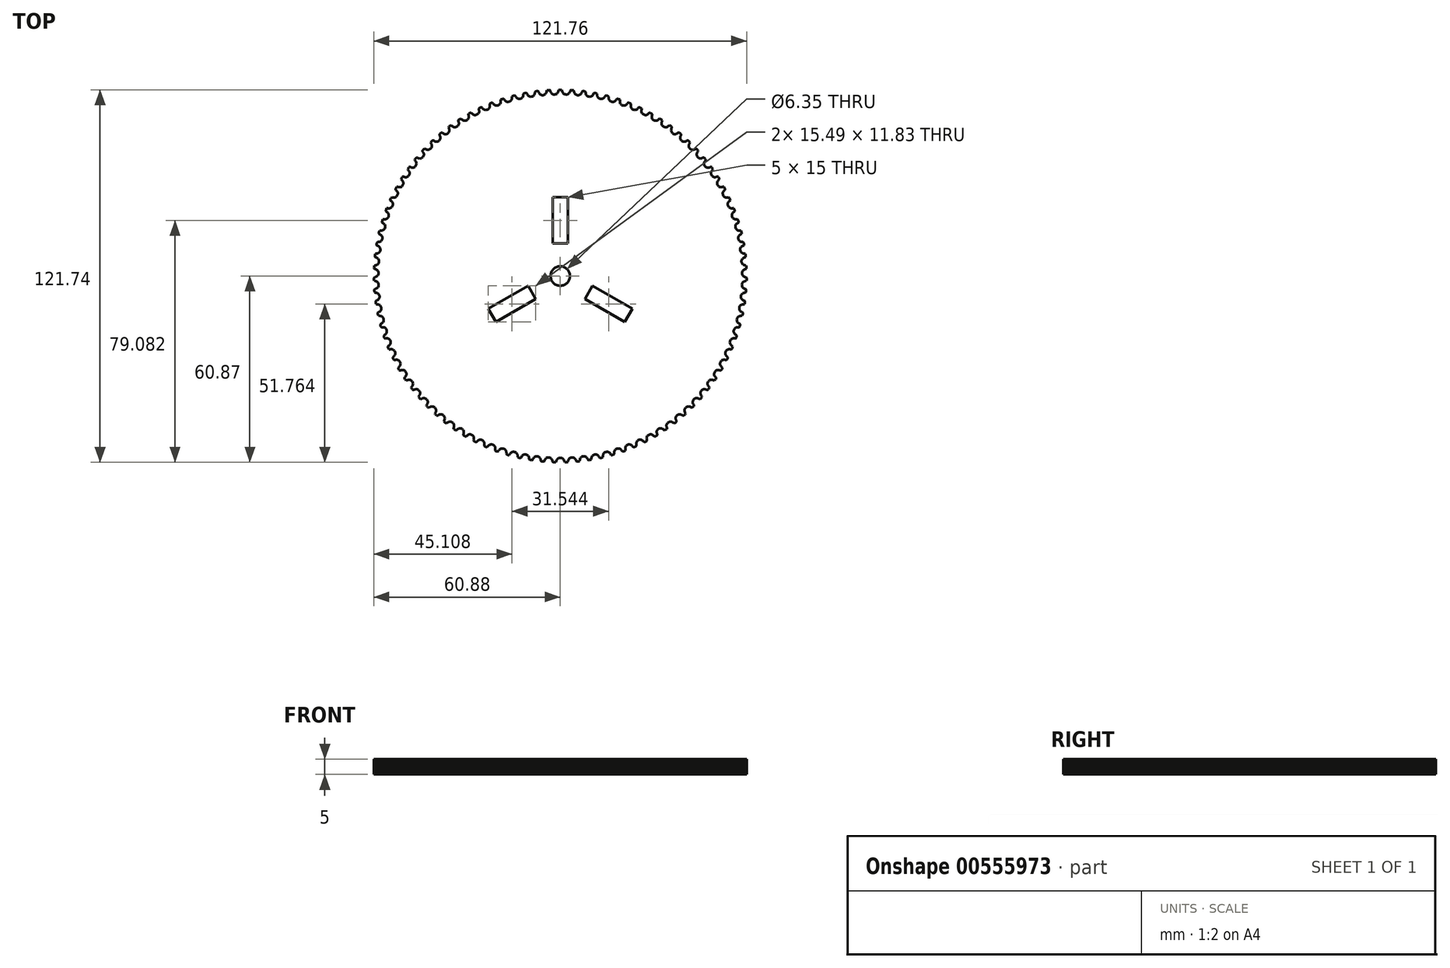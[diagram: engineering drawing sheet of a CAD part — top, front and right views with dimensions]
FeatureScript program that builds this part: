
annotation { "Feature Type Name" : "Feature", "Feature Type Description" : "" }
export const myFeature = defineFeature(function(context is Context, id is Id, definition is map)
    precondition{}
    {
        {
            var Q0;
            Q0=qCreatedBy(makeId("Top.planeOp"),FACE);
            var sketch = newSketch(context, id + "F0", { "sketchPlane" : qUnion([Q0])});
            skLineSegment(sketch, "E0", {"start": v(1.93, -60.87) * mm, "end": v(2.22, -60.86) * mm});
            skLineSegment(sketch, "E1", {"start": v(2.22, -60.86) * mm, "end": v(2.43, -60.77) * mm});
            skLineSegment(sketch, "E2", {"start": v(2.43, -60.77) * mm, "end": v(2.53, -60.58) * mm});
            skLineSegment(sketch, "E3", {"start": v(2.53, -60.58) * mm, "end": v(2.56, -60.37) * mm});
            skLineSegment(sketch, "E4", {"start": v(2.56, -60.37) * mm, "end": v(2.61, -60.16) * mm});
            skLineSegment(sketch, "E5", {"start": v(2.61, -60.16) * mm, "end": v(2.7, -59.96) * mm});
            skLineSegment(sketch, "E6", {"start": v(2.7, -59.96) * mm, "end": v(2.8, -59.77) * mm});
            skLineSegment(sketch, "E7", {"start": v(2.8, -59.77) * mm, "end": v(3, -59.57) * mm});
            skLineSegment(sketch, "E8", {"start": v(3, -59.57) * mm, "end": v(3.23, -59.41) * mm});
            skLineSegment(sketch, "E9", {"start": v(3.23, -59.41) * mm, "end": v(3.49, -59.31) * mm});
            skLineSegment(sketch, "E10", {"start": v(3.49, -59.31) * mm, "end": v(3.77, -59.27) * mm});
            skLineSegment(sketch, "E11", {"start": v(3.77, -59.27) * mm, "end": v(4.05, -59.28) * mm});
            skLineSegment(sketch, "E12", {"start": v(4.05, -59.28) * mm, "end": v(4.32, -59.34) * mm});
            skLineSegment(sketch, "E13", {"start": v(4.32, -59.34) * mm, "end": v(4.57, -59.47) * mm});
            skLineSegment(sketch, "E14", {"start": v(4.57, -59.47) * mm, "end": v(4.79, -59.64) * mm});
            skLineSegment(sketch, "E15", {"start": v(4.79, -59.64) * mm, "end": v(4.92, -59.82) * mm});
            skLineSegment(sketch, "E16", {"start": v(4.92, -59.82) * mm, "end": v(5.02, -60.01) * mm});
            skLineSegment(sketch, "E17", {"start": v(5.02, -60.01) * mm, "end": v(5.1, -60.2) * mm});
            skLineSegment(sketch, "E18", {"start": v(5.1, -60.2) * mm, "end": v(5.16, -60.42) * mm});
            skLineSegment(sketch, "E19", {"start": v(5.16, -60.42) * mm, "end": v(5.28, -60.6) * mm});
            skLineSegment(sketch, "E20", {"start": v(5.28, -60.6) * mm, "end": v(5.5, -60.65) * mm});
            skLineSegment(sketch, "E21", {"start": v(5.5, -60.65) * mm, "end": v(5.79, -60.62) * mm});
            skLineSegment(sketch, "E22", {"start": v(5.79, -60.62) * mm, "end": v(6.07, -60.6) * mm});
            skLineSegment(sketch, "E23", {"start": v(6.07, -60.6) * mm, "end": v(6.28, -60.5) * mm});
            skLineSegment(sketch, "E24", {"start": v(6.28, -60.5) * mm, "end": v(6.36, -60.3) * mm});
            skLineSegment(sketch, "E25", {"start": v(6.36, -60.3) * mm, "end": v(6.38, -60.09) * mm});
            skLineSegment(sketch, "E26", {"start": v(6.38, -60.09) * mm, "end": v(6.42, -59.88) * mm});
            skLineSegment(sketch, "E27", {"start": v(6.42, -59.88) * mm, "end": v(6.49, -59.67) * mm});
            skLineSegment(sketch, "E28", {"start": v(6.49, -59.67) * mm, "end": v(6.58, -59.47) * mm});
            skLineSegment(sketch, "E29", {"start": v(6.58, -59.47) * mm, "end": v(6.76, -59.26) * mm});
            skLineSegment(sketch, "E30", {"start": v(6.76, -59.26) * mm, "end": v(6.99, -59.09) * mm});
            skLineSegment(sketch, "E31", {"start": v(6.99, -59.09) * mm, "end": v(7.24, -58.97) * mm});
            skLineSegment(sketch, "E32", {"start": v(7.24, -58.97) * mm, "end": v(7.52, -58.9) * mm});
            skLineSegment(sketch, "E33", {"start": v(7.52, -58.9) * mm, "end": v(7.8, -58.9) * mm});
            skLineSegment(sketch, "E34", {"start": v(7.8, -58.9) * mm, "end": v(8.07, -58.95) * mm});
            skLineSegment(sketch, "E35", {"start": v(8.07, -58.95) * mm, "end": v(8.33, -59.06) * mm});
            skLineSegment(sketch, "E36", {"start": v(8.33, -59.06) * mm, "end": v(8.56, -59.22) * mm});
            skLineSegment(sketch, "E37", {"start": v(8.56, -59.22) * mm, "end": v(8.7, -59.39) * mm});
            skLineSegment(sketch, "E38", {"start": v(8.7, -59.39) * mm, "end": v(8.82, -59.57) * mm});
            skLineSegment(sketch, "E39", {"start": v(8.82, -59.57) * mm, "end": v(8.91, -59.76) * mm});
            skLineSegment(sketch, "E40", {"start": v(8.91, -59.76) * mm, "end": v(8.98, -59.97) * mm});
            skLineSegment(sketch, "E41", {"start": v(8.98, -59.97) * mm, "end": v(9.12, -60.13) * mm});
            skLineSegment(sketch, "E42", {"start": v(9.12, -60.13) * mm, "end": v(9.34, -60.18) * mm});
            skLineSegment(sketch, "E43", {"start": v(9.34, -60.18) * mm, "end": v(9.62, -60.13) * mm});
            skLineSegment(sketch, "E44", {"start": v(9.62, -60.13) * mm, "end": v(9.9, -60.09) * mm});
            skLineSegment(sketch, "E45", {"start": v(9.9, -60.09) * mm, "end": v(10.1, -59.98) * mm});
            skLineSegment(sketch, "E46", {"start": v(10.1, -59.98) * mm, "end": v(10.17, -59.78) * mm});
            skLineSegment(sketch, "E47", {"start": v(10.17, -59.78) * mm, "end": v(10.18, -59.56) * mm});
            skLineSegment(sketch, "E48", {"start": v(10.18, -59.56) * mm, "end": v(10.2, -59.35) * mm});
            skLineSegment(sketch, "E49", {"start": v(10.2, -59.35) * mm, "end": v(10.26, -59.14) * mm});
            skLineSegment(sketch, "E50", {"start": v(10.26, -59.14) * mm, "end": v(10.34, -58.93) * mm});
            skLineSegment(sketch, "E51", {"start": v(10.34, -58.93) * mm, "end": v(10.5, -58.7) * mm});
            skLineSegment(sketch, "E52", {"start": v(10.5, -58.7) * mm, "end": v(10.72, -58.53) * mm});
            skLineSegment(sketch, "E53", {"start": v(10.72, -58.53) * mm, "end": v(10.97, -58.4) * mm});
            skLineSegment(sketch, "E54", {"start": v(10.97, -58.4) * mm, "end": v(11.24, -58.31) * mm});
            skLineSegment(sketch, "E55", {"start": v(11.24, -58.31) * mm, "end": v(11.52, -58.29) * mm});
            skLineSegment(sketch, "E56", {"start": v(11.52, -58.29) * mm, "end": v(11.8, -58.32) * mm});
            skLineSegment(sketch, "E57", {"start": v(11.8, -58.32) * mm, "end": v(12.06, -58.4) * mm});
            skLineSegment(sketch, "E58", {"start": v(12.06, -58.4) * mm, "end": v(12.3, -58.56) * mm});
            skLineSegment(sketch, "E59", {"start": v(12.3, -58.56) * mm, "end": v(12.45, -58.72) * mm});
            skLineSegment(sketch, "E60", {"start": v(12.45, -58.72) * mm, "end": v(12.58, -58.9) * mm});
            skLineSegment(sketch, "E61", {"start": v(12.58, -58.9) * mm, "end": v(12.69, -59.08) * mm});
            skLineSegment(sketch, "E62", {"start": v(12.69, -59.08) * mm, "end": v(12.77, -59.28) * mm});
            skLineSegment(sketch, "E63", {"start": v(12.77, -59.28) * mm, "end": v(12.9, -59.43) * mm});
            skLineSegment(sketch, "E64", {"start": v(12.9, -59.43) * mm, "end": v(13.13, -59.46) * mm});
            skLineSegment(sketch, "E65", {"start": v(13.13, -59.46) * mm, "end": v(13.41, -59.4) * mm});
            skLineSegment(sketch, "E66", {"start": v(13.41, -59.4) * mm, "end": v(13.7, -59.34) * mm});
            skLineSegment(sketch, "E67", {"start": v(13.7, -59.34) * mm, "end": v(13.88, -59.21) * mm});
            skLineSegment(sketch, "E68", {"start": v(13.88, -59.21) * mm, "end": v(13.94, -59.01) * mm});
            skLineSegment(sketch, "E69", {"start": v(13.94, -59.01) * mm, "end": v(13.93, -58.8) * mm});
            skLineSegment(sketch, "E70", {"start": v(13.93, -58.8) * mm, "end": v(13.95, -58.58) * mm});
            skLineSegment(sketch, "E71", {"start": v(13.95, -58.58) * mm, "end": v(13.99, -58.37) * mm});
            skLineSegment(sketch, "E72", {"start": v(13.99, -58.37) * mm, "end": v(14.06, -58.16) * mm});
            skLineSegment(sketch, "E73", {"start": v(14.06, -58.16) * mm, "end": v(14.2, -57.92) * mm});
            skLineSegment(sketch, "E74", {"start": v(14.2, -57.92) * mm, "end": v(14.4, -57.73) * mm});
            skLineSegment(sketch, "E75", {"start": v(14.4, -57.73) * mm, "end": v(14.65, -57.58) * mm});
            skLineSegment(sketch, "E76", {"start": v(14.65, -57.58) * mm, "end": v(14.91, -57.48) * mm});
            skLineSegment(sketch, "E77", {"start": v(14.91, -57.48) * mm, "end": v(15.2, -57.44) * mm});
            skLineSegment(sketch, "E78", {"start": v(15.2, -57.44) * mm, "end": v(15.47, -57.45) * mm});
            skLineSegment(sketch, "E79", {"start": v(15.47, -57.45) * mm, "end": v(15.74, -57.53) * mm});
            skLineSegment(sketch, "E80", {"start": v(15.74, -57.53) * mm, "end": v(15.99, -57.66) * mm});
            skLineSegment(sketch, "E81", {"start": v(15.99, -57.66) * mm, "end": v(16.15, -57.8) * mm});
            skLineSegment(sketch, "E82", {"start": v(16.15, -57.8) * mm, "end": v(16.29, -57.98) * mm});
            skLineSegment(sketch, "E83", {"start": v(16.29, -57.98) * mm, "end": v(16.4, -58.16) * mm});
            skLineSegment(sketch, "E84", {"start": v(16.4, -58.16) * mm, "end": v(16.5, -58.35) * mm});
            skLineSegment(sketch, "E85", {"start": v(16.5, -58.35) * mm, "end": v(16.65, -58.5) * mm});
            skLineSegment(sketch, "E86", {"start": v(16.65, -58.5) * mm, "end": v(16.88, -58.51) * mm});
            skLineSegment(sketch, "E87", {"start": v(16.88, -58.51) * mm, "end": v(17.15, -58.43) * mm});
            skLineSegment(sketch, "E88", {"start": v(17.15, -58.43) * mm, "end": v(17.43, -58.35) * mm});
            skLineSegment(sketch, "E89", {"start": v(17.43, -58.35) * mm, "end": v(17.6, -58.21) * mm});
            skLineSegment(sketch, "E90", {"start": v(17.6, -58.21) * mm, "end": v(17.66, -58) * mm});
            skLineSegment(sketch, "E91", {"start": v(17.66, -58) * mm, "end": v(17.63, -57.8) * mm});
            skLineSegment(sketch, "E92", {"start": v(17.63, -57.8) * mm, "end": v(17.63, -57.58) * mm});
            skLineSegment(sketch, "E93", {"start": v(17.63, -57.58) * mm, "end": v(17.66, -57.36) * mm});
            skLineSegment(sketch, "E94", {"start": v(17.66, -57.36) * mm, "end": v(17.72, -57.15) * mm});
            skLineSegment(sketch, "E95", {"start": v(17.72, -57.15) * mm, "end": v(17.85, -56.9) * mm});
            skLineSegment(sketch, "E96", {"start": v(17.85, -56.9) * mm, "end": v(18.04, -56.7) * mm});
            skLineSegment(sketch, "E97", {"start": v(18.04, -56.7) * mm, "end": v(18.27, -56.54) * mm});
            skLineSegment(sketch, "E98", {"start": v(18.27, -56.54) * mm, "end": v(18.53, -56.42) * mm});
            skLineSegment(sketch, "E99", {"start": v(18.53, -56.42) * mm, "end": v(18.8, -56.36) * mm});
            skLineSegment(sketch, "E100", {"start": v(18.8, -56.36) * mm, "end": v(19.08, -56.36) * mm});
            skLineSegment(sketch, "E101", {"start": v(19.08, -56.36) * mm, "end": v(19.36, -56.41) * mm});
            skLineSegment(sketch, "E102", {"start": v(19.36, -56.41) * mm, "end": v(19.61, -56.53) * mm});
            skLineSegment(sketch, "E103", {"start": v(19.61, -56.53) * mm, "end": v(19.78, -56.67) * mm});
            skLineSegment(sketch, "E104", {"start": v(19.78, -56.67) * mm, "end": v(19.93, -56.83) * mm});
            skLineSegment(sketch, "E105", {"start": v(19.93, -56.83) * mm, "end": v(20.06, -57) * mm});
            skLineSegment(sketch, "E106", {"start": v(20.06, -57) * mm, "end": v(20.17, -57.18) * mm});
            skLineSegment(sketch, "E107", {"start": v(20.17, -57.18) * mm, "end": v(20.33, -57.32) * mm});
            skLineSegment(sketch, "E108", {"start": v(20.33, -57.32) * mm, "end": v(20.55, -57.32) * mm});
            skLineSegment(sketch, "E109", {"start": v(20.55, -57.32) * mm, "end": v(20.82, -57.23) * mm});
            skLineSegment(sketch, "E110", {"start": v(20.82, -57.23) * mm, "end": v(21.1, -57.13) * mm});
            skLineSegment(sketch, "E111", {"start": v(21.1, -57.13) * mm, "end": v(21.27, -56.98) * mm});
            skLineSegment(sketch, "E112", {"start": v(21.27, -56.98) * mm, "end": v(21.3, -56.77) * mm});
            skLineSegment(sketch, "E113", {"start": v(21.3, -56.77) * mm, "end": v(21.26, -56.56) * mm});
            skLineSegment(sketch, "E114", {"start": v(21.26, -56.56) * mm, "end": v(21.25, -56.35) * mm});
            skLineSegment(sketch, "E115", {"start": v(21.25, -56.35) * mm, "end": v(21.26, -56.13) * mm});
            skLineSegment(sketch, "E116", {"start": v(21.26, -56.13) * mm, "end": v(21.3, -55.91) * mm});
            skLineSegment(sketch, "E117", {"start": v(21.3, -55.91) * mm, "end": v(21.43, -55.66) * mm});
            skLineSegment(sketch, "E118", {"start": v(21.43, -55.66) * mm, "end": v(21.6, -55.44) * mm});
            skLineSegment(sketch, "E119", {"start": v(21.6, -55.44) * mm, "end": v(21.82, -55.26) * mm});
            skLineSegment(sketch, "E120", {"start": v(21.82, -55.26) * mm, "end": v(22.07, -55.13) * mm});
            skLineSegment(sketch, "E121", {"start": v(22.07, -55.13) * mm, "end": v(22.34, -55.06) * mm});
            skLineSegment(sketch, "E122", {"start": v(22.34, -55.06) * mm, "end": v(22.62, -55.03) * mm});
            skLineSegment(sketch, "E123", {"start": v(22.62, -55.03) * mm, "end": v(22.9, -55.07) * mm});
            skLineSegment(sketch, "E124", {"start": v(22.9, -55.07) * mm, "end": v(23.16, -55.17) * mm});
            skLineSegment(sketch, "E125", {"start": v(23.16, -55.17) * mm, "end": v(23.33, -55.3) * mm});
            skLineSegment(sketch, "E126", {"start": v(23.33, -55.3) * mm, "end": v(23.5, -55.45) * mm});
            skLineSegment(sketch, "E127", {"start": v(23.5, -55.45) * mm, "end": v(23.63, -55.61) * mm});
            skLineSegment(sketch, "E128", {"start": v(23.63, -55.61) * mm, "end": v(23.75, -55.79) * mm});
            skLineSegment(sketch, "E129", {"start": v(23.75, -55.79) * mm, "end": v(23.92, -55.92) * mm});
            skLineSegment(sketch, "E130", {"start": v(23.92, -55.92) * mm, "end": v(24.15, -55.9) * mm});
            skLineSegment(sketch, "E131", {"start": v(24.15, -55.9) * mm, "end": v(24.41, -55.8) * mm});
            skLineSegment(sketch, "E132", {"start": v(24.41, -55.8) * mm, "end": v(24.67, -55.67) * mm});
            skLineSegment(sketch, "E133", {"start": v(24.67, -55.67) * mm, "end": v(24.84, -55.52) * mm});
            skLineSegment(sketch, "E134", {"start": v(24.84, -55.52) * mm, "end": v(24.86, -55.3) * mm});
            skLineSegment(sketch, "E135", {"start": v(24.86, -55.3) * mm, "end": v(24.8, -55.1) * mm});
            skLineSegment(sketch, "E136", {"start": v(24.8, -55.1) * mm, "end": v(24.78, -54.88) * mm});
            skLineSegment(sketch, "E137", {"start": v(24.78, -54.88) * mm, "end": v(24.78, -54.67) * mm});
            skLineSegment(sketch, "E138", {"start": v(24.78, -54.67) * mm, "end": v(24.8, -54.45) * mm});
            skLineSegment(sketch, "E139", {"start": v(24.8, -54.45) * mm, "end": v(24.91, -54.19) * mm});
            skLineSegment(sketch, "E140", {"start": v(24.91, -54.19) * mm, "end": v(25.07, -53.96) * mm});
            skLineSegment(sketch, "E141", {"start": v(25.07, -53.96) * mm, "end": v(25.28, -53.77) * mm});
            skLineSegment(sketch, "E142", {"start": v(25.28, -53.77) * mm, "end": v(25.52, -53.62) * mm});
            skLineSegment(sketch, "E143", {"start": v(25.52, -53.62) * mm, "end": v(25.78, -53.53) * mm});
            skLineSegment(sketch, "E144", {"start": v(25.78, -53.53) * mm, "end": v(26.06, -53.49) * mm});
            skLineSegment(sketch, "E145", {"start": v(26.06, -53.49) * mm, "end": v(26.34, -53.5) * mm});
            skLineSegment(sketch, "E146", {"start": v(26.34, -53.5) * mm, "end": v(26.6, -53.59) * mm});
            skLineSegment(sketch, "E147", {"start": v(26.6, -53.59) * mm, "end": v(26.8, -53.7) * mm});
            skLineSegment(sketch, "E148", {"start": v(26.8, -53.7) * mm, "end": v(26.96, -53.85) * mm});
            skLineSegment(sketch, "E149", {"start": v(26.96, -53.85) * mm, "end": v(27.11, -54) * mm});
            skLineSegment(sketch, "E150", {"start": v(27.11, -54) * mm, "end": v(27.24, -54.17) * mm});
            skLineSegment(sketch, "E151", {"start": v(27.24, -54.17) * mm, "end": v(27.42, -54.29) * mm});
            skLineSegment(sketch, "E152", {"start": v(27.42, -54.29) * mm, "end": v(27.64, -54.26) * mm});
            skLineSegment(sketch, "E153", {"start": v(27.64, -54.26) * mm, "end": v(27.9, -54.13) * mm});
            skLineSegment(sketch, "E154", {"start": v(27.9, -54.13) * mm, "end": v(28.15, -54) * mm});
            skLineSegment(sketch, "E155", {"start": v(28.15, -54) * mm, "end": v(28.3, -53.83) * mm});
            skLineSegment(sketch, "E156", {"start": v(28.3, -53.83) * mm, "end": v(28.31, -53.62) * mm});
            skLineSegment(sketch, "E157", {"start": v(28.31, -53.62) * mm, "end": v(28.25, -53.41) * mm});
            skLineSegment(sketch, "E158", {"start": v(28.25, -53.41) * mm, "end": v(28.21, -53.2) * mm});
            skLineSegment(sketch, "E159", {"start": v(28.21, -53.2) * mm, "end": v(28.2, -52.98) * mm});
            skLineSegment(sketch, "E160", {"start": v(28.2, -52.98) * mm, "end": v(28.2, -52.76) * mm});
            skLineSegment(sketch, "E161", {"start": v(28.2, -52.76) * mm, "end": v(28.3, -52.5) * mm});
            skLineSegment(sketch, "E162", {"start": v(28.3, -52.5) * mm, "end": v(28.44, -52.26) * mm});
            skLineSegment(sketch, "E163", {"start": v(28.44, -52.26) * mm, "end": v(28.64, -52.06) * mm});
            skLineSegment(sketch, "E164", {"start": v(28.64, -52.06) * mm, "end": v(28.87, -51.9) * mm});
            skLineSegment(sketch, "E165", {"start": v(28.87, -51.9) * mm, "end": v(29.13, -51.78) * mm});
            skLineSegment(sketch, "E166", {"start": v(29.13, -51.78) * mm, "end": v(29.4, -51.73) * mm});
            skLineSegment(sketch, "E167", {"start": v(29.4, -51.73) * mm, "end": v(29.68, -51.73) * mm});
            skLineSegment(sketch, "E168", {"start": v(29.68, -51.73) * mm, "end": v(29.95, -51.8) * mm});
            skLineSegment(sketch, "E169", {"start": v(29.95, -51.8) * mm, "end": v(30.15, -51.9) * mm});
            skLineSegment(sketch, "E170", {"start": v(30.15, -51.9) * mm, "end": v(30.32, -52.03) * mm});
            skLineSegment(sketch, "E171", {"start": v(30.32, -52.03) * mm, "end": v(30.48, -52.17) * mm});
            skLineSegment(sketch, "E172", {"start": v(30.48, -52.17) * mm, "end": v(30.62, -52.33) * mm});
            skLineSegment(sketch, "E173", {"start": v(30.62, -52.33) * mm, "end": v(30.8, -52.44) * mm});
            skLineSegment(sketch, "E174", {"start": v(30.8, -52.44) * mm, "end": v(31.03, -52.4) * mm});
            skLineSegment(sketch, "E175", {"start": v(31.03, -52.4) * mm, "end": v(31.28, -52.25) * mm});
            skLineSegment(sketch, "E176", {"start": v(31.28, -52.25) * mm, "end": v(31.52, -52.1) * mm});
            skLineSegment(sketch, "E177", {"start": v(31.52, -52.1) * mm, "end": v(31.66, -51.93) * mm});
            skLineSegment(sketch, "E178", {"start": v(31.66, -51.93) * mm, "end": v(31.66, -51.71) * mm});
            skLineSegment(sketch, "E179", {"start": v(31.66, -51.71) * mm, "end": v(31.58, -51.51) * mm});
            skLineSegment(sketch, "E180", {"start": v(31.58, -51.51) * mm, "end": v(31.53, -51.3) * mm});
            skLineSegment(sketch, "E181", {"start": v(31.53, -51.3) * mm, "end": v(31.5, -51.09) * mm});
            skLineSegment(sketch, "E182", {"start": v(31.5, -51.09) * mm, "end": v(31.5, -50.87) * mm});
            skLineSegment(sketch, "E183", {"start": v(31.5, -50.87) * mm, "end": v(31.57, -50.6) * mm});
            skLineSegment(sketch, "E184", {"start": v(31.57, -50.6) * mm, "end": v(31.7, -50.35) * mm});
            skLineSegment(sketch, "E185", {"start": v(31.7, -50.35) * mm, "end": v(31.88, -50.14) * mm});
            skLineSegment(sketch, "E186", {"start": v(31.88, -50.14) * mm, "end": v(32.1, -49.96) * mm});
            skLineSegment(sketch, "E187", {"start": v(32.1, -49.96) * mm, "end": v(32.35, -49.83) * mm});
            skLineSegment(sketch, "E188", {"start": v(32.35, -49.83) * mm, "end": v(32.62, -49.76) * mm});
            skLineSegment(sketch, "E189", {"start": v(32.62, -49.76) * mm, "end": v(32.9, -49.74) * mm});
            skLineSegment(sketch, "E190", {"start": v(32.9, -49.74) * mm, "end": v(33.18, -49.8) * mm});
            skLineSegment(sketch, "E191", {"start": v(33.18, -49.8) * mm, "end": v(33.38, -49.88) * mm});
            skLineSegment(sketch, "E192", {"start": v(33.38, -49.88) * mm, "end": v(33.56, -50) * mm});
            skLineSegment(sketch, "E193", {"start": v(33.56, -50) * mm, "end": v(33.73, -50.13) * mm});
            skLineSegment(sketch, "E194", {"start": v(33.73, -50.13) * mm, "end": v(33.88, -50.29) * mm});
            skLineSegment(sketch, "E195", {"start": v(33.88, -50.29) * mm, "end": v(34.07, -50.38) * mm});
            skLineSegment(sketch, "E196", {"start": v(34.07, -50.38) * mm, "end": v(34.29, -50.32) * mm});
            skLineSegment(sketch, "E197", {"start": v(34.29, -50.32) * mm, "end": v(34.53, -50.16) * mm});
            skLineSegment(sketch, "E198", {"start": v(34.53, -50.16) * mm, "end": v(34.76, -50) * mm});
            skLineSegment(sketch, "E199", {"start": v(34.76, -50) * mm, "end": v(34.9, -49.81) * mm});
            skLineSegment(sketch, "E200", {"start": v(34.9, -49.81) * mm, "end": v(34.87, -49.6) * mm});
            skLineSegment(sketch, "E201", {"start": v(34.87, -49.6) * mm, "end": v(34.78, -49.4) * mm});
            skLineSegment(sketch, "E202", {"start": v(34.78, -49.4) * mm, "end": v(34.72, -49.2) * mm});
            skLineSegment(sketch, "E203", {"start": v(34.72, -49.2) * mm, "end": v(34.68, -48.99) * mm});
            skLineSegment(sketch, "E204", {"start": v(34.68, -48.99) * mm, "end": v(34.66, -48.77) * mm});
            skLineSegment(sketch, "E205", {"start": v(34.66, -48.77) * mm, "end": v(34.71, -48.5) * mm});
            skLineSegment(sketch, "E206", {"start": v(34.71, -48.5) * mm, "end": v(34.83, -48.24) * mm});
            skLineSegment(sketch, "E207", {"start": v(34.83, -48.24) * mm, "end": v(35, -48.01) * mm});
            skLineSegment(sketch, "E208", {"start": v(35, -48.01) * mm, "end": v(35.2, -47.82) * mm});
            skLineSegment(sketch, "E209", {"start": v(35.2, -47.82) * mm, "end": v(35.45, -47.68) * mm});
            skLineSegment(sketch, "E210", {"start": v(35.45, -47.68) * mm, "end": v(35.71, -47.59) * mm});
            skLineSegment(sketch, "E211", {"start": v(35.71, -47.59) * mm, "end": v(35.99, -47.56) * mm});
            skLineSegment(sketch, "E212", {"start": v(35.99, -47.56) * mm, "end": v(36.27, -47.59) * mm});
            skLineSegment(sketch, "E213", {"start": v(36.27, -47.59) * mm, "end": v(36.47, -47.67) * mm});
            skLineSegment(sketch, "E214", {"start": v(36.47, -47.67) * mm, "end": v(36.66, -47.77) * mm});
            skLineSegment(sketch, "E215", {"start": v(36.66, -47.77) * mm, "end": v(36.84, -47.9) * mm});
            skLineSegment(sketch, "E216", {"start": v(36.84, -47.9) * mm, "end": v(37, -48.04) * mm});
            skLineSegment(sketch, "E217", {"start": v(37, -48.04) * mm, "end": v(37.2, -48.12) * mm});
            skLineSegment(sketch, "E218", {"start": v(37.2, -48.12) * mm, "end": v(37.41, -48.05) * mm});
            skLineSegment(sketch, "E219", {"start": v(37.41, -48.05) * mm, "end": v(37.64, -47.87) * mm});
            skLineSegment(sketch, "E220", {"start": v(37.64, -47.87) * mm, "end": v(37.86, -47.7) * mm});
            skLineSegment(sketch, "E221", {"start": v(37.86, -47.7) * mm, "end": v(37.98, -47.5) * mm});
            skLineSegment(sketch, "E222", {"start": v(37.98, -47.5) * mm, "end": v(37.95, -47.3) * mm});
            skLineSegment(sketch, "E223", {"start": v(37.95, -47.3) * mm, "end": v(37.85, -47.1) * mm});
            skLineSegment(sketch, "E224", {"start": v(37.85, -47.1) * mm, "end": v(37.77, -46.9) * mm});
            skLineSegment(sketch, "E225", {"start": v(37.77, -46.9) * mm, "end": v(37.71, -46.7) * mm});
            skLineSegment(sketch, "E226", {"start": v(37.71, -46.7) * mm, "end": v(37.68, -46.47) * mm});
            skLineSegment(sketch, "E227", {"start": v(37.68, -46.47) * mm, "end": v(37.72, -46.2) * mm});
            skLineSegment(sketch, "E228", {"start": v(37.72, -46.2) * mm, "end": v(37.82, -45.93) * mm});
            skLineSegment(sketch, "E229", {"start": v(37.82, -45.93) * mm, "end": v(37.97, -45.7) * mm});
            skLineSegment(sketch, "E230", {"start": v(37.97, -45.7) * mm, "end": v(38.17, -45.5) * mm});
            skLineSegment(sketch, "E231", {"start": v(38.17, -45.5) * mm, "end": v(38.4, -45.34) * mm});
            skLineSegment(sketch, "E232", {"start": v(38.4, -45.34) * mm, "end": v(38.66, -45.23) * mm});
            skLineSegment(sketch, "E233", {"start": v(38.66, -45.23) * mm, "end": v(38.93, -45.18) * mm});
            skLineSegment(sketch, "E234", {"start": v(38.93, -45.18) * mm, "end": v(39.21, -45.2) * mm});
            skLineSegment(sketch, "E235", {"start": v(39.21, -45.2) * mm, "end": v(39.42, -45.26) * mm});
            skLineSegment(sketch, "E236", {"start": v(39.42, -45.26) * mm, "end": v(39.62, -45.35) * mm});
            skLineSegment(sketch, "E237", {"start": v(39.62, -45.35) * mm, "end": v(39.8, -45.46) * mm});
            skLineSegment(sketch, "E238", {"start": v(39.8, -45.46) * mm, "end": v(39.97, -45.6) * mm});
            skLineSegment(sketch, "E239", {"start": v(39.97, -45.6) * mm, "end": v(40.17, -45.66) * mm});
            skLineSegment(sketch, "E240", {"start": v(40.17, -45.66) * mm, "end": v(40.38, -45.58) * mm});
            skLineSegment(sketch, "E241", {"start": v(40.38, -45.58) * mm, "end": v(40.6, -45.39) * mm});
            skLineSegment(sketch, "E242", {"start": v(40.6, -45.39) * mm, "end": v(40.8, -45.2) * mm});
            skLineSegment(sketch, "E243", {"start": v(40.8, -45.2) * mm, "end": v(40.92, -45) * mm});
            skLineSegment(sketch, "E244", {"start": v(40.92, -45) * mm, "end": v(40.87, -44.79) * mm});
            skLineSegment(sketch, "E245", {"start": v(40.87, -44.79) * mm, "end": v(40.76, -44.6) * mm});
            skLineSegment(sketch, "E246", {"start": v(40.76, -44.6) * mm, "end": v(40.67, -44.41) * mm});
            skLineSegment(sketch, "E247", {"start": v(40.67, -44.41) * mm, "end": v(40.6, -44.2) * mm});
            skLineSegment(sketch, "E248", {"start": v(40.6, -44.2) * mm, "end": v(40.55, -43.99) * mm});
            skLineSegment(sketch, "E249", {"start": v(40.55, -43.99) * mm, "end": v(40.57, -43.7) * mm});
            skLineSegment(sketch, "E250", {"start": v(40.57, -43.7) * mm, "end": v(40.65, -43.44) * mm});
            skLineSegment(sketch, "E251", {"start": v(40.65, -43.44) * mm, "end": v(40.79, -43.2) * mm});
            skLineSegment(sketch, "E252", {"start": v(40.79, -43.2) * mm, "end": v(40.97, -42.98) * mm});
            skLineSegment(sketch, "E253", {"start": v(40.97, -42.98) * mm, "end": v(41.2, -42.81) * mm});
            skLineSegment(sketch, "E254", {"start": v(41.2, -42.81) * mm, "end": v(41.45, -42.69) * mm});
            skLineSegment(sketch, "E255", {"start": v(41.45, -42.69) * mm, "end": v(41.72, -42.62) * mm});
            skLineSegment(sketch, "E256", {"start": v(41.72, -42.62) * mm, "end": v(42, -42.61) * mm});
            skLineSegment(sketch, "E257", {"start": v(42, -42.61) * mm, "end": v(42.21, -42.67) * mm});
            skLineSegment(sketch, "E258", {"start": v(42.21, -42.67) * mm, "end": v(42.41, -42.74) * mm});
            skLineSegment(sketch, "E259", {"start": v(42.41, -42.74) * mm, "end": v(42.6, -42.84) * mm});
            skLineSegment(sketch, "E260", {"start": v(42.6, -42.84) * mm, "end": v(42.78, -42.97) * mm});
            skLineSegment(sketch, "E261", {"start": v(42.78, -42.97) * mm, "end": v(42.99, -43.02) * mm});
            skLineSegment(sketch, "E262", {"start": v(42.99, -43.02) * mm, "end": v(43.2, -42.92) * mm});
            skLineSegment(sketch, "E263", {"start": v(43.2, -42.92) * mm, "end": v(43.4, -42.72) * mm});
            skLineSegment(sketch, "E264", {"start": v(43.4, -42.72) * mm, "end": v(43.6, -42.52) * mm});
            skLineSegment(sketch, "E265", {"start": v(43.6, -42.52) * mm, "end": v(43.69, -42.31) * mm});
            skLineSegment(sketch, "E266", {"start": v(43.69, -42.31) * mm, "end": v(43.63, -42.1) * mm});
            skLineSegment(sketch, "E267", {"start": v(43.63, -42.1) * mm, "end": v(43.5, -41.93) * mm});
            skLineSegment(sketch, "E268", {"start": v(43.5, -41.93) * mm, "end": v(43.4, -41.74) * mm});
            skLineSegment(sketch, "E269", {"start": v(43.4, -41.74) * mm, "end": v(43.32, -41.54) * mm});
            skLineSegment(sketch, "E270", {"start": v(43.32, -41.54) * mm, "end": v(43.26, -41.33) * mm});
            skLineSegment(sketch, "E271", {"start": v(43.26, -41.33) * mm, "end": v(43.26, -41.05) * mm});
            skLineSegment(sketch, "E272", {"start": v(43.26, -41.05) * mm, "end": v(43.33, -40.78) * mm});
            skLineSegment(sketch, "E273", {"start": v(43.33, -40.78) * mm, "end": v(43.45, -40.52) * mm});
            skLineSegment(sketch, "E274", {"start": v(43.45, -40.52) * mm, "end": v(43.62, -40.3) * mm});
            skLineSegment(sketch, "E275", {"start": v(43.62, -40.3) * mm, "end": v(43.83, -40.11) * mm});
            skLineSegment(sketch, "E276", {"start": v(43.83, -40.11) * mm, "end": v(44.07, -39.97) * mm});
            skLineSegment(sketch, "E277", {"start": v(44.07, -39.97) * mm, "end": v(44.34, -39.89) * mm});
            skLineSegment(sketch, "E278", {"start": v(44.34, -39.89) * mm, "end": v(44.61, -39.86) * mm});
            skLineSegment(sketch, "E279", {"start": v(44.61, -39.86) * mm, "end": v(44.83, -39.9) * mm});
            skLineSegment(sketch, "E280", {"start": v(44.83, -39.9) * mm, "end": v(45.04, -39.97) * mm});
            skLineSegment(sketch, "E281", {"start": v(45.04, -39.97) * mm, "end": v(45.24, -40.06) * mm});
            skLineSegment(sketch, "E282", {"start": v(45.24, -40.06) * mm, "end": v(45.42, -40.17) * mm});
            skLineSegment(sketch, "E283", {"start": v(45.42, -40.17) * mm, "end": v(45.63, -40.2) * mm});
            skLineSegment(sketch, "E284", {"start": v(45.63, -40.2) * mm, "end": v(45.83, -40.1) * mm});
            skLineSegment(sketch, "E285", {"start": v(45.83, -40.1) * mm, "end": v(46.01, -39.88) * mm});
            skLineSegment(sketch, "E286", {"start": v(46.01, -39.88) * mm, "end": v(46.2, -39.67) * mm});
            skLineSegment(sketch, "E287", {"start": v(46.2, -39.67) * mm, "end": v(46.28, -39.46) * mm});
            skLineSegment(sketch, "E288", {"start": v(46.28, -39.46) * mm, "end": v(46.2, -39.26) * mm});
            skLineSegment(sketch, "E289", {"start": v(46.2, -39.26) * mm, "end": v(46.07, -39.09) * mm});
            skLineSegment(sketch, "E290", {"start": v(46.07, -39.09) * mm, "end": v(45.96, -38.9) * mm});
            skLineSegment(sketch, "E291", {"start": v(45.96, -38.9) * mm, "end": v(45.87, -38.71) * mm});
            skLineSegment(sketch, "E292", {"start": v(45.87, -38.71) * mm, "end": v(45.8, -38.5) * mm});
            skLineSegment(sketch, "E293", {"start": v(45.8, -38.5) * mm, "end": v(45.78, -38.22) * mm});
            skLineSegment(sketch, "E294", {"start": v(45.78, -38.22) * mm, "end": v(45.82, -37.95) * mm});
            skLineSegment(sketch, "E295", {"start": v(45.82, -37.95) * mm, "end": v(45.93, -37.69) * mm});
            skLineSegment(sketch, "E296", {"start": v(45.93, -37.69) * mm, "end": v(46.08, -37.45) * mm});
            skLineSegment(sketch, "E297", {"start": v(46.08, -37.45) * mm, "end": v(46.28, -37.25) * mm});
            skLineSegment(sketch, "E298", {"start": v(46.28, -37.25) * mm, "end": v(46.52, -37.1) * mm});
            skLineSegment(sketch, "E299", {"start": v(46.52, -37.1) * mm, "end": v(46.78, -37) * mm});
            skLineSegment(sketch, "E300", {"start": v(46.78, -37) * mm, "end": v(47.05, -36.95) * mm});
            skLineSegment(sketch, "E301", {"start": v(47.05, -36.95) * mm, "end": v(47.27, -36.98) * mm});
            skLineSegment(sketch, "E302", {"start": v(47.27, -36.98) * mm, "end": v(47.48, -37.03) * mm});
            skLineSegment(sketch, "E303", {"start": v(47.48, -37.03) * mm, "end": v(47.68, -37.1) * mm});
            skLineSegment(sketch, "E304", {"start": v(47.68, -37.1) * mm, "end": v(47.88, -37.2) * mm});
            skLineSegment(sketch, "E305", {"start": v(47.88, -37.2) * mm, "end": v(48.09, -37.23) * mm});
            skLineSegment(sketch, "E306", {"start": v(48.09, -37.23) * mm, "end": v(48.28, -37.11) * mm});
            skLineSegment(sketch, "E307", {"start": v(48.28, -37.11) * mm, "end": v(48.45, -36.89) * mm});
            skLineSegment(sketch, "E308", {"start": v(48.45, -36.89) * mm, "end": v(48.62, -36.66) * mm});
            skLineSegment(sketch, "E309", {"start": v(48.62, -36.66) * mm, "end": v(48.69, -36.44) * mm});
            skLineSegment(sketch, "E310", {"start": v(48.69, -36.44) * mm, "end": v(48.6, -36.25) * mm});
            skLineSegment(sketch, "E311", {"start": v(48.6, -36.25) * mm, "end": v(48.46, -36.09) * mm});
            skLineSegment(sketch, "E312", {"start": v(48.46, -36.09) * mm, "end": v(48.33, -35.91) * mm});
            skLineSegment(sketch, "E313", {"start": v(48.33, -35.91) * mm, "end": v(48.23, -35.72) * mm});
            skLineSegment(sketch, "E314", {"start": v(48.23, -35.72) * mm, "end": v(48.14, -35.52) * mm});
            skLineSegment(sketch, "E315", {"start": v(48.14, -35.52) * mm, "end": v(48.1, -35.24) * mm});
            skLineSegment(sketch, "E316", {"start": v(48.1, -35.24) * mm, "end": v(48.14, -34.96) * mm});
            skLineSegment(sketch, "E317", {"start": v(48.14, -34.96) * mm, "end": v(48.23, -34.7) * mm});
            skLineSegment(sketch, "E318", {"start": v(48.23, -34.7) * mm, "end": v(48.37, -34.45) * mm});
            skLineSegment(sketch, "E319", {"start": v(48.37, -34.45) * mm, "end": v(48.55, -34.24) * mm});
            skLineSegment(sketch, "E320", {"start": v(48.55, -34.24) * mm, "end": v(48.77, -34.07) * mm});
            skLineSegment(sketch, "E321", {"start": v(48.77, -34.07) * mm, "end": v(49.03, -33.95) * mm});
            skLineSegment(sketch, "E322", {"start": v(49.03, -33.95) * mm, "end": v(49.3, -33.9) * mm});
            skLineSegment(sketch, "E323", {"start": v(49.3, -33.9) * mm, "end": v(49.52, -33.9) * mm});
            skLineSegment(sketch, "E324", {"start": v(49.52, -33.9) * mm, "end": v(49.74, -33.94) * mm});
            skLineSegment(sketch, "E325", {"start": v(49.74, -33.94) * mm, "end": v(49.94, -34) * mm});
            skLineSegment(sketch, "E326", {"start": v(49.94, -34) * mm, "end": v(50.14, -34.1) * mm});
            skLineSegment(sketch, "E327", {"start": v(50.14, -34.1) * mm, "end": v(50.35, -34.1) * mm});
            skLineSegment(sketch, "E328", {"start": v(50.35, -34.1) * mm, "end": v(50.53, -33.98) * mm});
            skLineSegment(sketch, "E329", {"start": v(50.53, -33.98) * mm, "end": v(50.7, -33.74) * mm});
            skLineSegment(sketch, "E330", {"start": v(50.7, -33.74) * mm, "end": v(50.85, -33.5) * mm});
            skLineSegment(sketch, "E331", {"start": v(50.85, -33.5) * mm, "end": v(50.9, -33.28) * mm});
            skLineSegment(sketch, "E332", {"start": v(50.9, -33.28) * mm, "end": v(50.8, -33.09) * mm});
            skLineSegment(sketch, "E333", {"start": v(50.8, -33.09) * mm, "end": v(50.65, -32.94) * mm});
            skLineSegment(sketch, "E334", {"start": v(50.65, -32.94) * mm, "end": v(50.51, -32.78) * mm});
            skLineSegment(sketch, "E335", {"start": v(50.51, -32.78) * mm, "end": v(50.4, -32.6) * mm});
            skLineSegment(sketch, "E336", {"start": v(50.4, -32.6) * mm, "end": v(50.3, -32.4) * mm});
            skLineSegment(sketch, "E337", {"start": v(50.3, -32.4) * mm, "end": v(50.25, -32.12) * mm});
            skLineSegment(sketch, "E338", {"start": v(50.25, -32.12) * mm, "end": v(50.26, -31.84) * mm});
            skLineSegment(sketch, "E339", {"start": v(50.26, -31.84) * mm, "end": v(50.33, -31.57) * mm});
            skLineSegment(sketch, "E340", {"start": v(50.33, -31.57) * mm, "end": v(50.45, -31.32) * mm});
            skLineSegment(sketch, "E341", {"start": v(50.45, -31.32) * mm, "end": v(50.62, -31.1) * mm});
            skLineSegment(sketch, "E342", {"start": v(50.62, -31.1) * mm, "end": v(50.84, -30.9) * mm});
            skLineSegment(sketch, "E343", {"start": v(50.84, -30.9) * mm, "end": v(51.08, -30.77) * mm});
            skLineSegment(sketch, "E344", {"start": v(51.08, -30.77) * mm, "end": v(51.35, -30.7) * mm});
            skLineSegment(sketch, "E345", {"start": v(51.35, -30.7) * mm, "end": v(51.57, -30.7) * mm});
            skLineSegment(sketch, "E346", {"start": v(51.57, -30.7) * mm, "end": v(51.79, -30.72) * mm});
            skLineSegment(sketch, "E347", {"start": v(51.79, -30.72) * mm, "end": v(52, -30.77) * mm});
            skLineSegment(sketch, "E348", {"start": v(52, -30.77) * mm, "end": v(52.2, -30.84) * mm});
            skLineSegment(sketch, "E349", {"start": v(52.2, -30.84) * mm, "end": v(52.41, -30.85) * mm});
            skLineSegment(sketch, "E350", {"start": v(52.41, -30.85) * mm, "end": v(52.58, -30.7) * mm});
            skLineSegment(sketch, "E351", {"start": v(52.58, -30.7) * mm, "end": v(52.73, -30.46) * mm});
            skLineSegment(sketch, "E352", {"start": v(52.73, -30.46) * mm, "end": v(52.87, -30.2) * mm});
            skLineSegment(sketch, "E353", {"start": v(52.87, -30.2) * mm, "end": v(52.9, -29.98) * mm});
            skLineSegment(sketch, "E354", {"start": v(52.9, -29.98) * mm, "end": v(52.8, -29.8) * mm});
            skLineSegment(sketch, "E355", {"start": v(52.8, -29.8) * mm, "end": v(52.64, -29.66) * mm});
            skLineSegment(sketch, "E356", {"start": v(52.64, -29.66) * mm, "end": v(52.49, -29.5) * mm});
            skLineSegment(sketch, "E357", {"start": v(52.49, -29.5) * mm, "end": v(52.36, -29.33) * mm});
            skLineSegment(sketch, "E358", {"start": v(52.36, -29.33) * mm, "end": v(52.25, -29.14) * mm});
            skLineSegment(sketch, "E359", {"start": v(52.25, -29.14) * mm, "end": v(52.18, -28.87) * mm});
            skLineSegment(sketch, "E360", {"start": v(52.18, -28.87) * mm, "end": v(52.18, -28.59) * mm});
            skLineSegment(sketch, "E361", {"start": v(52.18, -28.59) * mm, "end": v(52.23, -28.31) * mm});
            skLineSegment(sketch, "E362", {"start": v(52.23, -28.31) * mm, "end": v(52.34, -28.05) * mm});
            skLineSegment(sketch, "E363", {"start": v(52.34, -28.05) * mm, "end": v(52.5, -27.82) * mm});
            skLineSegment(sketch, "E364", {"start": v(52.5, -27.82) * mm, "end": v(52.7, -27.62) * mm});
            skLineSegment(sketch, "E365", {"start": v(52.7, -27.62) * mm, "end": v(52.93, -27.47) * mm});
            skLineSegment(sketch, "E366", {"start": v(52.93, -27.47) * mm, "end": v(53.2, -27.38) * mm});
            skLineSegment(sketch, "E367", {"start": v(53.2, -27.38) * mm, "end": v(53.41, -27.37) * mm});
            skLineSegment(sketch, "E368", {"start": v(53.41, -27.37) * mm, "end": v(53.63, -27.38) * mm});
            skLineSegment(sketch, "E369", {"start": v(53.63, -27.38) * mm, "end": v(53.84, -27.41) * mm});
            skLineSegment(sketch, "E370", {"start": v(53.84, -27.41) * mm, "end": v(54.05, -27.47) * mm});
            skLineSegment(sketch, "E371", {"start": v(54.05, -27.47) * mm, "end": v(54.26, -27.46) * mm});
            skLineSegment(sketch, "E372", {"start": v(54.26, -27.46) * mm, "end": v(54.42, -27.3) * mm});
            skLineSegment(sketch, "E373", {"start": v(54.42, -27.3) * mm, "end": v(54.55, -27.05) * mm});
            skLineSegment(sketch, "E374", {"start": v(54.55, -27.05) * mm, "end": v(54.68, -26.8) * mm});
            skLineSegment(sketch, "E375", {"start": v(54.68, -26.8) * mm, "end": v(54.7, -26.57) * mm});
            skLineSegment(sketch, "E376", {"start": v(54.7, -26.57) * mm, "end": v(54.58, -26.4) * mm});
            skLineSegment(sketch, "E377", {"start": v(54.58, -26.4) * mm, "end": v(54.41, -26.27) * mm});
            skLineSegment(sketch, "E378", {"start": v(54.41, -26.27) * mm, "end": v(54.25, -26.12) * mm});
            skLineSegment(sketch, "E379", {"start": v(54.25, -26.12) * mm, "end": v(54.11, -25.95) * mm});
            skLineSegment(sketch, "E380", {"start": v(54.11, -25.95) * mm, "end": v(54, -25.77) * mm});
            skLineSegment(sketch, "E381", {"start": v(54, -25.77) * mm, "end": v(53.9, -25.5) * mm});
            skLineSegment(sketch, "E382", {"start": v(53.9, -25.5) * mm, "end": v(53.88, -25.22) * mm});
            skLineSegment(sketch, "E383", {"start": v(53.88, -25.22) * mm, "end": v(53.92, -24.94) * mm});
            skLineSegment(sketch, "E384", {"start": v(53.92, -24.94) * mm, "end": v(54, -24.68) * mm});
            skLineSegment(sketch, "E385", {"start": v(54, -24.68) * mm, "end": v(54.15, -24.43) * mm});
            skLineSegment(sketch, "E386", {"start": v(54.15, -24.43) * mm, "end": v(54.34, -24.22) * mm});
            skLineSegment(sketch, "E387", {"start": v(54.34, -24.22) * mm, "end": v(54.56, -24.06) * mm});
            skLineSegment(sketch, "E388", {"start": v(54.56, -24.06) * mm, "end": v(54.82, -23.95) * mm});
            skLineSegment(sketch, "E389", {"start": v(54.82, -23.95) * mm, "end": v(55.04, -23.92) * mm});
            skLineSegment(sketch, "E390", {"start": v(55.04, -23.92) * mm, "end": v(55.26, -23.92) * mm});
            skLineSegment(sketch, "E391", {"start": v(55.26, -23.92) * mm, "end": v(55.47, -23.94) * mm});
            skLineSegment(sketch, "E392", {"start": v(55.47, -23.94) * mm, "end": v(55.68, -23.99) * mm});
            skLineSegment(sketch, "E393", {"start": v(55.68, -23.99) * mm, "end": v(55.9, -23.96) * mm});
            skLineSegment(sketch, "E394", {"start": v(55.9, -23.96) * mm, "end": v(56.05, -23.8) * mm});
            skLineSegment(sketch, "E395", {"start": v(56.05, -23.8) * mm, "end": v(56.16, -23.54) * mm});
            skLineSegment(sketch, "E396", {"start": v(56.16, -23.54) * mm, "end": v(56.27, -23.27) * mm});
            skLineSegment(sketch, "E397", {"start": v(56.27, -23.27) * mm, "end": v(56.28, -23.04) * mm});
            skLineSegment(sketch, "E398", {"start": v(56.28, -23.04) * mm, "end": v(56.15, -22.88) * mm});
            skLineSegment(sketch, "E399", {"start": v(56.15, -22.88) * mm, "end": v(55.97, -22.76) * mm});
            skLineSegment(sketch, "E400", {"start": v(55.97, -22.76) * mm, "end": v(55.8, -22.62) * mm});
            skLineSegment(sketch, "E401", {"start": v(55.8, -22.62) * mm, "end": v(55.65, -22.47) * mm});
            skLineSegment(sketch, "E402", {"start": v(55.65, -22.47) * mm, "end": v(55.52, -22.3) * mm});
            skLineSegment(sketch, "E403", {"start": v(55.52, -22.3) * mm, "end": v(55.41, -22.03) * mm});
            skLineSegment(sketch, "E404", {"start": v(55.41, -22.03) * mm, "end": v(55.37, -21.75) * mm});
            skLineSegment(sketch, "E405", {"start": v(55.37, -21.75) * mm, "end": v(55.4, -21.47) * mm});
            skLineSegment(sketch, "E406", {"start": v(55.4, -21.47) * mm, "end": v(55.47, -21.2) * mm});
            skLineSegment(sketch, "E407", {"start": v(55.47, -21.2) * mm, "end": v(55.6, -20.95) * mm});
            skLineSegment(sketch, "E408", {"start": v(55.6, -20.95) * mm, "end": v(55.76, -20.73) * mm});
            skLineSegment(sketch, "E409", {"start": v(55.76, -20.73) * mm, "end": v(55.98, -20.55) * mm});
            skLineSegment(sketch, "E410", {"start": v(55.98, -20.55) * mm, "end": v(56.23, -20.43) * mm});
            skLineSegment(sketch, "E411", {"start": v(56.23, -20.43) * mm, "end": v(56.45, -20.38) * mm});
            skLineSegment(sketch, "E412", {"start": v(56.45, -20.38) * mm, "end": v(56.66, -20.37) * mm});
            skLineSegment(sketch, "E413", {"start": v(56.66, -20.37) * mm, "end": v(56.88, -20.37) * mm});
            skLineSegment(sketch, "E414", {"start": v(56.88, -20.37) * mm, "end": v(57.1, -20.4) * mm});
            skLineSegment(sketch, "E415", {"start": v(57.1, -20.4) * mm, "end": v(57.3, -20.37) * mm});
            skLineSegment(sketch, "E416", {"start": v(57.3, -20.37) * mm, "end": v(57.44, -20.2) * mm});
            skLineSegment(sketch, "E417", {"start": v(57.44, -20.2) * mm, "end": v(57.54, -19.93) * mm});
            skLineSegment(sketch, "E418", {"start": v(57.54, -19.93) * mm, "end": v(57.63, -19.65) * mm});
            skLineSegment(sketch, "E419", {"start": v(57.63, -19.65) * mm, "end": v(57.63, -19.43) * mm});
            skLineSegment(sketch, "E420", {"start": v(57.63, -19.43) * mm, "end": v(57.48, -19.27) * mm});
            skLineSegment(sketch, "E421", {"start": v(57.48, -19.27) * mm, "end": v(57.3, -19.17) * mm});
            skLineSegment(sketch, "E422", {"start": v(57.3, -19.17) * mm, "end": v(57.12, -19.04) * mm});
            skLineSegment(sketch, "E423", {"start": v(57.12, -19.04) * mm, "end": v(56.96, -18.9) * mm});
            skLineSegment(sketch, "E424", {"start": v(56.96, -18.9) * mm, "end": v(56.82, -18.72) * mm});
            skLineSegment(sketch, "E425", {"start": v(56.82, -18.72) * mm, "end": v(56.7, -18.47) * mm});
            skLineSegment(sketch, "E426", {"start": v(56.7, -18.47) * mm, "end": v(56.64, -18.2) * mm});
            skLineSegment(sketch, "E427", {"start": v(56.64, -18.2) * mm, "end": v(56.64, -17.92) * mm});
            skLineSegment(sketch, "E428", {"start": v(56.64, -17.92) * mm, "end": v(56.7, -17.64) * mm});
            skLineSegment(sketch, "E429", {"start": v(56.7, -17.64) * mm, "end": v(56.8, -17.38) * mm});
            skLineSegment(sketch, "E430", {"start": v(56.8, -17.38) * mm, "end": v(56.97, -17.15) * mm});
            skLineSegment(sketch, "E431", {"start": v(56.97, -17.15) * mm, "end": v(57.17, -16.96) * mm});
            skLineSegment(sketch, "E432", {"start": v(57.17, -16.96) * mm, "end": v(57.41, -16.82) * mm});
            skLineSegment(sketch, "E433", {"start": v(57.41, -16.82) * mm, "end": v(57.62, -16.76) * mm});
            skLineSegment(sketch, "E434", {"start": v(57.62, -16.76) * mm, "end": v(57.84, -16.73) * mm});
            skLineSegment(sketch, "E435", {"start": v(57.84, -16.73) * mm, "end": v(58.06, -16.73) * mm});
            skLineSegment(sketch, "E436", {"start": v(58.06, -16.73) * mm, "end": v(58.27, -16.75) * mm});
            skLineSegment(sketch, "E437", {"start": v(58.27, -16.75) * mm, "end": v(58.47, -16.7) * mm});
            skLineSegment(sketch, "E438", {"start": v(58.47, -16.7) * mm, "end": v(58.6, -16.51) * mm});
            skLineSegment(sketch, "E439", {"start": v(58.6, -16.51) * mm, "end": v(58.68, -16.24) * mm});
            skLineSegment(sketch, "E440", {"start": v(58.68, -16.24) * mm, "end": v(58.76, -15.96) * mm});
            skLineSegment(sketch, "E441", {"start": v(58.76, -15.96) * mm, "end": v(58.74, -15.73) * mm});
            skLineSegment(sketch, "E442", {"start": v(58.74, -15.73) * mm, "end": v(58.59, -15.59) * mm});
            skLineSegment(sketch, "E443", {"start": v(58.59, -15.59) * mm, "end": v(58.4, -15.5) * mm});
            skLineSegment(sketch, "E444", {"start": v(58.4, -15.5) * mm, "end": v(58.21, -15.38) * mm});
            skLineSegment(sketch, "E445", {"start": v(58.21, -15.38) * mm, "end": v(58.05, -15.24) * mm});
            skLineSegment(sketch, "E446", {"start": v(58.05, -15.24) * mm, "end": v(57.9, -15.08) * mm});
            skLineSegment(sketch, "E447", {"start": v(57.9, -15.08) * mm, "end": v(57.76, -14.84) * mm});
            skLineSegment(sketch, "E448", {"start": v(57.76, -14.84) * mm, "end": v(57.68, -14.57) * mm});
            skLineSegment(sketch, "E449", {"start": v(57.68, -14.57) * mm, "end": v(57.66, -14.29) * mm});
            skLineSegment(sketch, "E450", {"start": v(57.66, -14.29) * mm, "end": v(57.7, -14.01) * mm});
            skLineSegment(sketch, "E451", {"start": v(57.7, -14.01) * mm, "end": v(57.8, -13.74) * mm});
            skLineSegment(sketch, "E452", {"start": v(57.8, -13.74) * mm, "end": v(57.94, -13.5) * mm});
            skLineSegment(sketch, "E453", {"start": v(57.94, -13.5) * mm, "end": v(58.13, -13.3) * mm});
            skLineSegment(sketch, "E454", {"start": v(58.13, -13.3) * mm, "end": v(58.36, -13.14) * mm});
            skLineSegment(sketch, "E455", {"start": v(58.36, -13.14) * mm, "end": v(58.57, -13.07) * mm});
            skLineSegment(sketch, "E456", {"start": v(58.57, -13.07) * mm, "end": v(58.78, -13.03) * mm});
            skLineSegment(sketch, "E457", {"start": v(58.78, -13.03) * mm, "end": v(59, -13) * mm});
            skLineSegment(sketch, "E458", {"start": v(59, -13) * mm, "end": v(59.21, -13.02) * mm});
            skLineSegment(sketch, "E459", {"start": v(59.21, -13.02) * mm, "end": v(59.42, -12.95) * mm});
            skLineSegment(sketch, "E460", {"start": v(59.42, -12.95) * mm, "end": v(59.53, -12.76) * mm});
            skLineSegment(sketch, "E461", {"start": v(59.53, -12.76) * mm, "end": v(59.6, -12.48) * mm});
            skLineSegment(sketch, "E462", {"start": v(59.6, -12.48) * mm, "end": v(59.65, -12.2) * mm});
            skLineSegment(sketch, "E463", {"start": v(59.65, -12.2) * mm, "end": v(59.62, -11.98) * mm});
            skLineSegment(sketch, "E464", {"start": v(59.62, -11.98) * mm, "end": v(59.46, -11.84) * mm});
            skLineSegment(sketch, "E465", {"start": v(59.46, -11.84) * mm, "end": v(59.26, -11.76) * mm});
            skLineSegment(sketch, "E466", {"start": v(59.26, -11.76) * mm, "end": v(59.07, -11.66) * mm});
            skLineSegment(sketch, "E467", {"start": v(59.07, -11.66) * mm, "end": v(58.9, -11.53) * mm});
            skLineSegment(sketch, "E468", {"start": v(58.9, -11.53) * mm, "end": v(58.73, -11.38) * mm});
            skLineSegment(sketch, "E469", {"start": v(58.73, -11.38) * mm, "end": v(58.58, -11.14) * mm});
            skLineSegment(sketch, "E470", {"start": v(58.58, -11.14) * mm, "end": v(58.49, -10.88) * mm});
            skLineSegment(sketch, "E471", {"start": v(58.49, -10.88) * mm, "end": v(58.45, -10.6) * mm});
            skLineSegment(sketch, "E472", {"start": v(58.45, -10.6) * mm, "end": v(58.47, -10.32) * mm});
            skLineSegment(sketch, "E473", {"start": v(58.47, -10.32) * mm, "end": v(58.55, -10.05) * mm});
            skLineSegment(sketch, "E474", {"start": v(58.55, -10.05) * mm, "end": v(58.68, -9.8) * mm});
            skLineSegment(sketch, "E475", {"start": v(58.68, -9.8) * mm, "end": v(58.86, -9.59) * mm});
            skLineSegment(sketch, "E476", {"start": v(58.86, -9.59) * mm, "end": v(59.08, -9.42) * mm});
            skLineSegment(sketch, "E477", {"start": v(59.08, -9.42) * mm, "end": v(59.28, -9.33) * mm});
            skLineSegment(sketch, "E478", {"start": v(59.28, -9.33) * mm, "end": v(59.5, -9.27) * mm});
            skLineSegment(sketch, "E479", {"start": v(59.5, -9.27) * mm, "end": v(59.7, -9.24) * mm});
            skLineSegment(sketch, "E480", {"start": v(59.7, -9.24) * mm, "end": v(59.92, -9.24) * mm});
            skLineSegment(sketch, "E481", {"start": v(59.92, -9.24) * mm, "end": v(60.12, -9.16) * mm});
            skLineSegment(sketch, "E482", {"start": v(60.12, -9.16) * mm, "end": v(60.22, -8.96) * mm});
            skLineSegment(sketch, "E483", {"start": v(60.22, -8.96) * mm, "end": v(60.27, -8.68) * mm});
            skLineSegment(sketch, "E484", {"start": v(60.27, -8.68) * mm, "end": v(60.3, -8.4) * mm});
            skLineSegment(sketch, "E485", {"start": v(60.3, -8.4) * mm, "end": v(60.26, -8.17) * mm});
            skLineSegment(sketch, "E486", {"start": v(60.26, -8.17) * mm, "end": v(60.1, -8.04) * mm});
            skLineSegment(sketch, "E487", {"start": v(60.1, -8.04) * mm, "end": v(59.89, -7.98) * mm});
            skLineSegment(sketch, "E488", {"start": v(59.89, -7.98) * mm, "end": v(59.7, -7.89) * mm});
            skLineSegment(sketch, "E489", {"start": v(59.7, -7.89) * mm, "end": v(59.5, -7.77) * mm});
            skLineSegment(sketch, "E490", {"start": v(59.5, -7.77) * mm, "end": v(59.33, -7.63) * mm});
            skLineSegment(sketch, "E491", {"start": v(59.33, -7.63) * mm, "end": v(59.17, -7.4) * mm});
            skLineSegment(sketch, "E492", {"start": v(59.17, -7.4) * mm, "end": v(59.06, -7.15) * mm});
            skLineSegment(sketch, "E493", {"start": v(59.06, -7.15) * mm, "end": v(59, -6.88) * mm});
            skLineSegment(sketch, "E494", {"start": v(59, -6.88) * mm, "end": v(59, -6.6) * mm});
            skLineSegment(sketch, "E495", {"start": v(59, -6.6) * mm, "end": v(59.07, -6.32) * mm});
            skLineSegment(sketch, "E496", {"start": v(59.07, -6.32) * mm, "end": v(59.18, -6.06) * mm});
            skLineSegment(sketch, "E497", {"start": v(59.18, -6.06) * mm, "end": v(59.34, -5.83) * mm});
            skLineSegment(sketch, "E498", {"start": v(59.34, -5.83) * mm, "end": v(59.55, -5.65) * mm});
            skLineSegment(sketch, "E499", {"start": v(59.55, -5.65) * mm, "end": v(59.75, -5.55) * mm});
            skLineSegment(sketch, "E500", {"start": v(59.75, -5.55) * mm, "end": v(59.96, -5.48) * mm});
            skLineSegment(sketch, "E501", {"start": v(59.96, -5.48) * mm, "end": v(60.17, -5.44) * mm});
            skLineSegment(sketch, "E502", {"start": v(60.17, -5.44) * mm, "end": v(60.38, -5.42) * mm});
            skLineSegment(sketch, "E503", {"start": v(60.38, -5.42) * mm, "end": v(60.58, -5.33) * mm});
            skLineSegment(sketch, "E504", {"start": v(60.58, -5.33) * mm, "end": v(60.67, -5.12) * mm});
            skLineSegment(sketch, "E505", {"start": v(60.67, -5.12) * mm, "end": v(60.7, -4.84) * mm});
            skLineSegment(sketch, "E506", {"start": v(60.7, -4.84) * mm, "end": v(60.72, -4.55) * mm});
            skLineSegment(sketch, "E507", {"start": v(60.72, -4.55) * mm, "end": v(60.65, -4.33) * mm});
            skLineSegment(sketch, "E508", {"start": v(60.65, -4.33) * mm, "end": v(60.48, -4.22) * mm});
            skLineSegment(sketch, "E509", {"start": v(60.48, -4.22) * mm, "end": v(60.27, -4.16) * mm});
            skLineSegment(sketch, "E510", {"start": v(60.27, -4.16) * mm, "end": v(60.07, -4.08) * mm});
            skLineSegment(sketch, "E511", {"start": v(60.07, -4.08) * mm, "end": v(59.88, -3.98) * mm});
            skLineSegment(sketch, "E512", {"start": v(59.88, -3.98) * mm, "end": v(59.7, -3.85) * mm});
            skLineSegment(sketch, "E513", {"start": v(59.7, -3.85) * mm, "end": v(59.52, -3.64) * mm});
            skLineSegment(sketch, "E514", {"start": v(59.52, -3.64) * mm, "end": v(59.4, -3.4) * mm});
            skLineSegment(sketch, "E515", {"start": v(59.4, -3.4) * mm, "end": v(59.32, -3.12) * mm});
            skLineSegment(sketch, "E516", {"start": v(59.32, -3.12) * mm, "end": v(59.3, -2.84) * mm});
            skLineSegment(sketch, "E517", {"start": v(59.3, -2.84) * mm, "end": v(59.35, -2.56) * mm});
            skLineSegment(sketch, "E518", {"start": v(59.35, -2.56) * mm, "end": v(59.45, -2.3) * mm});
            skLineSegment(sketch, "E519", {"start": v(59.45, -2.3) * mm, "end": v(59.6, -2.06) * mm});
            skLineSegment(sketch, "E520", {"start": v(59.6, -2.06) * mm, "end": v(59.8, -1.86) * mm});
            skLineSegment(sketch, "E521", {"start": v(59.8, -1.86) * mm, "end": v(59.98, -1.75) * mm});
            skLineSegment(sketch, "E522", {"start": v(59.98, -1.75) * mm, "end": v(60.19, -1.67) * mm});
            skLineSegment(sketch, "E523", {"start": v(60.19, -1.67) * mm, "end": v(60.4, -1.6) * mm});
            skLineSegment(sketch, "E524", {"start": v(60.4, -1.6) * mm, "end": v(60.6, -1.58) * mm});
            skLineSegment(sketch, "E525", {"start": v(60.6, -1.58) * mm, "end": v(60.8, -1.48) * mm});
            skLineSegment(sketch, "E526", {"start": v(60.8, -1.48) * mm, "end": v(60.87, -1.26) * mm});
            skLineSegment(sketch, "E527", {"start": v(60.87, -1.26) * mm, "end": v(60.88, -0.98) * mm});
            skLineSegment(sketch, "E528", {"start": v(60.88, -0.98) * mm, "end": v(60.88, -0.7) * mm});
            skLineSegment(sketch, "E529", {"start": v(60.88, -0.7) * mm, "end": v(60.8, -0.48) * mm});
            skLineSegment(sketch, "E530", {"start": v(60.8, -0.48) * mm, "end": v(60.62, -0.37) * mm});
            skLineSegment(sketch, "E531", {"start": v(60.62, -0.37) * mm, "end": v(60.41, -0.33) * mm});
            skLineSegment(sketch, "E532", {"start": v(60.41, -0.33) * mm, "end": v(60.2, -0.27) * mm});
            skLineSegment(sketch, "E533", {"start": v(60.2, -0.27) * mm, "end": v(60, -0.17) * mm});
            skLineSegment(sketch, "E534", {"start": v(60, -0.17) * mm, "end": v(59.82, -0.06) * mm});
            skLineSegment(sketch, "E535", {"start": v(59.82, -0.06) * mm, "end": v(59.63, 0.14) * mm});
            skLineSegment(sketch, "E536", {"start": v(59.63, 0.14) * mm, "end": v(59.49, 0.38) * mm});
            skLineSegment(sketch, "E537", {"start": v(59.49, 0.38) * mm, "end": v(59.4, 0.65) * mm});
            skLineSegment(sketch, "E538", {"start": v(59.4, 0.65) * mm, "end": v(59.37, 0.93) * mm});
            skLineSegment(sketch, "E539", {"start": v(59.37, 0.93) * mm, "end": v(59.4, 1.21) * mm});
            skLineSegment(sketch, "E540", {"start": v(59.4, 1.21) * mm, "end": v(59.47, 1.48) * mm});
            skLineSegment(sketch, "E541", {"start": v(59.47, 1.48) * mm, "end": v(59.6, 1.73) * mm});
            skLineSegment(sketch, "E542", {"start": v(59.6, 1.73) * mm, "end": v(59.79, 1.93) * mm});
            skLineSegment(sketch, "E543", {"start": v(59.79, 1.93) * mm, "end": v(59.97, 2.05) * mm});
            skLineSegment(sketch, "E544", {"start": v(59.97, 2.05) * mm, "end": v(60.17, 2.15) * mm});
            skLineSegment(sketch, "E545", {"start": v(60.17, 2.15) * mm, "end": v(60.37, 2.22) * mm});
            skLineSegment(sketch, "E546", {"start": v(60.37, 2.22) * mm, "end": v(60.58, 2.27) * mm});
            skLineSegment(sketch, "E547", {"start": v(60.58, 2.27) * mm, "end": v(60.76, 2.38) * mm});
            skLineSegment(sketch, "E548", {"start": v(60.76, 2.38) * mm, "end": v(60.83, 2.6) * mm});
            skLineSegment(sketch, "E549", {"start": v(60.83, 2.6) * mm, "end": v(60.82, 2.89) * mm});
            skLineSegment(sketch, "E550", {"start": v(60.82, 2.89) * mm, "end": v(60.8, 3.17) * mm});
            skLineSegment(sketch, "E551", {"start": v(60.8, 3.17) * mm, "end": v(60.71, 3.38) * mm});
            skLineSegment(sketch, "E552", {"start": v(60.71, 3.38) * mm, "end": v(60.52, 3.47) * mm});
            skLineSegment(sketch, "E553", {"start": v(60.52, 3.47) * mm, "end": v(60.31, 3.5) * mm});
            skLineSegment(sketch, "E554", {"start": v(60.31, 3.5) * mm, "end": v(60.1, 3.55) * mm});
            skLineSegment(sketch, "E555", {"start": v(60.1, 3.55) * mm, "end": v(59.9, 3.63) * mm});
            skLineSegment(sketch, "E556", {"start": v(59.9, 3.63) * mm, "end": v(59.7, 3.73) * mm});
            skLineSegment(sketch, "E557", {"start": v(59.7, 3.73) * mm, "end": v(59.5, 3.92) * mm});
            skLineSegment(sketch, "E558", {"start": v(59.5, 3.92) * mm, "end": v(59.34, 4.16) * mm});
            skLineSegment(sketch, "E559", {"start": v(59.34, 4.16) * mm, "end": v(59.24, 4.42) * mm});
            skLineSegment(sketch, "E560", {"start": v(59.24, 4.42) * mm, "end": v(59.19, 4.7) * mm});
            skLineSegment(sketch, "E561", {"start": v(59.19, 4.7) * mm, "end": v(59.2, 4.98) * mm});
            skLineSegment(sketch, "E562", {"start": v(59.2, 4.98) * mm, "end": v(59.26, 5.25) * mm});
            skLineSegment(sketch, "E563", {"start": v(59.26, 5.25) * mm, "end": v(59.37, 5.5) * mm});
            skLineSegment(sketch, "E564", {"start": v(59.37, 5.5) * mm, "end": v(59.55, 5.72) * mm});
            skLineSegment(sketch, "E565", {"start": v(59.55, 5.72) * mm, "end": v(59.72, 5.85) * mm});
            skLineSegment(sketch, "E566", {"start": v(59.72, 5.85) * mm, "end": v(59.91, 5.96) * mm});
            skLineSegment(sketch, "E567", {"start": v(59.91, 5.96) * mm, "end": v(60.1, 6.05) * mm});
            skLineSegment(sketch, "E568", {"start": v(60.1, 6.05) * mm, "end": v(60.31, 6.1) * mm});
            skLineSegment(sketch, "E569", {"start": v(60.31, 6.1) * mm, "end": v(60.49, 6.23) * mm});
            skLineSegment(sketch, "E570", {"start": v(60.49, 6.23) * mm, "end": v(60.54, 6.45) * mm});
            skLineSegment(sketch, "E571", {"start": v(60.54, 6.45) * mm, "end": v(60.51, 6.74) * mm});
            skLineSegment(sketch, "E572", {"start": v(60.51, 6.74) * mm, "end": v(60.48, 7.02) * mm});
            skLineSegment(sketch, "E573", {"start": v(60.48, 7.02) * mm, "end": v(60.38, 7.22) * mm});
            skLineSegment(sketch, "E574", {"start": v(60.38, 7.22) * mm, "end": v(60.18, 7.3) * mm});
            skLineSegment(sketch, "E575", {"start": v(60.18, 7.3) * mm, "end": v(59.97, 7.32) * mm});
            skLineSegment(sketch, "E576", {"start": v(59.97, 7.32) * mm, "end": v(59.76, 7.36) * mm});
            skLineSegment(sketch, "E577", {"start": v(59.76, 7.36) * mm, "end": v(59.55, 7.42) * mm});
            skLineSegment(sketch, "E578", {"start": v(59.55, 7.42) * mm, "end": v(59.35, 7.51) * mm});
            skLineSegment(sketch, "E579", {"start": v(59.35, 7.51) * mm, "end": v(59.13, 7.7) * mm});
            skLineSegment(sketch, "E580", {"start": v(59.13, 7.7) * mm, "end": v(58.96, 7.91) * mm});
            skLineSegment(sketch, "E581", {"start": v(58.96, 7.91) * mm, "end": v(58.84, 8.16) * mm});
            skLineSegment(sketch, "E582", {"start": v(58.84, 8.16) * mm, "end": v(58.77, 8.44) * mm});
            skLineSegment(sketch, "E583", {"start": v(58.77, 8.44) * mm, "end": v(58.76, 8.72) * mm});
            skLineSegment(sketch, "E584", {"start": v(58.76, 8.72) * mm, "end": v(58.8, 9) * mm});
            skLineSegment(sketch, "E585", {"start": v(58.8, 9) * mm, "end": v(58.9, 9.26) * mm});
            skLineSegment(sketch, "E586", {"start": v(58.9, 9.26) * mm, "end": v(59.06, 9.49) * mm});
            skLineSegment(sketch, "E587", {"start": v(59.06, 9.49) * mm, "end": v(59.23, 9.63) * mm});
            skLineSegment(sketch, "E588", {"start": v(59.23, 9.63) * mm, "end": v(59.41, 9.75) * mm});
            skLineSegment(sketch, "E589", {"start": v(59.41, 9.75) * mm, "end": v(59.6, 9.85) * mm});
            skLineSegment(sketch, "E590", {"start": v(59.6, 9.85) * mm, "end": v(59.8, 9.92) * mm});
            skLineSegment(sketch, "E591", {"start": v(59.8, 9.92) * mm, "end": v(59.97, 10.06) * mm});
            skLineSegment(sketch, "E592", {"start": v(59.97, 10.06) * mm, "end": v(60, 10.28) * mm});
            skLineSegment(sketch, "E593", {"start": v(60, 10.28) * mm, "end": v(59.96, 10.56) * mm});
            skLineSegment(sketch, "E594", {"start": v(59.96, 10.56) * mm, "end": v(59.9, 10.84) * mm});
            skLineSegment(sketch, "E595", {"start": v(59.9, 10.84) * mm, "end": v(59.8, 11.04) * mm});
            skLineSegment(sketch, "E596", {"start": v(59.8, 11.04) * mm, "end": v(59.6, 11.1) * mm});
            skLineSegment(sketch, "E597", {"start": v(59.6, 11.1) * mm, "end": v(59.38, 11.1) * mm});
            skLineSegment(sketch, "E598", {"start": v(59.38, 11.1) * mm, "end": v(59.17, 11.13) * mm});
            skLineSegment(sketch, "E599", {"start": v(59.17, 11.13) * mm, "end": v(58.96, 11.19) * mm});
            skLineSegment(sketch, "E600", {"start": v(58.96, 11.19) * mm, "end": v(58.75, 11.26) * mm});
            skLineSegment(sketch, "E601", {"start": v(58.75, 11.26) * mm, "end": v(58.52, 11.42) * mm});
            skLineSegment(sketch, "E602", {"start": v(58.52, 11.42) * mm, "end": v(58.34, 11.63) * mm});
            skLineSegment(sketch, "E603", {"start": v(58.34, 11.63) * mm, "end": v(58.2, 11.88) * mm});
            skLineSegment(sketch, "E604", {"start": v(58.2, 11.88) * mm, "end": v(58.12, 12.15) * mm});
            skLineSegment(sketch, "E605", {"start": v(58.12, 12.15) * mm, "end": v(58.09, 12.43) * mm});
            skLineSegment(sketch, "E606", {"start": v(58.09, 12.43) * mm, "end": v(58.11, 12.7) * mm});
            skLineSegment(sketch, "E607", {"start": v(58.11, 12.7) * mm, "end": v(58.2, 12.97) * mm});
            skLineSegment(sketch, "E608", {"start": v(58.2, 12.97) * mm, "end": v(58.34, 13.21) * mm});
            skLineSegment(sketch, "E609", {"start": v(58.34, 13.21) * mm, "end": v(58.5, 13.37) * mm});
            skLineSegment(sketch, "E610", {"start": v(58.5, 13.37) * mm, "end": v(58.67, 13.5) * mm});
            skLineSegment(sketch, "E611", {"start": v(58.67, 13.5) * mm, "end": v(58.86, 13.6) * mm});
            skLineSegment(sketch, "E612", {"start": v(58.86, 13.6) * mm, "end": v(59.05, 13.7) * mm});
            skLineSegment(sketch, "E613", {"start": v(59.05, 13.7) * mm, "end": v(59.21, 13.84) * mm});
            skLineSegment(sketch, "E614", {"start": v(59.21, 13.84) * mm, "end": v(59.24, 14.06) * mm});
            skLineSegment(sketch, "E615", {"start": v(59.24, 14.06) * mm, "end": v(59.17, 14.34) * mm});
            skLineSegment(sketch, "E616", {"start": v(59.17, 14.34) * mm, "end": v(59.1, 14.62) * mm});
            skLineSegment(sketch, "E617", {"start": v(59.1, 14.62) * mm, "end": v(58.97, 14.8) * mm});
            skLineSegment(sketch, "E618", {"start": v(58.97, 14.8) * mm, "end": v(58.77, 14.87) * mm});
            skLineSegment(sketch, "E619", {"start": v(58.77, 14.87) * mm, "end": v(58.56, 14.85) * mm});
            skLineSegment(sketch, "E620", {"start": v(58.56, 14.85) * mm, "end": v(58.34, 14.86) * mm});
            skLineSegment(sketch, "E621", {"start": v(58.34, 14.86) * mm, "end": v(58.13, 14.9) * mm});
            skLineSegment(sketch, "E622", {"start": v(58.13, 14.9) * mm, "end": v(57.92, 14.97) * mm});
            skLineSegment(sketch, "E623", {"start": v(57.92, 14.97) * mm, "end": v(57.68, 15.11) * mm});
            skLineSegment(sketch, "E624", {"start": v(57.68, 15.11) * mm, "end": v(57.48, 15.31) * mm});
            skLineSegment(sketch, "E625", {"start": v(57.48, 15.31) * mm, "end": v(57.33, 15.55) * mm});
            skLineSegment(sketch, "E626", {"start": v(57.33, 15.55) * mm, "end": v(57.23, 15.8) * mm});
            skLineSegment(sketch, "E627", {"start": v(57.23, 15.8) * mm, "end": v(57.18, 16.09) * mm});
            skLineSegment(sketch, "E628", {"start": v(57.18, 16.09) * mm, "end": v(57.19, 16.37) * mm});
            skLineSegment(sketch, "E629", {"start": v(57.19, 16.37) * mm, "end": v(57.26, 16.64) * mm});
            skLineSegment(sketch, "E630", {"start": v(57.26, 16.64) * mm, "end": v(57.38, 16.89) * mm});
            skLineSegment(sketch, "E631", {"start": v(57.38, 16.89) * mm, "end": v(57.53, 17.05) * mm});
            skLineSegment(sketch, "E632", {"start": v(57.53, 17.05) * mm, "end": v(57.7, 17.2) * mm});
            skLineSegment(sketch, "E633", {"start": v(57.7, 17.2) * mm, "end": v(57.88, 17.31) * mm});
            skLineSegment(sketch, "E634", {"start": v(57.88, 17.31) * mm, "end": v(58.07, 17.41) * mm});
            skLineSegment(sketch, "E635", {"start": v(58.07, 17.41) * mm, "end": v(58.21, 17.57) * mm});
            skLineSegment(sketch, "E636", {"start": v(58.21, 17.57) * mm, "end": v(58.22, 17.8) * mm});
            skLineSegment(sketch, "E637", {"start": v(58.22, 17.8) * mm, "end": v(58.14, 18.07) * mm});
            skLineSegment(sketch, "E638", {"start": v(58.14, 18.07) * mm, "end": v(58.05, 18.34) * mm});
            skLineSegment(sketch, "E639", {"start": v(58.05, 18.34) * mm, "end": v(57.92, 18.52) * mm});
            skLineSegment(sketch, "E640", {"start": v(57.92, 18.52) * mm, "end": v(57.7, 18.56) * mm});
            skLineSegment(sketch, "E641", {"start": v(57.7, 18.56) * mm, "end": v(57.5, 18.54) * mm});
            skLineSegment(sketch, "E642", {"start": v(57.5, 18.54) * mm, "end": v(57.28, 18.53) * mm});
            skLineSegment(sketch, "E643", {"start": v(57.28, 18.53) * mm, "end": v(57.06, 18.56) * mm});
            skLineSegment(sketch, "E644", {"start": v(57.06, 18.56) * mm, "end": v(56.85, 18.6) * mm});
            skLineSegment(sketch, "E645", {"start": v(56.85, 18.6) * mm, "end": v(56.6, 18.74) * mm});
            skLineSegment(sketch, "E646", {"start": v(56.6, 18.74) * mm, "end": v(56.4, 18.93) * mm});
            skLineSegment(sketch, "E647", {"start": v(56.4, 18.93) * mm, "end": v(56.23, 19.15) * mm});
            skLineSegment(sketch, "E648", {"start": v(56.23, 19.15) * mm, "end": v(56.1, 19.4) * mm});
            skLineSegment(sketch, "E649", {"start": v(56.1, 19.4) * mm, "end": v(56.04, 19.68) * mm});
            skLineSegment(sketch, "E650", {"start": v(56.04, 19.68) * mm, "end": v(56.04, 19.96) * mm});
            skLineSegment(sketch, "E651", {"start": v(56.04, 19.96) * mm, "end": v(56.09, 20.24) * mm});
            skLineSegment(sketch, "E652", {"start": v(56.09, 20.24) * mm, "end": v(56.2, 20.5) * mm});
            skLineSegment(sketch, "E653", {"start": v(56.2, 20.5) * mm, "end": v(56.34, 20.67) * mm});
            skLineSegment(sketch, "E654", {"start": v(56.34, 20.67) * mm, "end": v(56.49, 20.82) * mm});
            skLineSegment(sketch, "E655", {"start": v(56.49, 20.82) * mm, "end": v(56.66, 20.95) * mm});
            skLineSegment(sketch, "E656", {"start": v(56.66, 20.95) * mm, "end": v(56.84, 21.06) * mm});
            skLineSegment(sketch, "E657", {"start": v(56.84, 21.06) * mm, "end": v(56.98, 21.22) * mm});
            skLineSegment(sketch, "E658", {"start": v(56.98, 21.22) * mm, "end": v(56.98, 21.45) * mm});
            skLineSegment(sketch, "E659", {"start": v(56.98, 21.45) * mm, "end": v(56.88, 21.72) * mm});
            skLineSegment(sketch, "E660", {"start": v(56.88, 21.72) * mm, "end": v(56.77, 21.98) * mm});
            skLineSegment(sketch, "E661", {"start": v(56.77, 21.98) * mm, "end": v(56.62, 22.15) * mm});
            skLineSegment(sketch, "E662", {"start": v(56.62, 22.15) * mm, "end": v(56.41, 22.19) * mm});
            skLineSegment(sketch, "E663", {"start": v(56.41, 22.19) * mm, "end": v(56.2, 22.14) * mm});
            skLineSegment(sketch, "E664", {"start": v(56.2, 22.14) * mm, "end": v(55.99, 22.13) * mm});
            skLineSegment(sketch, "E665", {"start": v(55.99, 22.13) * mm, "end": v(55.77, 22.14) * mm});
            skLineSegment(sketch, "E666", {"start": v(55.77, 22.14) * mm, "end": v(55.55, 22.18) * mm});
            skLineSegment(sketch, "E667", {"start": v(55.55, 22.18) * mm, "end": v(55.3, 22.3) * mm});
            skLineSegment(sketch, "E668", {"start": v(55.3, 22.3) * mm, "end": v(55.08, 22.46) * mm});
            skLineSegment(sketch, "E669", {"start": v(55.08, 22.46) * mm, "end": v(54.9, 22.68) * mm});
            skLineSegment(sketch, "E670", {"start": v(54.9, 22.68) * mm, "end": v(54.76, 22.93) * mm});
            skLineSegment(sketch, "E671", {"start": v(54.76, 22.93) * mm, "end": v(54.68, 23.2) * mm});
            skLineSegment(sketch, "E672", {"start": v(54.68, 23.2) * mm, "end": v(54.66, 23.48) * mm});
            skLineSegment(sketch, "E673", {"start": v(54.66, 23.48) * mm, "end": v(54.69, 23.75) * mm});
            skLineSegment(sketch, "E674", {"start": v(54.69, 23.75) * mm, "end": v(54.78, 24.02) * mm});
            skLineSegment(sketch, "E675", {"start": v(54.78, 24.02) * mm, "end": v(54.91, 24.2) * mm});
            skLineSegment(sketch, "E676", {"start": v(54.91, 24.2) * mm, "end": v(55.06, 24.36) * mm});
            skLineSegment(sketch, "E677", {"start": v(55.06, 24.36) * mm, "end": v(55.22, 24.5) * mm});
            skLineSegment(sketch, "E678", {"start": v(55.22, 24.5) * mm, "end": v(55.4, 24.62) * mm});
            skLineSegment(sketch, "E679", {"start": v(55.4, 24.62) * mm, "end": v(55.52, 24.8) * mm});
            skLineSegment(sketch, "E680", {"start": v(55.52, 24.8) * mm, "end": v(55.5, 25.02) * mm});
            skLineSegment(sketch, "E681", {"start": v(55.5, 25.02) * mm, "end": v(55.38, 25.28) * mm});
            skLineSegment(sketch, "E682", {"start": v(55.38, 25.28) * mm, "end": v(55.26, 25.54) * mm});
            skLineSegment(sketch, "E683", {"start": v(55.26, 25.54) * mm, "end": v(55.1, 25.7) * mm});
            skLineSegment(sketch, "E684", {"start": v(55.1, 25.7) * mm, "end": v(54.9, 25.72) * mm});
            skLineSegment(sketch, "E685", {"start": v(54.9, 25.72) * mm, "end": v(54.69, 25.66) * mm});
            skLineSegment(sketch, "E686", {"start": v(54.69, 25.66) * mm, "end": v(54.47, 25.64) * mm});
            skLineSegment(sketch, "E687", {"start": v(54.47, 25.64) * mm, "end": v(54.25, 25.63) * mm});
            skLineSegment(sketch, "E688", {"start": v(54.25, 25.63) * mm, "end": v(54.03, 25.66) * mm});
            skLineSegment(sketch, "E689", {"start": v(54.03, 25.66) * mm, "end": v(53.77, 25.76) * mm});
            skLineSegment(sketch, "E690", {"start": v(53.77, 25.76) * mm, "end": v(53.54, 25.91) * mm});
            skLineSegment(sketch, "E691", {"start": v(53.54, 25.91) * mm, "end": v(53.35, 26.12) * mm});
            skLineSegment(sketch, "E692", {"start": v(53.35, 26.12) * mm, "end": v(53.2, 26.35) * mm});
            skLineSegment(sketch, "E693", {"start": v(53.2, 26.35) * mm, "end": v(53.1, 26.62) * mm});
            skLineSegment(sketch, "E694", {"start": v(53.1, 26.62) * mm, "end": v(53.06, 26.9) * mm});
            skLineSegment(sketch, "E695", {"start": v(53.06, 26.9) * mm, "end": v(53.07, 27.17) * mm});
            skLineSegment(sketch, "E696", {"start": v(53.07, 27.17) * mm, "end": v(53.15, 27.44) * mm});
            skLineSegment(sketch, "E697", {"start": v(53.15, 27.44) * mm, "end": v(53.26, 27.63) * mm});
            skLineSegment(sketch, "E698", {"start": v(53.26, 27.63) * mm, "end": v(53.4, 27.8) * mm});
            skLineSegment(sketch, "E699", {"start": v(53.4, 27.8) * mm, "end": v(53.55, 27.95) * mm});
            skLineSegment(sketch, "E700", {"start": v(53.55, 27.95) * mm, "end": v(53.72, 28.09) * mm});
            skLineSegment(sketch, "E701", {"start": v(53.72, 28.09) * mm, "end": v(53.83, 28.27) * mm});
            skLineSegment(sketch, "E702", {"start": v(53.83, 28.27) * mm, "end": v(53.8, 28.49) * mm});
            skLineSegment(sketch, "E703", {"start": v(53.8, 28.49) * mm, "end": v(53.67, 28.74) * mm});
            skLineSegment(sketch, "E704", {"start": v(53.67, 28.74) * mm, "end": v(53.53, 29) * mm});
            skLineSegment(sketch, "E705", {"start": v(53.53, 29) * mm, "end": v(53.36, 29.14) * mm});
            skLineSegment(sketch, "E706", {"start": v(53.36, 29.14) * mm, "end": v(53.15, 29.15) * mm});
            skLineSegment(sketch, "E707", {"start": v(53.15, 29.15) * mm, "end": v(52.95, 29.08) * mm});
            skLineSegment(sketch, "E708", {"start": v(52.95, 29.08) * mm, "end": v(52.74, 29.04) * mm});
            skLineSegment(sketch, "E709", {"start": v(52.74, 29.04) * mm, "end": v(52.52, 29.02) * mm});
            skLineSegment(sketch, "E710", {"start": v(52.52, 29.02) * mm, "end": v(52.3, 29.03) * mm});
            skLineSegment(sketch, "E711", {"start": v(52.3, 29.03) * mm, "end": v(52.03, 29.11) * mm});
            skLineSegment(sketch, "E712", {"start": v(52.03, 29.11) * mm, "end": v(51.8, 29.26) * mm});
            skLineSegment(sketch, "E713", {"start": v(51.8, 29.26) * mm, "end": v(51.59, 29.45) * mm});
            skLineSegment(sketch, "E714", {"start": v(51.59, 29.45) * mm, "end": v(51.42, 29.68) * mm});
            skLineSegment(sketch, "E715", {"start": v(51.42, 29.68) * mm, "end": v(51.3, 29.93) * mm});
            skLineSegment(sketch, "E716", {"start": v(51.3, 29.93) * mm, "end": v(51.24, 30.2) * mm});
            skLineSegment(sketch, "E717", {"start": v(51.24, 30.2) * mm, "end": v(51.24, 30.48) * mm});
            skLineSegment(sketch, "E718", {"start": v(51.24, 30.48) * mm, "end": v(51.3, 30.76) * mm});
            skLineSegment(sketch, "E719", {"start": v(51.3, 30.76) * mm, "end": v(51.4, 30.95) * mm});
            skLineSegment(sketch, "E720", {"start": v(51.4, 30.95) * mm, "end": v(51.53, 31.13) * mm});
            skLineSegment(sketch, "E721", {"start": v(51.53, 31.13) * mm, "end": v(51.67, 31.3) * mm});
            skLineSegment(sketch, "E722", {"start": v(51.67, 31.3) * mm, "end": v(51.83, 31.44) * mm});
            skLineSegment(sketch, "E723", {"start": v(51.83, 31.44) * mm, "end": v(51.93, 31.62) * mm});
            skLineSegment(sketch, "E724", {"start": v(51.93, 31.62) * mm, "end": v(51.89, 31.84) * mm});
            skLineSegment(sketch, "E725", {"start": v(51.89, 31.84) * mm, "end": v(51.74, 32.09) * mm});
            skLineSegment(sketch, "E726", {"start": v(51.74, 32.09) * mm, "end": v(51.58, 32.33) * mm});
            skLineSegment(sketch, "E727", {"start": v(51.58, 32.33) * mm, "end": v(51.4, 32.47) * mm});
            skLineSegment(sketch, "E728", {"start": v(51.4, 32.47) * mm, "end": v(51.2, 32.46) * mm});
            skLineSegment(sketch, "E729", {"start": v(51.2, 32.46) * mm, "end": v(51, 32.38) * mm});
            skLineSegment(sketch, "E730", {"start": v(51, 32.38) * mm, "end": v(50.79, 32.33) * mm});
            skLineSegment(sketch, "E731", {"start": v(50.79, 32.33) * mm, "end": v(50.57, 32.3) * mm});
            skLineSegment(sketch, "E732", {"start": v(50.57, 32.3) * mm, "end": v(50.35, 32.29) * mm});
            skLineSegment(sketch, "E733", {"start": v(50.35, 32.29) * mm, "end": v(50.08, 32.36) * mm});
            skLineSegment(sketch, "E734", {"start": v(50.08, 32.36) * mm, "end": v(49.83, 32.48) * mm});
            skLineSegment(sketch, "E735", {"start": v(49.83, 32.48) * mm, "end": v(49.61, 32.66) * mm});
            skLineSegment(sketch, "E736", {"start": v(49.61, 32.66) * mm, "end": v(49.43, 32.88) * mm});
            skLineSegment(sketch, "E737", {"start": v(49.43, 32.88) * mm, "end": v(49.3, 33.13) * mm});
            skLineSegment(sketch, "E738", {"start": v(49.3, 33.13) * mm, "end": v(49.22, 33.4) * mm});
            skLineSegment(sketch, "E739", {"start": v(49.22, 33.4) * mm, "end": v(49.2, 33.67) * mm});
            skLineSegment(sketch, "E740", {"start": v(49.2, 33.67) * mm, "end": v(49.25, 33.95) * mm});
            skLineSegment(sketch, "E741", {"start": v(49.25, 33.95) * mm, "end": v(49.34, 34.15) * mm});
            skLineSegment(sketch, "E742", {"start": v(49.34, 34.15) * mm, "end": v(49.45, 34.34) * mm});
            skLineSegment(sketch, "E743", {"start": v(49.45, 34.34) * mm, "end": v(49.58, 34.5) * mm});
            skLineSegment(sketch, "E744", {"start": v(49.58, 34.5) * mm, "end": v(49.73, 34.66) * mm});
            skLineSegment(sketch, "E745", {"start": v(49.73, 34.66) * mm, "end": v(49.82, 34.85) * mm});
            skLineSegment(sketch, "E746", {"start": v(49.82, 34.85) * mm, "end": v(49.76, 35.07) * mm});
            skLineSegment(sketch, "E747", {"start": v(49.76, 35.07) * mm, "end": v(49.6, 35.3) * mm});
            skLineSegment(sketch, "E748", {"start": v(49.6, 35.3) * mm, "end": v(49.43, 35.54) * mm});
            skLineSegment(sketch, "E749", {"start": v(49.43, 35.54) * mm, "end": v(49.24, 35.67) * mm});
            skLineSegment(sketch, "E750", {"start": v(49.24, 35.67) * mm, "end": v(49.03, 35.64) * mm});
            skLineSegment(sketch, "E751", {"start": v(49.03, 35.64) * mm, "end": v(48.84, 35.55) * mm});
            skLineSegment(sketch, "E752", {"start": v(48.84, 35.55) * mm, "end": v(48.63, 35.48) * mm});
            skLineSegment(sketch, "E753", {"start": v(48.63, 35.48) * mm, "end": v(48.42, 35.44) * mm});
            skLineSegment(sketch, "E754", {"start": v(48.42, 35.44) * mm, "end": v(48.2, 35.42) * mm});
            skLineSegment(sketch, "E755", {"start": v(48.2, 35.42) * mm, "end": v(47.93, 35.47) * mm});
            skLineSegment(sketch, "E756", {"start": v(47.93, 35.47) * mm, "end": v(47.67, 35.58) * mm});
            skLineSegment(sketch, "E757", {"start": v(47.67, 35.58) * mm, "end": v(47.44, 35.74) * mm});
            skLineSegment(sketch, "E758", {"start": v(47.44, 35.74) * mm, "end": v(47.25, 35.95) * mm});
            skLineSegment(sketch, "E759", {"start": v(47.25, 35.95) * mm, "end": v(47.1, 36.19) * mm});
            skLineSegment(sketch, "E760", {"start": v(47.1, 36.19) * mm, "end": v(47, 36.45) * mm});
            skLineSegment(sketch, "E761", {"start": v(47, 36.45) * mm, "end": v(46.97, 36.73) * mm});
            skLineSegment(sketch, "E762", {"start": v(46.97, 36.73) * mm, "end": v(47, 37) * mm});
            skLineSegment(sketch, "E763", {"start": v(47, 37) * mm, "end": v(47.07, 37.21) * mm});
            skLineSegment(sketch, "E764", {"start": v(47.07, 37.21) * mm, "end": v(47.17, 37.4) * mm});
            skLineSegment(sketch, "E765", {"start": v(47.17, 37.4) * mm, "end": v(47.29, 37.58) * mm});
            skLineSegment(sketch, "E766", {"start": v(47.29, 37.58) * mm, "end": v(47.43, 37.75) * mm});
            skLineSegment(sketch, "E767", {"start": v(47.43, 37.75) * mm, "end": v(47.5, 37.94) * mm});
            skLineSegment(sketch, "E768", {"start": v(47.5, 37.94) * mm, "end": v(47.44, 38.16) * mm});
            skLineSegment(sketch, "E769", {"start": v(47.44, 38.16) * mm, "end": v(47.26, 38.38) * mm});
            skLineSegment(sketch, "E770", {"start": v(47.26, 38.38) * mm, "end": v(47.07, 38.6) * mm});
            skLineSegment(sketch, "E771", {"start": v(47.07, 38.6) * mm, "end": v(46.88, 38.72) * mm});
            skLineSegment(sketch, "E772", {"start": v(46.88, 38.72) * mm, "end": v(46.67, 38.68) * mm});
            skLineSegment(sketch, "E773", {"start": v(46.67, 38.68) * mm, "end": v(46.48, 38.58) * mm});
            skLineSegment(sketch, "E774", {"start": v(46.48, 38.58) * mm, "end": v(46.28, 38.5) * mm});
            skLineSegment(sketch, "E775", {"start": v(46.28, 38.5) * mm, "end": v(46.07, 38.44) * mm});
            skLineSegment(sketch, "E776", {"start": v(46.07, 38.44) * mm, "end": v(45.86, 38.4) * mm});
            skLineSegment(sketch, "E777", {"start": v(45.86, 38.4) * mm, "end": v(45.58, 38.44) * mm});
            skLineSegment(sketch, "E778", {"start": v(45.58, 38.44) * mm, "end": v(45.32, 38.53) * mm});
            skLineSegment(sketch, "E779", {"start": v(45.32, 38.53) * mm, "end": v(45.08, 38.68) * mm});
            skLineSegment(sketch, "E780", {"start": v(45.08, 38.68) * mm, "end": v(44.87, 38.87) * mm});
            skLineSegment(sketch, "E781", {"start": v(44.87, 38.87) * mm, "end": v(44.7, 39.1) * mm});
            skLineSegment(sketch, "E782", {"start": v(44.7, 39.1) * mm, "end": v(44.6, 39.36) * mm});
            skLineSegment(sketch, "E783", {"start": v(44.6, 39.36) * mm, "end": v(44.54, 39.63) * mm});
            skLineSegment(sketch, "E784", {"start": v(44.54, 39.63) * mm, "end": v(44.55, 39.91) * mm});
            skLineSegment(sketch, "E785", {"start": v(44.55, 39.91) * mm, "end": v(44.61, 40.12) * mm});
            skLineSegment(sketch, "E786", {"start": v(44.61, 40.12) * mm, "end": v(44.7, 40.32) * mm});
            skLineSegment(sketch, "E787", {"start": v(44.7, 40.32) * mm, "end": v(44.81, 40.5) * mm});
            skLineSegment(sketch, "E788", {"start": v(44.81, 40.5) * mm, "end": v(44.94, 40.68) * mm});
            skLineSegment(sketch, "E789", {"start": v(44.94, 40.68) * mm, "end": v(45, 40.88) * mm});
            skLineSegment(sketch, "E790", {"start": v(45, 40.88) * mm, "end": v(44.92, 41.09) * mm});
            skLineSegment(sketch, "E791", {"start": v(44.92, 41.09) * mm, "end": v(44.73, 41.3) * mm});
            skLineSegment(sketch, "E792", {"start": v(44.73, 41.3) * mm, "end": v(44.53, 41.5) * mm});
            skLineSegment(sketch, "E793", {"start": v(44.53, 41.5) * mm, "end": v(44.33, 41.61) * mm});
            skLineSegment(sketch, "E794", {"start": v(44.33, 41.61) * mm, "end": v(44.12, 41.56) * mm});
            skLineSegment(sketch, "E795", {"start": v(44.12, 41.56) * mm, "end": v(43.94, 41.45) * mm});
            skLineSegment(sketch, "E796", {"start": v(43.94, 41.45) * mm, "end": v(43.75, 41.35) * mm});
            skLineSegment(sketch, "E797", {"start": v(43.75, 41.35) * mm, "end": v(43.54, 41.28) * mm});
            skLineSegment(sketch, "E798", {"start": v(43.54, 41.28) * mm, "end": v(43.33, 41.23) * mm});
            skLineSegment(sketch, "E799", {"start": v(43.33, 41.23) * mm, "end": v(43.05, 41.25) * mm});
            skLineSegment(sketch, "E800", {"start": v(43.05, 41.25) * mm, "end": v(42.78, 41.33) * mm});
            skLineSegment(sketch, "E801", {"start": v(42.78, 41.33) * mm, "end": v(42.53, 41.46) * mm});
            skLineSegment(sketch, "E802", {"start": v(42.53, 41.46) * mm, "end": v(42.32, 41.64) * mm});
            skLineSegment(sketch, "E803", {"start": v(42.32, 41.64) * mm, "end": v(42.14, 41.86) * mm});
            skLineSegment(sketch, "E804", {"start": v(42.14, 41.86) * mm, "end": v(42.01, 42.1) * mm});
            skLineSegment(sketch, "E805", {"start": v(42.01, 42.1) * mm, "end": v(41.94, 42.38) * mm});
            skLineSegment(sketch, "E806", {"start": v(41.94, 42.38) * mm, "end": v(41.93, 42.66) * mm});
            skLineSegment(sketch, "E807", {"start": v(41.93, 42.66) * mm, "end": v(41.98, 42.87) * mm});
            skLineSegment(sketch, "E808", {"start": v(41.98, 42.87) * mm, "end": v(42.05, 43.08) * mm});
            skLineSegment(sketch, "E809", {"start": v(42.05, 43.08) * mm, "end": v(42.15, 43.27) * mm});
            skLineSegment(sketch, "E810", {"start": v(42.15, 43.27) * mm, "end": v(42.27, 43.45) * mm});
            skLineSegment(sketch, "E811", {"start": v(42.27, 43.45) * mm, "end": v(42.32, 43.65) * mm});
            skLineSegment(sketch, "E812", {"start": v(42.32, 43.65) * mm, "end": v(42.22, 43.85) * mm});
            skLineSegment(sketch, "E813", {"start": v(42.22, 43.85) * mm, "end": v(42.02, 44.05) * mm});
            skLineSegment(sketch, "E814", {"start": v(42.02, 44.05) * mm, "end": v(41.8, 44.25) * mm});
            skLineSegment(sketch, "E815", {"start": v(41.8, 44.25) * mm, "end": v(41.6, 44.34) * mm});
            skLineSegment(sketch, "E816", {"start": v(41.6, 44.34) * mm, "end": v(41.4, 44.28) * mm});
            skLineSegment(sketch, "E817", {"start": v(41.4, 44.28) * mm, "end": v(41.22, 44.15) * mm});
            skLineSegment(sketch, "E818", {"start": v(41.22, 44.15) * mm, "end": v(41.04, 44.04) * mm});
            skLineSegment(sketch, "E819", {"start": v(41.04, 44.04) * mm, "end": v(40.84, 43.96) * mm});
            skLineSegment(sketch, "E820", {"start": v(40.84, 43.96) * mm, "end": v(40.62, 43.9) * mm});
            skLineSegment(sketch, "E821", {"start": v(40.62, 43.9) * mm, "end": v(40.34, 43.9) * mm});
            skLineSegment(sketch, "E822", {"start": v(40.34, 43.9) * mm, "end": v(40.07, 43.96) * mm});
            skLineSegment(sketch, "E823", {"start": v(40.07, 43.96) * mm, "end": v(39.82, 44.07) * mm});
            skLineSegment(sketch, "E824", {"start": v(39.82, 44.07) * mm, "end": v(39.59, 44.24) * mm});
            skLineSegment(sketch, "E825", {"start": v(39.59, 44.24) * mm, "end": v(39.4, 44.45) * mm});
            skLineSegment(sketch, "E826", {"start": v(39.4, 44.45) * mm, "end": v(39.25, 44.69) * mm});
            skLineSegment(sketch, "E827", {"start": v(39.25, 44.69) * mm, "end": v(39.17, 44.95) * mm});
            skLineSegment(sketch, "E828", {"start": v(39.17, 44.95) * mm, "end": v(39.14, 45.23) * mm});
            skLineSegment(sketch, "E829", {"start": v(39.14, 45.23) * mm, "end": v(39.18, 45.45) * mm});
            skLineSegment(sketch, "E830", {"start": v(39.18, 45.45) * mm, "end": v(39.24, 45.66) * mm});
            skLineSegment(sketch, "E831", {"start": v(39.24, 45.66) * mm, "end": v(39.32, 45.85) * mm});
            skLineSegment(sketch, "E832", {"start": v(39.32, 45.85) * mm, "end": v(39.43, 46.04) * mm});
            skLineSegment(sketch, "E833", {"start": v(39.43, 46.04) * mm, "end": v(39.47, 46.25) * mm});
            skLineSegment(sketch, "E834", {"start": v(39.47, 46.25) * mm, "end": v(39.35, 46.44) * mm});
            skLineSegment(sketch, "E835", {"start": v(39.35, 46.44) * mm, "end": v(39.14, 46.63) * mm});
            skLineSegment(sketch, "E836", {"start": v(39.14, 46.63) * mm, "end": v(38.92, 46.81) * mm});
            skLineSegment(sketch, "E837", {"start": v(38.92, 46.81) * mm, "end": v(38.7, 46.89) * mm});
            skLineSegment(sketch, "E838", {"start": v(38.7, 46.89) * mm, "end": v(38.5, 46.81) * mm});
            skLineSegment(sketch, "E839", {"start": v(38.5, 46.81) * mm, "end": v(38.34, 46.68) * mm});
            skLineSegment(sketch, "E840", {"start": v(38.34, 46.68) * mm, "end": v(38.16, 46.56) * mm});
            skLineSegment(sketch, "E841", {"start": v(38.16, 46.56) * mm, "end": v(37.97, 46.46) * mm});
            skLineSegment(sketch, "E842", {"start": v(37.97, 46.46) * mm, "end": v(37.76, 46.39) * mm});
            skLineSegment(sketch, "E843", {"start": v(37.76, 46.39) * mm, "end": v(37.48, 46.37) * mm});
            skLineSegment(sketch, "E844", {"start": v(37.48, 46.37) * mm, "end": v(37.2, 46.4) * mm});
            skLineSegment(sketch, "E845", {"start": v(37.2, 46.4) * mm, "end": v(36.94, 46.5) * mm});
            skLineSegment(sketch, "E846", {"start": v(36.94, 46.5) * mm, "end": v(36.7, 46.66) * mm});
            skLineSegment(sketch, "E847", {"start": v(36.7, 46.66) * mm, "end": v(36.5, 46.86) * mm});
            skLineSegment(sketch, "E848", {"start": v(36.5, 46.86) * mm, "end": v(36.34, 47.09) * mm});
            skLineSegment(sketch, "E849", {"start": v(36.34, 47.09) * mm, "end": v(36.24, 47.34) * mm});
            skLineSegment(sketch, "E850", {"start": v(36.24, 47.34) * mm, "end": v(36.19, 47.62) * mm});
            skLineSegment(sketch, "E851", {"start": v(36.19, 47.62) * mm, "end": v(36.21, 47.84) * mm});
            skLineSegment(sketch, "E852", {"start": v(36.21, 47.84) * mm, "end": v(36.26, 48.05) * mm});
            skLineSegment(sketch, "E853", {"start": v(36.26, 48.05) * mm, "end": v(36.33, 48.26) * mm});
            skLineSegment(sketch, "E854", {"start": v(36.33, 48.26) * mm, "end": v(36.43, 48.45) * mm});
            skLineSegment(sketch, "E855", {"start": v(36.43, 48.45) * mm, "end": v(36.45, 48.66) * mm});
            skLineSegment(sketch, "E856", {"start": v(36.45, 48.66) * mm, "end": v(36.33, 48.85) * mm});
            skLineSegment(sketch, "E857", {"start": v(36.33, 48.85) * mm, "end": v(36.1, 49.02) * mm});
            skLineSegment(sketch, "E858", {"start": v(36.1, 49.02) * mm, "end": v(35.87, 49.19) * mm});
            skLineSegment(sketch, "E859", {"start": v(35.87, 49.19) * mm, "end": v(35.65, 49.25) * mm});
            skLineSegment(sketch, "E860", {"start": v(35.65, 49.25) * mm, "end": v(35.46, 49.16) * mm});
            skLineSegment(sketch, "E861", {"start": v(35.46, 49.16) * mm, "end": v(35.3, 49.01) * mm});
            skLineSegment(sketch, "E862", {"start": v(35.3, 49.01) * mm, "end": v(35.13, 48.88) * mm});
            skLineSegment(sketch, "E863", {"start": v(35.13, 48.88) * mm, "end": v(34.94, 48.78) * mm});
            skLineSegment(sketch, "E864", {"start": v(34.94, 48.78) * mm, "end": v(34.74, 48.69) * mm});
            skLineSegment(sketch, "E865", {"start": v(34.74, 48.69) * mm, "end": v(34.46, 48.65) * mm});
            skLineSegment(sketch, "E866", {"start": v(34.46, 48.65) * mm, "end": v(34.18, 48.67) * mm});
            skLineSegment(sketch, "E867", {"start": v(34.18, 48.67) * mm, "end": v(33.92, 48.76) * mm});
            skLineSegment(sketch, "E868", {"start": v(33.92, 48.76) * mm, "end": v(33.67, 48.9) * mm});
            skLineSegment(sketch, "E869", {"start": v(33.67, 48.9) * mm, "end": v(33.45, 49.08) * mm});
            skLineSegment(sketch, "E870", {"start": v(33.45, 49.08) * mm, "end": v(33.28, 49.3) * mm});
            skLineSegment(sketch, "E871", {"start": v(33.28, 49.3) * mm, "end": v(33.16, 49.55) * mm});
            skLineSegment(sketch, "E872", {"start": v(33.16, 49.55) * mm, "end": v(33.1, 49.82) * mm});
            skLineSegment(sketch, "E873", {"start": v(33.1, 49.82) * mm, "end": v(33.1, 50.04) * mm});
            skLineSegment(sketch, "E874", {"start": v(33.1, 50.04) * mm, "end": v(33.14, 50.26) * mm});
            skLineSegment(sketch, "E875", {"start": v(33.14, 50.26) * mm, "end": v(33.2, 50.46) * mm});
            skLineSegment(sketch, "E876", {"start": v(33.2, 50.46) * mm, "end": v(33.28, 50.66) * mm});
            skLineSegment(sketch, "E877", {"start": v(33.28, 50.66) * mm, "end": v(33.3, 50.87) * mm});
            skLineSegment(sketch, "E878", {"start": v(33.3, 50.87) * mm, "end": v(33.16, 51.05) * mm});
            skLineSegment(sketch, "E879", {"start": v(33.16, 51.05) * mm, "end": v(32.92, 51.2) * mm});
            skLineSegment(sketch, "E880", {"start": v(32.92, 51.2) * mm, "end": v(32.68, 51.36) * mm});
            skLineSegment(sketch, "E881", {"start": v(32.68, 51.36) * mm, "end": v(32.46, 51.41) * mm});
            skLineSegment(sketch, "E882", {"start": v(32.46, 51.41) * mm, "end": v(32.27, 51.31) * mm});
            skLineSegment(sketch, "E883", {"start": v(32.27, 51.31) * mm, "end": v(32.12, 51.15) * mm});
            skLineSegment(sketch, "E884", {"start": v(32.12, 51.15) * mm, "end": v(31.96, 51.01) * mm});
            skLineSegment(sketch, "E885", {"start": v(31.96, 51.01) * mm, "end": v(31.78, 50.9) * mm});
            skLineSegment(sketch, "E886", {"start": v(31.78, 50.9) * mm, "end": v(31.58, 50.8) * mm});
            skLineSegment(sketch, "E887", {"start": v(31.58, 50.8) * mm, "end": v(31.3, 50.74) * mm});
            skLineSegment(sketch, "E888", {"start": v(31.3, 50.74) * mm, "end": v(31.03, 50.74) * mm});
            skLineSegment(sketch, "E889", {"start": v(31.03, 50.74) * mm, "end": v(30.76, 50.81) * mm});
            skLineSegment(sketch, "E890", {"start": v(30.76, 50.81) * mm, "end": v(30.5, 50.93) * mm});
            skLineSegment(sketch, "E891", {"start": v(30.5, 50.93) * mm, "end": v(30.27, 51.1) * mm});
            skLineSegment(sketch, "E892", {"start": v(30.27, 51.1) * mm, "end": v(30.09, 51.3) * mm});
            skLineSegment(sketch, "E893", {"start": v(30.09, 51.3) * mm, "end": v(29.95, 51.55) * mm});
            skLineSegment(sketch, "E894", {"start": v(29.95, 51.55) * mm, "end": v(29.87, 51.82) * mm});
            skLineSegment(sketch, "E895", {"start": v(29.87, 51.82) * mm, "end": v(29.86, 52.04) * mm});
            skLineSegment(sketch, "E896", {"start": v(29.86, 52.04) * mm, "end": v(29.88, 52.26) * mm});
            skLineSegment(sketch, "E897", {"start": v(29.88, 52.26) * mm, "end": v(29.93, 52.47) * mm});
            skLineSegment(sketch, "E898", {"start": v(29.93, 52.47) * mm, "end": v(30, 52.67) * mm});
            skLineSegment(sketch, "E899", {"start": v(30, 52.67) * mm, "end": v(30, 52.88) * mm});
            skLineSegment(sketch, "E900", {"start": v(30, 52.88) * mm, "end": v(29.85, 53.05) * mm});
            skLineSegment(sketch, "E901", {"start": v(29.85, 53.05) * mm, "end": v(29.6, 53.2) * mm});
            skLineSegment(sketch, "E902", {"start": v(29.6, 53.2) * mm, "end": v(29.35, 53.33) * mm});
            skLineSegment(sketch, "E903", {"start": v(29.35, 53.33) * mm, "end": v(29.13, 53.37) * mm});
            skLineSegment(sketch, "E904", {"start": v(29.13, 53.37) * mm, "end": v(28.95, 53.25) * mm});
            skLineSegment(sketch, "E905", {"start": v(28.95, 53.25) * mm, "end": v(28.81, 53.09) * mm});
            skLineSegment(sketch, "E906", {"start": v(28.81, 53.09) * mm, "end": v(28.66, 52.94) * mm});
            skLineSegment(sketch, "E907", {"start": v(28.66, 52.94) * mm, "end": v(28.48, 52.8) * mm});
            skLineSegment(sketch, "E908", {"start": v(28.48, 52.8) * mm, "end": v(28.3, 52.7) * mm});
            skLineSegment(sketch, "E909", {"start": v(28.3, 52.7) * mm, "end": v(28.02, 52.62) * mm});
            skLineSegment(sketch, "E910", {"start": v(28.02, 52.62) * mm, "end": v(27.75, 52.61) * mm});
            skLineSegment(sketch, "E911", {"start": v(27.75, 52.61) * mm, "end": v(27.47, 52.66) * mm});
            skLineSegment(sketch, "E912", {"start": v(27.47, 52.66) * mm, "end": v(27.2, 52.76) * mm});
            skLineSegment(sketch, "E913", {"start": v(27.2, 52.76) * mm, "end": v(26.97, 52.92) * mm});
            skLineSegment(sketch, "E914", {"start": v(26.97, 52.92) * mm, "end": v(26.77, 53.11) * mm});
            skLineSegment(sketch, "E915", {"start": v(26.77, 53.11) * mm, "end": v(26.62, 53.35) * mm});
            skLineSegment(sketch, "E916", {"start": v(26.62, 53.35) * mm, "end": v(26.52, 53.6) * mm});
            skLineSegment(sketch, "E917", {"start": v(26.52, 53.6) * mm, "end": v(26.5, 53.83) * mm});
            skLineSegment(sketch, "E918", {"start": v(26.5, 53.83) * mm, "end": v(26.5, 54.05) * mm});
            skLineSegment(sketch, "E919", {"start": v(26.5, 54.05) * mm, "end": v(26.54, 54.26) * mm});
            skLineSegment(sketch, "E920", {"start": v(26.54, 54.26) * mm, "end": v(26.6, 54.47) * mm});
            skLineSegment(sketch, "E921", {"start": v(26.6, 54.47) * mm, "end": v(26.58, 54.68) * mm});
            skLineSegment(sketch, "E922", {"start": v(26.58, 54.68) * mm, "end": v(26.43, 54.84) * mm});
            skLineSegment(sketch, "E923", {"start": v(26.43, 54.84) * mm, "end": v(26.17, 54.96) * mm});
            skLineSegment(sketch, "E924", {"start": v(26.17, 54.96) * mm, "end": v(25.9, 55.09) * mm});
            skLineSegment(sketch, "E925", {"start": v(25.9, 55.09) * mm, "end": v(25.68, 55.1) * mm});
            skLineSegment(sketch, "E926", {"start": v(25.68, 55.1) * mm, "end": v(25.51, 54.98) * mm});
            skLineSegment(sketch, "E927", {"start": v(25.51, 54.98) * mm, "end": v(25.39, 54.8) * mm});
            skLineSegment(sketch, "E928", {"start": v(25.39, 54.8) * mm, "end": v(25.24, 54.65) * mm});
            skLineSegment(sketch, "E929", {"start": v(25.24, 54.65) * mm, "end": v(25.08, 54.5) * mm});
            skLineSegment(sketch, "E930", {"start": v(25.08, 54.5) * mm, "end": v(24.9, 54.38) * mm});
            skLineSegment(sketch, "E931", {"start": v(24.9, 54.38) * mm, "end": v(24.63, 54.3) * mm});
            skLineSegment(sketch, "E932", {"start": v(24.63, 54.3) * mm, "end": v(24.35, 54.26) * mm});
            skLineSegment(sketch, "E933", {"start": v(24.35, 54.26) * mm, "end": v(24.07, 54.3) * mm});
            skLineSegment(sketch, "E934", {"start": v(24.07, 54.3) * mm, "end": v(23.8, 54.38) * mm});
            skLineSegment(sketch, "E935", {"start": v(23.8, 54.38) * mm, "end": v(23.56, 54.52) * mm});
            skLineSegment(sketch, "E936", {"start": v(23.56, 54.52) * mm, "end": v(23.35, 54.7) * mm});
            skLineSegment(sketch, "E937", {"start": v(23.35, 54.7) * mm, "end": v(23.18, 54.93) * mm});
            skLineSegment(sketch, "E938", {"start": v(23.18, 54.93) * mm, "end": v(23.07, 55.18) * mm});
            skLineSegment(sketch, "E939", {"start": v(23.07, 55.18) * mm, "end": v(23.03, 55.4) * mm});
            skLineSegment(sketch, "E940", {"start": v(23.03, 55.4) * mm, "end": v(23.03, 55.62) * mm});
            skLineSegment(sketch, "E941", {"start": v(23.03, 55.62) * mm, "end": v(23.05, 55.83) * mm});
            skLineSegment(sketch, "E942", {"start": v(23.05, 55.83) * mm, "end": v(23.09, 56.04) * mm});
            skLineSegment(sketch, "E943", {"start": v(23.09, 56.04) * mm, "end": v(23.06, 56.25) * mm});
            skLineSegment(sketch, "E944", {"start": v(23.06, 56.25) * mm, "end": v(22.9, 56.4) * mm});
            skLineSegment(sketch, "E945", {"start": v(22.9, 56.4) * mm, "end": v(22.63, 56.51) * mm});
            skLineSegment(sketch, "E946", {"start": v(22.63, 56.51) * mm, "end": v(22.36, 56.62) * mm});
            skLineSegment(sketch, "E947", {"start": v(22.36, 56.62) * mm, "end": v(22.14, 56.62) * mm});
            skLineSegment(sketch, "E948", {"start": v(22.14, 56.62) * mm, "end": v(21.97, 56.5) * mm});
            skLineSegment(sketch, "E949", {"start": v(21.97, 56.5) * mm, "end": v(21.86, 56.3) * mm});
            skLineSegment(sketch, "E950", {"start": v(21.86, 56.3) * mm, "end": v(21.72, 56.14) * mm});
            skLineSegment(sketch, "E951", {"start": v(21.72, 56.14) * mm, "end": v(21.57, 55.99) * mm});
            skLineSegment(sketch, "E952", {"start": v(21.57, 55.99) * mm, "end": v(21.4, 55.85) * mm});
            skLineSegment(sketch, "E953", {"start": v(21.4, 55.85) * mm, "end": v(21.14, 55.75) * mm});
            skLineSegment(sketch, "E954", {"start": v(21.14, 55.75) * mm, "end": v(20.86, 55.7) * mm});
            skLineSegment(sketch, "E955", {"start": v(20.86, 55.7) * mm, "end": v(20.58, 55.71) * mm});
            skLineSegment(sketch, "E956", {"start": v(20.58, 55.71) * mm, "end": v(20.3, 55.78) * mm});
            skLineSegment(sketch, "E957", {"start": v(20.3, 55.78) * mm, "end": v(20.05, 55.9) * mm});
            skLineSegment(sketch, "E958", {"start": v(20.05, 55.9) * mm, "end": v(19.83, 56.07) * mm});
            skLineSegment(sketch, "E959", {"start": v(19.83, 56.07) * mm, "end": v(19.65, 56.29) * mm});
            skLineSegment(sketch, "E960", {"start": v(19.65, 56.29) * mm, "end": v(19.52, 56.53) * mm});
            skLineSegment(sketch, "E961", {"start": v(19.52, 56.53) * mm, "end": v(19.47, 56.75) * mm});
            skLineSegment(sketch, "E962", {"start": v(19.47, 56.75) * mm, "end": v(19.45, 56.97) * mm});
            skLineSegment(sketch, "E963", {"start": v(19.45, 56.97) * mm, "end": v(19.46, 57.18) * mm});
            skLineSegment(sketch, "E964", {"start": v(19.46, 57.18) * mm, "end": v(19.49, 57.4) * mm});
            skLineSegment(sketch, "E965", {"start": v(19.49, 57.4) * mm, "end": v(19.45, 57.6) * mm});
            skLineSegment(sketch, "E966", {"start": v(19.45, 57.6) * mm, "end": v(19.27, 57.74) * mm});
            skLineSegment(sketch, "E967", {"start": v(19.27, 57.74) * mm, "end": v(19, 57.83) * mm});
            skLineSegment(sketch, "E968", {"start": v(19, 57.83) * mm, "end": v(18.73, 57.92) * mm});
            skLineSegment(sketch, "E969", {"start": v(18.73, 57.92) * mm, "end": v(18.5, 57.91) * mm});
            skLineSegment(sketch, "E970", {"start": v(18.5, 57.91) * mm, "end": v(18.34, 57.77) * mm});
            skLineSegment(sketch, "E971", {"start": v(18.34, 57.77) * mm, "end": v(18.24, 57.58) * mm});
            skLineSegment(sketch, "E972", {"start": v(18.24, 57.58) * mm, "end": v(18.12, 57.4) * mm});
            skLineSegment(sketch, "E973", {"start": v(18.12, 57.4) * mm, "end": v(17.97, 57.24) * mm});
            skLineSegment(sketch, "E974", {"start": v(17.97, 57.24) * mm, "end": v(17.8, 57.1) * mm});
            skLineSegment(sketch, "E975", {"start": v(17.8, 57.1) * mm, "end": v(17.56, 56.97) * mm});
            skLineSegment(sketch, "E976", {"start": v(17.56, 56.97) * mm, "end": v(17.29, 56.91) * mm});
            skLineSegment(sketch, "E977", {"start": v(17.29, 56.91) * mm, "end": v(17, 56.9) * mm});
            skLineSegment(sketch, "E978", {"start": v(17, 56.9) * mm, "end": v(16.73, 56.96) * mm});
            skLineSegment(sketch, "E979", {"start": v(16.73, 56.96) * mm, "end": v(16.47, 57.06) * mm});
            skLineSegment(sketch, "E980", {"start": v(16.47, 57.06) * mm, "end": v(16.23, 57.22) * mm});
            skLineSegment(sketch, "E981", {"start": v(16.23, 57.22) * mm, "end": v(16.04, 57.42) * mm});
            skLineSegment(sketch, "E982", {"start": v(16.04, 57.42) * mm, "end": v(15.9, 57.66) * mm});
            skLineSegment(sketch, "E983", {"start": v(15.9, 57.66) * mm, "end": v(15.83, 57.87) * mm});
            skLineSegment(sketch, "E984", {"start": v(15.83, 57.87) * mm, "end": v(15.8, 58.09) * mm});
            skLineSegment(sketch, "E985", {"start": v(15.8, 58.09) * mm, "end": v(15.8, 58.3) * mm});
            skLineSegment(sketch, "E986", {"start": v(15.8, 58.3) * mm, "end": v(15.8, 58.52) * mm});
            skLineSegment(sketch, "E987", {"start": v(15.8, 58.52) * mm, "end": v(15.75, 58.72) * mm});
            skLineSegment(sketch, "E988", {"start": v(15.75, 58.72) * mm, "end": v(15.57, 58.85) * mm});
            skLineSegment(sketch, "E989", {"start": v(15.57, 58.85) * mm, "end": v(15.3, 58.92) * mm});
            skLineSegment(sketch, "E990", {"start": v(15.3, 58.92) * mm, "end": v(15.01, 59) * mm});
            skLineSegment(sketch, "E991", {"start": v(15.01, 59) * mm, "end": v(14.79, 58.97) * mm});
            skLineSegment(sketch, "E992", {"start": v(14.79, 58.97) * mm, "end": v(14.64, 58.82) * mm});
            skLineSegment(sketch, "E993", {"start": v(14.64, 58.82) * mm, "end": v(14.55, 58.62) * mm});
            skLineSegment(sketch, "E994", {"start": v(14.55, 58.62) * mm, "end": v(14.44, 58.44) * mm});
            skLineSegment(sketch, "E995", {"start": v(14.44, 58.44) * mm, "end": v(14.3, 58.27) * mm});
            skLineSegment(sketch, "E996", {"start": v(14.3, 58.27) * mm, "end": v(14.15, 58.11) * mm});
            skLineSegment(sketch, "E997", {"start": v(14.15, 58.11) * mm, "end": v(13.9, 57.97) * mm});
            skLineSegment(sketch, "E998", {"start": v(13.9, 57.97) * mm, "end": v(13.64, 57.9) * mm});
            skLineSegment(sketch, "E999", {"start": v(13.64, 57.9) * mm, "end": v(13.36, 57.87) * mm});
            skLineSegment(sketch, "E1000", {"start": v(13.36, 57.87) * mm, "end": v(13.08, 57.9) * mm});
            skLineSegment(sketch, "E1001", {"start": v(13.08, 57.9) * mm, "end": v(12.81, 58) * mm});
            skLineSegment(sketch, "E1002", {"start": v(12.81, 58) * mm, "end": v(12.57, 58.13) * mm});
            skLineSegment(sketch, "E1003", {"start": v(12.57, 58.13) * mm, "end": v(12.36, 58.32) * mm});
            skLineSegment(sketch, "E1004", {"start": v(12.36, 58.32) * mm, "end": v(12.2, 58.55) * mm});
            skLineSegment(sketch, "E1005", {"start": v(12.2, 58.55) * mm, "end": v(12.13, 58.76) * mm});
            skLineSegment(sketch, "E1006", {"start": v(12.13, 58.76) * mm, "end": v(12.08, 58.97) * mm});
            skLineSegment(sketch, "E1007", {"start": v(12.08, 58.97) * mm, "end": v(12.06, 59.19) * mm});
            skLineSegment(sketch, "E1008", {"start": v(12.06, 59.19) * mm, "end": v(12.06, 59.4) * mm});
            skLineSegment(sketch, "E1009", {"start": v(12.06, 59.4) * mm, "end": v(12, 59.6) * mm});
            skLineSegment(sketch, "E1010", {"start": v(12, 59.6) * mm, "end": v(11.8, 59.72) * mm});
            skLineSegment(sketch, "E1011", {"start": v(11.8, 59.72) * mm, "end": v(11.52, 59.77) * mm});
            skLineSegment(sketch, "E1012", {"start": v(11.52, 59.77) * mm, "end": v(11.24, 59.83) * mm});
            skLineSegment(sketch, "E1013", {"start": v(11.24, 59.83) * mm, "end": v(11.02, 59.8) * mm});
            skLineSegment(sketch, "E1014", {"start": v(11.02, 59.8) * mm, "end": v(10.88, 59.63) * mm});
            skLineSegment(sketch, "E1015", {"start": v(10.88, 59.63) * mm, "end": v(10.8, 59.43) * mm});
            skLineSegment(sketch, "E1016", {"start": v(10.8, 59.43) * mm, "end": v(10.7, 59.24) * mm});
            skLineSegment(sketch, "E1017", {"start": v(10.7, 59.24) * mm, "end": v(10.58, 59.06) * mm});
            skLineSegment(sketch, "E1018", {"start": v(10.58, 59.06) * mm, "end": v(10.44, 58.9) * mm});
            skLineSegment(sketch, "E1019", {"start": v(10.44, 58.9) * mm, "end": v(10.2, 58.74) * mm});
            skLineSegment(sketch, "E1020", {"start": v(10.2, 58.74) * mm, "end": v(9.94, 58.64) * mm});
            skLineSegment(sketch, "E1021", {"start": v(9.94, 58.64) * mm, "end": v(9.66, 58.6) * mm});
            skLineSegment(sketch, "E1022", {"start": v(9.66, 58.6) * mm, "end": v(9.38, 58.62) * mm});
            skLineSegment(sketch, "E1023", {"start": v(9.38, 58.62) * mm, "end": v(9.1, 58.69) * mm});
            skLineSegment(sketch, "E1024", {"start": v(9.1, 58.69) * mm, "end": v(8.86, 58.81) * mm});
            skLineSegment(sketch, "E1025", {"start": v(8.86, 58.81) * mm, "end": v(8.64, 58.99) * mm});
            skLineSegment(sketch, "E1026", {"start": v(8.64, 58.99) * mm, "end": v(8.47, 59.2) * mm});
            skLineSegment(sketch, "E1027", {"start": v(8.47, 59.2) * mm, "end": v(8.38, 59.41) * mm});
            skLineSegment(sketch, "E1028", {"start": v(8.38, 59.41) * mm, "end": v(8.32, 59.62) * mm});
            skLineSegment(sketch, "E1029", {"start": v(8.32, 59.62) * mm, "end": v(8.28, 59.83) * mm});
            skLineSegment(sketch, "E1030", {"start": v(8.28, 59.83) * mm, "end": v(8.27, 60.05) * mm});
            skLineSegment(sketch, "E1031", {"start": v(8.27, 60.05) * mm, "end": v(8.2, 60.24) * mm});
            skLineSegment(sketch, "E1032", {"start": v(8.2, 60.24) * mm, "end": v(8, 60.35) * mm});
            skLineSegment(sketch, "E1033", {"start": v(8, 60.35) * mm, "end": v(7.7, 60.38) * mm});
            skLineSegment(sketch, "E1034", {"start": v(7.7, 60.38) * mm, "end": v(7.42, 60.42) * mm});
            skLineSegment(sketch, "E1035", {"start": v(7.42, 60.42) * mm, "end": v(7.2, 60.37) * mm});
            skLineSegment(sketch, "E1036", {"start": v(7.2, 60.37) * mm, "end": v(7.08, 60.2) * mm});
            skLineSegment(sketch, "E1037", {"start": v(7.08, 60.2) * mm, "end": v(7.01, 60) * mm});
            skLineSegment(sketch, "E1038", {"start": v(7.01, 60) * mm, "end": v(6.93, 59.8) * mm});
            skLineSegment(sketch, "E1039", {"start": v(6.93, 59.8) * mm, "end": v(6.81, 59.61) * mm});
            skLineSegment(sketch, "E1040", {"start": v(6.81, 59.61) * mm, "end": v(6.68, 59.44) * mm});
            skLineSegment(sketch, "E1041", {"start": v(6.68, 59.44) * mm, "end": v(6.46, 59.27) * mm});
            skLineSegment(sketch, "E1042", {"start": v(6.46, 59.27) * mm, "end": v(6.2, 59.15) * mm});
            skLineSegment(sketch, "E1043", {"start": v(6.2, 59.15) * mm, "end": v(5.93, 59.1) * mm});
            skLineSegment(sketch, "E1044", {"start": v(5.93, 59.1) * mm, "end": v(5.64, 59.1) * mm});
            skLineSegment(sketch, "E1045", {"start": v(5.64, 59.1) * mm, "end": v(5.37, 59.15) * mm});
            skLineSegment(sketch, "E1046", {"start": v(5.37, 59.15) * mm, "end": v(5.1, 59.26) * mm});
            skLineSegment(sketch, "E1047", {"start": v(5.1, 59.26) * mm, "end": v(4.88, 59.42) * mm});
            skLineSegment(sketch, "E1048", {"start": v(4.88, 59.42) * mm, "end": v(4.7, 59.62) * mm});
            skLineSegment(sketch, "E1049", {"start": v(4.7, 59.62) * mm, "end": v(4.6, 59.82) * mm});
            skLineSegment(sketch, "E1050", {"start": v(4.6, 59.82) * mm, "end": v(4.52, 60.03) * mm});
            skLineSegment(sketch, "E1051", {"start": v(4.52, 60.03) * mm, "end": v(4.47, 60.24) * mm});
            skLineSegment(sketch, "E1052", {"start": v(4.47, 60.24) * mm, "end": v(4.45, 60.45) * mm});
            skLineSegment(sketch, "E1053", {"start": v(4.45, 60.45) * mm, "end": v(4.35, 60.64) * mm});
            skLineSegment(sketch, "E1054", {"start": v(4.35, 60.64) * mm, "end": v(4.15, 60.73) * mm});
            skLineSegment(sketch, "E1055", {"start": v(4.15, 60.73) * mm, "end": v(3.86, 60.75) * mm});
            skLineSegment(sketch, "E1056", {"start": v(3.86, 60.75) * mm, "end": v(3.58, 60.77) * mm});
            skLineSegment(sketch, "E1057", {"start": v(3.58, 60.77) * mm, "end": v(3.36, 60.7) * mm});
            skLineSegment(sketch, "E1058", {"start": v(3.36, 60.7) * mm, "end": v(3.24, 60.53) * mm});
            skLineSegment(sketch, "E1059", {"start": v(3.24, 60.53) * mm, "end": v(3.2, 60.32) * mm});
            skLineSegment(sketch, "E1060", {"start": v(3.2, 60.32) * mm, "end": v(3.12, 60.12) * mm});
            skLineSegment(sketch, "E1061", {"start": v(3.12, 60.12) * mm, "end": v(3.02, 59.92) * mm});
            skLineSegment(sketch, "E1062", {"start": v(3.02, 59.92) * mm, "end": v(2.9, 59.74) * mm});
            skLineSegment(sketch, "E1063", {"start": v(2.9, 59.74) * mm, "end": v(2.68, 59.56) * mm});
            skLineSegment(sketch, "E1064", {"start": v(2.68, 59.56) * mm, "end": v(2.44, 59.43) * mm});
            skLineSegment(sketch, "E1065", {"start": v(2.44, 59.43) * mm, "end": v(2.17, 59.35) * mm});
            skLineSegment(sketch, "E1066", {"start": v(2.17, 59.35) * mm, "end": v(1.88, 59.33) * mm});
            skLineSegment(sketch, "E1067", {"start": v(1.88, 59.33) * mm, "end": v(1.6, 59.37) * mm});
            skLineSegment(sketch, "E1068", {"start": v(1.6, 59.37) * mm, "end": v(1.34, 59.46) * mm});
            skLineSegment(sketch, "E1069", {"start": v(1.34, 59.46) * mm, "end": v(1.1, 59.6) * mm});
            skLineSegment(sketch, "E1070", {"start": v(1.1, 59.6) * mm, "end": v(0.9, 59.8) * mm});
            skLineSegment(sketch, "E1071", {"start": v(0.9, 59.8) * mm, "end": v(0.79, 60) * mm});
            skLineSegment(sketch, "E1072", {"start": v(0.79, 60) * mm, "end": v(0.7, 60.2) * mm});
            skLineSegment(sketch, "E1073", {"start": v(0.7, 60.2) * mm, "end": v(0.64, 60.4) * mm});
            skLineSegment(sketch, "E1074", {"start": v(0.64, 60.4) * mm, "end": v(0.6, 60.6) * mm});
            skLineSegment(sketch, "E1075", {"start": v(0.6, 60.6) * mm, "end": v(0.5, 60.8) * mm});
            skLineSegment(sketch, "E1076", {"start": v(0.5, 60.8) * mm, "end": v(0.29, 60.87) * mm});
            skLineSegment(sketch, "E1077", {"start": v(0.29, 60.87) * mm, "end": v(0, 60.87) * mm});
            skLineSegment(sketch, "E1078", {"start": v(0, 60.87) * mm, "end": v(-0.29, 60.87) * mm});
            skLineSegment(sketch, "E1079", {"start": v(-0.29, 60.87) * mm, "end": v(-0.5, 60.8) * mm});
            skLineSegment(sketch, "E1080", {"start": v(-0.5, 60.8) * mm, "end": v(-0.6, 60.6) * mm});
            skLineSegment(sketch, "E1081", {"start": v(-0.6, 60.6) * mm, "end": v(-0.64, 60.4) * mm});
            skLineSegment(sketch, "E1082", {"start": v(-0.64, 60.4) * mm, "end": v(-0.7, 60.2) * mm});
            skLineSegment(sketch, "E1083", {"start": v(-0.7, 60.2) * mm, "end": v(-0.79, 60) * mm});
            skLineSegment(sketch, "E1084", {"start": v(-0.79, 60) * mm, "end": v(-0.9, 59.8) * mm});
            skLineSegment(sketch, "E1085", {"start": v(-0.9, 59.8) * mm, "end": v(-1.1, 59.6) * mm});
            skLineSegment(sketch, "E1086", {"start": v(-1.1, 59.6) * mm, "end": v(-1.34, 59.46) * mm});
            skLineSegment(sketch, "E1087", {"start": v(-1.34, 59.46) * mm, "end": v(-1.6, 59.37) * mm});
            skLineSegment(sketch, "E1088", {"start": v(-1.6, 59.37) * mm, "end": v(-1.88, 59.33) * mm});
            skLineSegment(sketch, "E1089", {"start": v(-1.88, 59.33) * mm, "end": v(-2.17, 59.35) * mm});
            skLineSegment(sketch, "E1090", {"start": v(-2.17, 59.35) * mm, "end": v(-2.44, 59.43) * mm});
            skLineSegment(sketch, "E1091", {"start": v(-2.44, 59.43) * mm, "end": v(-2.68, 59.56) * mm});
            skLineSegment(sketch, "E1092", {"start": v(-2.68, 59.56) * mm, "end": v(-2.9, 59.74) * mm});
            skLineSegment(sketch, "E1093", {"start": v(-2.9, 59.74) * mm, "end": v(-3.02, 59.92) * mm});
            skLineSegment(sketch, "E1094", {"start": v(-3.02, 59.92) * mm, "end": v(-3.12, 60.12) * mm});
            skLineSegment(sketch, "E1095", {"start": v(-3.12, 60.12) * mm, "end": v(-3.2, 60.32) * mm});
            skLineSegment(sketch, "E1096", {"start": v(-3.2, 60.32) * mm, "end": v(-3.24, 60.53) * mm});
            skLineSegment(sketch, "E1097", {"start": v(-3.24, 60.53) * mm, "end": v(-3.36, 60.7) * mm});
            skLineSegment(sketch, "E1098", {"start": v(-3.36, 60.7) * mm, "end": v(-3.58, 60.77) * mm});
            skLineSegment(sketch, "E1099", {"start": v(-3.58, 60.77) * mm, "end": v(-3.86, 60.75) * mm});
            skLineSegment(sketch, "E1100", {"start": v(-3.86, 60.75) * mm, "end": v(-4.15, 60.73) * mm});
            skLineSegment(sketch, "E1101", {"start": v(-4.15, 60.73) * mm, "end": v(-4.35, 60.64) * mm});
            skLineSegment(sketch, "E1102", {"start": v(-4.35, 60.64) * mm, "end": v(-4.45, 60.45) * mm});
            skLineSegment(sketch, "E1103", {"start": v(-4.45, 60.45) * mm, "end": v(-4.47, 60.24) * mm});
            skLineSegment(sketch, "E1104", {"start": v(-4.47, 60.24) * mm, "end": v(-4.52, 60.03) * mm});
            skLineSegment(sketch, "E1105", {"start": v(-4.52, 60.03) * mm, "end": v(-4.6, 59.82) * mm});
            skLineSegment(sketch, "E1106", {"start": v(-4.6, 59.82) * mm, "end": v(-4.7, 59.62) * mm});
            skLineSegment(sketch, "E1107", {"start": v(-4.7, 59.62) * mm, "end": v(-4.88, 59.42) * mm});
            skLineSegment(sketch, "E1108", {"start": v(-4.88, 59.42) * mm, "end": v(-5.1, 59.26) * mm});
            skLineSegment(sketch, "E1109", {"start": v(-5.1, 59.26) * mm, "end": v(-5.37, 59.15) * mm});
            skLineSegment(sketch, "E1110", {"start": v(-5.37, 59.15) * mm, "end": v(-5.64, 59.1) * mm});
            skLineSegment(sketch, "E1111", {"start": v(-5.64, 59.1) * mm, "end": v(-5.93, 59.1) * mm});
            skLineSegment(sketch, "E1112", {"start": v(-5.93, 59.1) * mm, "end": v(-6.2, 59.15) * mm});
            skLineSegment(sketch, "E1113", {"start": v(-6.2, 59.15) * mm, "end": v(-6.46, 59.27) * mm});
            skLineSegment(sketch, "E1114", {"start": v(-6.46, 59.27) * mm, "end": v(-6.68, 59.44) * mm});
            skLineSegment(sketch, "E1115", {"start": v(-6.68, 59.44) * mm, "end": v(-6.81, 59.61) * mm});
            skLineSegment(sketch, "E1116", {"start": v(-6.81, 59.61) * mm, "end": v(-6.92, 59.8) * mm});
            skLineSegment(sketch, "E1117", {"start": v(-6.92, 59.8) * mm, "end": v(-7.01, 60) * mm});
            skLineSegment(sketch, "E1118", {"start": v(-7.01, 60) * mm, "end": v(-7.08, 60.2) * mm});
            skLineSegment(sketch, "E1119", {"start": v(-7.08, 60.2) * mm, "end": v(-7.2, 60.37) * mm});
            skLineSegment(sketch, "E1120", {"start": v(-7.2, 60.37) * mm, "end": v(-7.42, 60.42) * mm});
            skLineSegment(sketch, "E1121", {"start": v(-7.42, 60.42) * mm, "end": v(-7.7, 60.38) * mm});
            skLineSegment(sketch, "E1122", {"start": v(-7.7, 60.38) * mm, "end": v(-8, 60.35) * mm});
            skLineSegment(sketch, "E1123", {"start": v(-8, 60.35) * mm, "end": v(-8.2, 60.24) * mm});
            skLineSegment(sketch, "E1124", {"start": v(-8.2, 60.24) * mm, "end": v(-8.27, 60.05) * mm});
            skLineSegment(sketch, "E1125", {"start": v(-8.27, 60.05) * mm, "end": v(-8.28, 59.83) * mm});
            skLineSegment(sketch, "E1126", {"start": v(-8.28, 59.83) * mm, "end": v(-8.32, 59.62) * mm});
            skLineSegment(sketch, "E1127", {"start": v(-8.32, 59.62) * mm, "end": v(-8.38, 59.41) * mm});
            skLineSegment(sketch, "E1128", {"start": v(-8.38, 59.41) * mm, "end": v(-8.47, 59.2) * mm});
            skLineSegment(sketch, "E1129", {"start": v(-8.47, 59.2) * mm, "end": v(-8.64, 58.99) * mm});
            skLineSegment(sketch, "E1130", {"start": v(-8.64, 58.99) * mm, "end": v(-8.86, 58.81) * mm});
            skLineSegment(sketch, "E1131", {"start": v(-8.86, 58.81) * mm, "end": v(-9.1, 58.69) * mm});
            skLineSegment(sketch, "E1132", {"start": v(-9.1, 58.69) * mm, "end": v(-9.38, 58.62) * mm});
            skLineSegment(sketch, "E1133", {"start": v(-9.38, 58.62) * mm, "end": v(-9.66, 58.6) * mm});
            skLineSegment(sketch, "E1134", {"start": v(-9.66, 58.6) * mm, "end": v(-9.94, 58.64) * mm});
            skLineSegment(sketch, "E1135", {"start": v(-9.94, 58.64) * mm, "end": v(-10.2, 58.74) * mm});
            skLineSegment(sketch, "E1136", {"start": v(-10.2, 58.74) * mm, "end": v(-10.44, 58.9) * mm});
            skLineSegment(sketch, "E1137", {"start": v(-10.44, 58.9) * mm, "end": v(-10.58, 59.06) * mm});
            skLineSegment(sketch, "E1138", {"start": v(-10.58, 59.06) * mm, "end": v(-10.7, 59.24) * mm});
            skLineSegment(sketch, "E1139", {"start": v(-10.7, 59.24) * mm, "end": v(-10.8, 59.43) * mm});
            skLineSegment(sketch, "E1140", {"start": v(-10.8, 59.43) * mm, "end": v(-10.88, 59.63) * mm});
            skLineSegment(sketch, "E1141", {"start": v(-10.88, 59.63) * mm, "end": v(-11.02, 59.8) * mm});
            skLineSegment(sketch, "E1142", {"start": v(-11.02, 59.8) * mm, "end": v(-11.24, 59.83) * mm});
            skLineSegment(sketch, "E1143", {"start": v(-11.24, 59.83) * mm, "end": v(-11.52, 59.77) * mm});
            skLineSegment(sketch, "E1144", {"start": v(-11.52, 59.77) * mm, "end": v(-11.8, 59.72) * mm});
            skLineSegment(sketch, "E1145", {"start": v(-11.8, 59.72) * mm, "end": v(-12, 59.6) * mm});
            skLineSegment(sketch, "E1146", {"start": v(-12, 59.6) * mm, "end": v(-12.06, 59.4) * mm});
            skLineSegment(sketch, "E1147", {"start": v(-12.06, 59.4) * mm, "end": v(-12.06, 59.19) * mm});
            skLineSegment(sketch, "E1148", {"start": v(-12.06, 59.19) * mm, "end": v(-12.08, 58.97) * mm});
            skLineSegment(sketch, "E1149", {"start": v(-12.08, 58.97) * mm, "end": v(-12.13, 58.76) * mm});
            skLineSegment(sketch, "E1150", {"start": v(-12.13, 58.76) * mm, "end": v(-12.2, 58.55) * mm});
            skLineSegment(sketch, "E1151", {"start": v(-12.2, 58.55) * mm, "end": v(-12.36, 58.32) * mm});
            skLineSegment(sketch, "E1152", {"start": v(-12.36, 58.32) * mm, "end": v(-12.57, 58.13) * mm});
            skLineSegment(sketch, "E1153", {"start": v(-12.57, 58.13) * mm, "end": v(-12.81, 58) * mm});
            skLineSegment(sketch, "E1154", {"start": v(-12.81, 58) * mm, "end": v(-13.08, 57.9) * mm});
            skLineSegment(sketch, "E1155", {"start": v(-13.08, 57.9) * mm, "end": v(-13.36, 57.87) * mm});
            skLineSegment(sketch, "E1156", {"start": v(-13.36, 57.87) * mm, "end": v(-13.64, 57.9) * mm});
            skLineSegment(sketch, "E1157", {"start": v(-13.64, 57.9) * mm, "end": v(-13.9, 57.97) * mm});
            skLineSegment(sketch, "E1158", {"start": v(-13.9, 57.97) * mm, "end": v(-14.15, 58.11) * mm});
            skLineSegment(sketch, "E1159", {"start": v(-14.15, 58.11) * mm, "end": v(-14.3, 58.27) * mm});
            skLineSegment(sketch, "E1160", {"start": v(-14.3, 58.27) * mm, "end": v(-14.44, 58.44) * mm});
            skLineSegment(sketch, "E1161", {"start": v(-14.44, 58.44) * mm, "end": v(-14.55, 58.62) * mm});
            skLineSegment(sketch, "E1162", {"start": v(-14.55, 58.62) * mm, "end": v(-14.64, 58.82) * mm});
            skLineSegment(sketch, "E1163", {"start": v(-14.64, 58.82) * mm, "end": v(-14.79, 58.97) * mm});
            skLineSegment(sketch, "E1164", {"start": v(-14.79, 58.97) * mm, "end": v(-15.01, 59) * mm});
            skLineSegment(sketch, "E1165", {"start": v(-15.01, 59) * mm, "end": v(-15.3, 58.92) * mm});
            skLineSegment(sketch, "E1166", {"start": v(-15.3, 58.92) * mm, "end": v(-15.57, 58.85) * mm});
            skLineSegment(sketch, "E1167", {"start": v(-15.57, 58.85) * mm, "end": v(-15.75, 58.72) * mm});
            skLineSegment(sketch, "E1168", {"start": v(-15.75, 58.72) * mm, "end": v(-15.8, 58.52) * mm});
            skLineSegment(sketch, "E1169", {"start": v(-15.8, 58.52) * mm, "end": v(-15.8, 58.3) * mm});
            skLineSegment(sketch, "E1170", {"start": v(-15.8, 58.3) * mm, "end": v(-15.8, 58.09) * mm});
            skLineSegment(sketch, "E1171", {"start": v(-15.8, 58.09) * mm, "end": v(-15.83, 57.87) * mm});
            skLineSegment(sketch, "E1172", {"start": v(-15.83, 57.87) * mm, "end": v(-15.9, 57.66) * mm});
            skLineSegment(sketch, "E1173", {"start": v(-15.9, 57.66) * mm, "end": v(-16.04, 57.42) * mm});
            skLineSegment(sketch, "E1174", {"start": v(-16.04, 57.42) * mm, "end": v(-16.23, 57.22) * mm});
            skLineSegment(sketch, "E1175", {"start": v(-16.23, 57.22) * mm, "end": v(-16.47, 57.06) * mm});
            skLineSegment(sketch, "E1176", {"start": v(-16.47, 57.06) * mm, "end": v(-16.73, 56.96) * mm});
            skLineSegment(sketch, "E1177", {"start": v(-16.73, 56.96) * mm, "end": v(-17, 56.9) * mm});
            skLineSegment(sketch, "E1178", {"start": v(-17, 56.9) * mm, "end": v(-17.29, 56.91) * mm});
            skLineSegment(sketch, "E1179", {"start": v(-17.29, 56.91) * mm, "end": v(-17.56, 56.97) * mm});
            skLineSegment(sketch, "E1180", {"start": v(-17.56, 56.97) * mm, "end": v(-17.8, 57.1) * mm});
            skLineSegment(sketch, "E1181", {"start": v(-17.8, 57.1) * mm, "end": v(-17.97, 57.24) * mm});
            skLineSegment(sketch, "E1182", {"start": v(-17.97, 57.24) * mm, "end": v(-18.12, 57.4) * mm});
            skLineSegment(sketch, "E1183", {"start": v(-18.12, 57.4) * mm, "end": v(-18.24, 57.58) * mm});
            skLineSegment(sketch, "E1184", {"start": v(-18.24, 57.58) * mm, "end": v(-18.34, 57.77) * mm});
            skLineSegment(sketch, "E1185", {"start": v(-18.34, 57.77) * mm, "end": v(-18.5, 57.91) * mm});
            skLineSegment(sketch, "E1186", {"start": v(-18.5, 57.91) * mm, "end": v(-18.73, 57.92) * mm});
            skLineSegment(sketch, "E1187", {"start": v(-18.73, 57.92) * mm, "end": v(-19, 57.83) * mm});
            skLineSegment(sketch, "E1188", {"start": v(-19, 57.83) * mm, "end": v(-19.27, 57.74) * mm});
            skLineSegment(sketch, "E1189", {"start": v(-19.27, 57.74) * mm, "end": v(-19.45, 57.6) * mm});
            skLineSegment(sketch, "E1190", {"start": v(-19.45, 57.6) * mm, "end": v(-19.49, 57.4) * mm});
            skLineSegment(sketch, "E1191", {"start": v(-19.49, 57.4) * mm, "end": v(-19.46, 57.18) * mm});
            skLineSegment(sketch, "E1192", {"start": v(-19.46, 57.18) * mm, "end": v(-19.45, 56.97) * mm});
            skLineSegment(sketch, "E1193", {"start": v(-19.45, 56.97) * mm, "end": v(-19.47, 56.75) * mm});
            skLineSegment(sketch, "E1194", {"start": v(-19.47, 56.75) * mm, "end": v(-19.52, 56.53) * mm});
            skLineSegment(sketch, "E1195", {"start": v(-19.52, 56.53) * mm, "end": v(-19.65, 56.29) * mm});
            skLineSegment(sketch, "E1196", {"start": v(-19.65, 56.29) * mm, "end": v(-19.83, 56.07) * mm});
            skLineSegment(sketch, "E1197", {"start": v(-19.83, 56.07) * mm, "end": v(-20.05, 55.9) * mm});
            skLineSegment(sketch, "E1198", {"start": v(-20.05, 55.9) * mm, "end": v(-20.3, 55.78) * mm});
            skLineSegment(sketch, "E1199", {"start": v(-20.3, 55.78) * mm, "end": v(-20.58, 55.71) * mm});
            skLineSegment(sketch, "E1200", {"start": v(-20.58, 55.71) * mm, "end": v(-20.86, 55.7) * mm});
            skLineSegment(sketch, "E1201", {"start": v(-20.86, 55.7) * mm, "end": v(-21.14, 55.75) * mm});
            skLineSegment(sketch, "E1202", {"start": v(-21.14, 55.75) * mm, "end": v(-21.4, 55.85) * mm});
            skLineSegment(sketch, "E1203", {"start": v(-21.4, 55.85) * mm, "end": v(-21.57, 55.99) * mm});
            skLineSegment(sketch, "E1204", {"start": v(-21.57, 55.99) * mm, "end": v(-21.72, 56.14) * mm});
            skLineSegment(sketch, "E1205", {"start": v(-21.72, 56.14) * mm, "end": v(-21.86, 56.3) * mm});
            skLineSegment(sketch, "E1206", {"start": v(-21.86, 56.3) * mm, "end": v(-21.97, 56.5) * mm});
            skLineSegment(sketch, "E1207", {"start": v(-21.97, 56.5) * mm, "end": v(-22.14, 56.62) * mm});
            skLineSegment(sketch, "E1208", {"start": v(-22.14, 56.62) * mm, "end": v(-22.36, 56.62) * mm});
            skLineSegment(sketch, "E1209", {"start": v(-22.36, 56.62) * mm, "end": v(-22.63, 56.51) * mm});
            skLineSegment(sketch, "E1210", {"start": v(-22.63, 56.51) * mm, "end": v(-22.9, 56.4) * mm});
            skLineSegment(sketch, "E1211", {"start": v(-22.9, 56.4) * mm, "end": v(-23.06, 56.25) * mm});
            skLineSegment(sketch, "E1212", {"start": v(-23.06, 56.25) * mm, "end": v(-23.09, 56.04) * mm});
            skLineSegment(sketch, "E1213", {"start": v(-23.09, 56.04) * mm, "end": v(-23.05, 55.83) * mm});
            skLineSegment(sketch, "E1214", {"start": v(-23.05, 55.83) * mm, "end": v(-23.03, 55.62) * mm});
            skLineSegment(sketch, "E1215", {"start": v(-23.03, 55.62) * mm, "end": v(-23.03, 55.4) * mm});
            skLineSegment(sketch, "E1216", {"start": v(-23.03, 55.4) * mm, "end": v(-23.07, 55.18) * mm});
            skLineSegment(sketch, "E1217", {"start": v(-23.07, 55.18) * mm, "end": v(-23.18, 54.93) * mm});
            skLineSegment(sketch, "E1218", {"start": v(-23.18, 54.93) * mm, "end": v(-23.35, 54.7) * mm});
            skLineSegment(sketch, "E1219", {"start": v(-23.35, 54.7) * mm, "end": v(-23.56, 54.52) * mm});
            skLineSegment(sketch, "E1220", {"start": v(-23.56, 54.52) * mm, "end": v(-23.8, 54.38) * mm});
            skLineSegment(sketch, "E1221", {"start": v(-23.8, 54.38) * mm, "end": v(-24.07, 54.3) * mm});
            skLineSegment(sketch, "E1222", {"start": v(-24.07, 54.3) * mm, "end": v(-24.35, 54.26) * mm});
            skLineSegment(sketch, "E1223", {"start": v(-24.35, 54.26) * mm, "end": v(-24.63, 54.3) * mm});
            skLineSegment(sketch, "E1224", {"start": v(-24.63, 54.3) * mm, "end": v(-24.9, 54.38) * mm});
            skLineSegment(sketch, "E1225", {"start": v(-24.9, 54.38) * mm, "end": v(-25.08, 54.5) * mm});
            skLineSegment(sketch, "E1226", {"start": v(-25.08, 54.5) * mm, "end": v(-25.24, 54.65) * mm});
            skLineSegment(sketch, "E1227", {"start": v(-25.24, 54.65) * mm, "end": v(-25.39, 54.8) * mm});
            skLineSegment(sketch, "E1228", {"start": v(-25.39, 54.8) * mm, "end": v(-25.51, 54.98) * mm});
            skLineSegment(sketch, "E1229", {"start": v(-25.51, 54.98) * mm, "end": v(-25.68, 55.1) * mm});
            skLineSegment(sketch, "E1230", {"start": v(-25.68, 55.1) * mm, "end": v(-25.9, 55.09) * mm});
            skLineSegment(sketch, "E1231", {"start": v(-25.9, 55.09) * mm, "end": v(-26.17, 54.96) * mm});
            skLineSegment(sketch, "E1232", {"start": v(-26.17, 54.96) * mm, "end": v(-26.43, 54.84) * mm});
            skLineSegment(sketch, "E1233", {"start": v(-26.43, 54.84) * mm, "end": v(-26.58, 54.68) * mm});
            skLineSegment(sketch, "E1234", {"start": v(-26.58, 54.68) * mm, "end": v(-26.6, 54.47) * mm});
            skLineSegment(sketch, "E1235", {"start": v(-26.6, 54.47) * mm, "end": v(-26.54, 54.26) * mm});
            skLineSegment(sketch, "E1236", {"start": v(-26.54, 54.26) * mm, "end": v(-26.5, 54.05) * mm});
            skLineSegment(sketch, "E1237", {"start": v(-26.5, 54.05) * mm, "end": v(-26.5, 53.83) * mm});
            skLineSegment(sketch, "E1238", {"start": v(-26.5, 53.83) * mm, "end": v(-26.52, 53.6) * mm});
            skLineSegment(sketch, "E1239", {"start": v(-26.52, 53.6) * mm, "end": v(-26.62, 53.35) * mm});
            skLineSegment(sketch, "E1240", {"start": v(-26.62, 53.35) * mm, "end": v(-26.77, 53.11) * mm});
            skLineSegment(sketch, "E1241", {"start": v(-26.77, 53.11) * mm, "end": v(-26.97, 52.92) * mm});
            skLineSegment(sketch, "E1242", {"start": v(-26.97, 52.92) * mm, "end": v(-27.2, 52.76) * mm});
            skLineSegment(sketch, "E1243", {"start": v(-27.2, 52.76) * mm, "end": v(-27.47, 52.66) * mm});
            skLineSegment(sketch, "E1244", {"start": v(-27.47, 52.66) * mm, "end": v(-27.75, 52.61) * mm});
            skLineSegment(sketch, "E1245", {"start": v(-27.75, 52.61) * mm, "end": v(-28.02, 52.62) * mm});
            skLineSegment(sketch, "E1246", {"start": v(-28.02, 52.62) * mm, "end": v(-28.3, 52.7) * mm});
            skLineSegment(sketch, "E1247", {"start": v(-28.3, 52.7) * mm, "end": v(-28.48, 52.8) * mm});
            skLineSegment(sketch, "E1248", {"start": v(-28.48, 52.8) * mm, "end": v(-28.66, 52.94) * mm});
            skLineSegment(sketch, "E1249", {"start": v(-28.66, 52.94) * mm, "end": v(-28.81, 53.09) * mm});
            skLineSegment(sketch, "E1250", {"start": v(-28.81, 53.09) * mm, "end": v(-28.95, 53.25) * mm});
            skLineSegment(sketch, "E1251", {"start": v(-28.95, 53.25) * mm, "end": v(-29.13, 53.37) * mm});
            skLineSegment(sketch, "E1252", {"start": v(-29.13, 53.37) * mm, "end": v(-29.35, 53.33) * mm});
            skLineSegment(sketch, "E1253", {"start": v(-29.35, 53.33) * mm, "end": v(-29.6, 53.2) * mm});
            skLineSegment(sketch, "E1254", {"start": v(-29.6, 53.2) * mm, "end": v(-29.85, 53.05) * mm});
            skLineSegment(sketch, "E1255", {"start": v(-29.85, 53.05) * mm, "end": v(-30, 52.88) * mm});
            skLineSegment(sketch, "E1256", {"start": v(-30, 52.88) * mm, "end": v(-30, 52.67) * mm});
            skLineSegment(sketch, "E1257", {"start": v(-30, 52.67) * mm, "end": v(-29.93, 52.47) * mm});
            skLineSegment(sketch, "E1258", {"start": v(-29.93, 52.47) * mm, "end": v(-29.88, 52.26) * mm});
            skLineSegment(sketch, "E1259", {"start": v(-29.88, 52.26) * mm, "end": v(-29.86, 52.04) * mm});
            skLineSegment(sketch, "E1260", {"start": v(-29.86, 52.04) * mm, "end": v(-29.87, 51.82) * mm});
            skLineSegment(sketch, "E1261", {"start": v(-29.87, 51.82) * mm, "end": v(-29.95, 51.55) * mm});
            skLineSegment(sketch, "E1262", {"start": v(-29.95, 51.55) * mm, "end": v(-30.09, 51.3) * mm});
            skLineSegment(sketch, "E1263", {"start": v(-30.09, 51.3) * mm, "end": v(-30.27, 51.1) * mm});
            skLineSegment(sketch, "E1264", {"start": v(-30.27, 51.1) * mm, "end": v(-30.5, 50.93) * mm});
            skLineSegment(sketch, "E1265", {"start": v(-30.5, 50.93) * mm, "end": v(-30.76, 50.81) * mm});
            skLineSegment(sketch, "E1266", {"start": v(-30.76, 50.81) * mm, "end": v(-31.03, 50.74) * mm});
            skLineSegment(sketch, "E1267", {"start": v(-31.03, 50.74) * mm, "end": v(-31.3, 50.74) * mm});
            skLineSegment(sketch, "E1268", {"start": v(-31.3, 50.74) * mm, "end": v(-31.58, 50.8) * mm});
            skLineSegment(sketch, "E1269", {"start": v(-31.58, 50.8) * mm, "end": v(-31.78, 50.9) * mm});
            skLineSegment(sketch, "E1270", {"start": v(-31.78, 50.9) * mm, "end": v(-31.96, 51.01) * mm});
            skLineSegment(sketch, "E1271", {"start": v(-31.96, 51.01) * mm, "end": v(-32.12, 51.15) * mm});
            skLineSegment(sketch, "E1272", {"start": v(-32.12, 51.15) * mm, "end": v(-32.27, 51.31) * mm});
            skLineSegment(sketch, "E1273", {"start": v(-32.27, 51.31) * mm, "end": v(-32.45, 51.41) * mm});
            skLineSegment(sketch, "E1274", {"start": v(-32.45, 51.41) * mm, "end": v(-32.68, 51.36) * mm});
            skLineSegment(sketch, "E1275", {"start": v(-32.68, 51.36) * mm, "end": v(-32.92, 51.2) * mm});
            skLineSegment(sketch, "E1276", {"start": v(-32.92, 51.2) * mm, "end": v(-33.16, 51.05) * mm});
            skLineSegment(sketch, "E1277", {"start": v(-33.16, 51.05) * mm, "end": v(-33.3, 50.87) * mm});
            skLineSegment(sketch, "E1278", {"start": v(-33.3, 50.87) * mm, "end": v(-33.28, 50.66) * mm});
            skLineSegment(sketch, "E1279", {"start": v(-33.28, 50.66) * mm, "end": v(-33.2, 50.46) * mm});
            skLineSegment(sketch, "E1280", {"start": v(-33.2, 50.46) * mm, "end": v(-33.14, 50.26) * mm});
            skLineSegment(sketch, "E1281", {"start": v(-33.14, 50.26) * mm, "end": v(-33.1, 50.04) * mm});
            skLineSegment(sketch, "E1282", {"start": v(-33.1, 50.04) * mm, "end": v(-33.1, 49.82) * mm});
            skLineSegment(sketch, "E1283", {"start": v(-33.1, 49.82) * mm, "end": v(-33.16, 49.55) * mm});
            skLineSegment(sketch, "E1284", {"start": v(-33.16, 49.55) * mm, "end": v(-33.28, 49.3) * mm});
            skLineSegment(sketch, "E1285", {"start": v(-33.28, 49.3) * mm, "end": v(-33.45, 49.08) * mm});
            skLineSegment(sketch, "E1286", {"start": v(-33.45, 49.08) * mm, "end": v(-33.67, 48.9) * mm});
            skLineSegment(sketch, "E1287", {"start": v(-33.67, 48.9) * mm, "end": v(-33.92, 48.76) * mm});
            skLineSegment(sketch, "E1288", {"start": v(-33.92, 48.76) * mm, "end": v(-34.18, 48.67) * mm});
            skLineSegment(sketch, "E1289", {"start": v(-34.18, 48.67) * mm, "end": v(-34.46, 48.65) * mm});
            skLineSegment(sketch, "E1290", {"start": v(-34.46, 48.65) * mm, "end": v(-34.74, 48.69) * mm});
            skLineSegment(sketch, "E1291", {"start": v(-34.74, 48.69) * mm, "end": v(-34.94, 48.78) * mm});
            skLineSegment(sketch, "E1292", {"start": v(-34.94, 48.78) * mm, "end": v(-35.13, 48.88) * mm});
            skLineSegment(sketch, "E1293", {"start": v(-35.13, 48.88) * mm, "end": v(-35.3, 49.01) * mm});
            skLineSegment(sketch, "E1294", {"start": v(-35.3, 49.01) * mm, "end": v(-35.46, 49.16) * mm});
            skLineSegment(sketch, "E1295", {"start": v(-35.46, 49.16) * mm, "end": v(-35.65, 49.25) * mm});
            skLineSegment(sketch, "E1296", {"start": v(-35.65, 49.25) * mm, "end": v(-35.87, 49.19) * mm});
            skLineSegment(sketch, "E1297", {"start": v(-35.87, 49.19) * mm, "end": v(-36.1, 49.02) * mm});
            skLineSegment(sketch, "E1298", {"start": v(-36.1, 49.02) * mm, "end": v(-36.33, 48.85) * mm});
            skLineSegment(sketch, "E1299", {"start": v(-36.33, 48.85) * mm, "end": v(-36.45, 48.66) * mm});
            skLineSegment(sketch, "E1300", {"start": v(-36.45, 48.66) * mm, "end": v(-36.43, 48.45) * mm});
            skLineSegment(sketch, "E1301", {"start": v(-36.43, 48.45) * mm, "end": v(-36.33, 48.26) * mm});
            skLineSegment(sketch, "E1302", {"start": v(-36.33, 48.26) * mm, "end": v(-36.26, 48.05) * mm});
            skLineSegment(sketch, "E1303", {"start": v(-36.26, 48.05) * mm, "end": v(-36.21, 47.84) * mm});
            skLineSegment(sketch, "E1304", {"start": v(-36.21, 47.84) * mm, "end": v(-36.19, 47.62) * mm});
            skLineSegment(sketch, "E1305", {"start": v(-36.19, 47.62) * mm, "end": v(-36.24, 47.34) * mm});
            skLineSegment(sketch, "E1306", {"start": v(-36.24, 47.34) * mm, "end": v(-36.34, 47.09) * mm});
            skLineSegment(sketch, "E1307", {"start": v(-36.34, 47.09) * mm, "end": v(-36.5, 46.86) * mm});
            skLineSegment(sketch, "E1308", {"start": v(-36.5, 46.86) * mm, "end": v(-36.7, 46.66) * mm});
            skLineSegment(sketch, "E1309", {"start": v(-36.7, 46.66) * mm, "end": v(-36.94, 46.5) * mm});
            skLineSegment(sketch, "E1310", {"start": v(-36.94, 46.5) * mm, "end": v(-37.2, 46.4) * mm});
            skLineSegment(sketch, "E1311", {"start": v(-37.2, 46.4) * mm, "end": v(-37.48, 46.37) * mm});
            skLineSegment(sketch, "E1312", {"start": v(-37.48, 46.37) * mm, "end": v(-37.76, 46.39) * mm});
            skLineSegment(sketch, "E1313", {"start": v(-37.76, 46.39) * mm, "end": v(-37.97, 46.46) * mm});
            skLineSegment(sketch, "E1314", {"start": v(-37.97, 46.46) * mm, "end": v(-38.16, 46.56) * mm});
            skLineSegment(sketch, "E1315", {"start": v(-38.16, 46.56) * mm, "end": v(-38.34, 46.68) * mm});
            skLineSegment(sketch, "E1316", {"start": v(-38.34, 46.68) * mm, "end": v(-38.5, 46.81) * mm});
            skLineSegment(sketch, "E1317", {"start": v(-38.5, 46.81) * mm, "end": v(-38.7, 46.89) * mm});
            skLineSegment(sketch, "E1318", {"start": v(-38.7, 46.89) * mm, "end": v(-38.92, 46.81) * mm});
            skLineSegment(sketch, "E1319", {"start": v(-38.92, 46.81) * mm, "end": v(-39.14, 46.63) * mm});
            skLineSegment(sketch, "E1320", {"start": v(-39.14, 46.63) * mm, "end": v(-39.35, 46.44) * mm});
            skLineSegment(sketch, "E1321", {"start": v(-39.35, 46.44) * mm, "end": v(-39.47, 46.25) * mm});
            skLineSegment(sketch, "E1322", {"start": v(-39.47, 46.25) * mm, "end": v(-39.43, 46.04) * mm});
            skLineSegment(sketch, "E1323", {"start": v(-39.43, 46.04) * mm, "end": v(-39.32, 45.85) * mm});
            skLineSegment(sketch, "E1324", {"start": v(-39.32, 45.85) * mm, "end": v(-39.24, 45.66) * mm});
            skLineSegment(sketch, "E1325", {"start": v(-39.24, 45.66) * mm, "end": v(-39.18, 45.45) * mm});
            skLineSegment(sketch, "E1326", {"start": v(-39.18, 45.45) * mm, "end": v(-39.14, 45.23) * mm});
            skLineSegment(sketch, "E1327", {"start": v(-39.14, 45.23) * mm, "end": v(-39.17, 44.95) * mm});
            skLineSegment(sketch, "E1328", {"start": v(-39.17, 44.95) * mm, "end": v(-39.25, 44.69) * mm});
            skLineSegment(sketch, "E1329", {"start": v(-39.25, 44.69) * mm, "end": v(-39.4, 44.45) * mm});
            skLineSegment(sketch, "E1330", {"start": v(-39.4, 44.45) * mm, "end": v(-39.59, 44.24) * mm});
            skLineSegment(sketch, "E1331", {"start": v(-39.59, 44.24) * mm, "end": v(-39.82, 44.07) * mm});
            skLineSegment(sketch, "E1332", {"start": v(-39.82, 44.07) * mm, "end": v(-40.07, 43.96) * mm});
            skLineSegment(sketch, "E1333", {"start": v(-40.07, 43.96) * mm, "end": v(-40.34, 43.9) * mm});
            skLineSegment(sketch, "E1334", {"start": v(-40.34, 43.9) * mm, "end": v(-40.62, 43.9) * mm});
            skLineSegment(sketch, "E1335", {"start": v(-40.62, 43.9) * mm, "end": v(-40.84, 43.96) * mm});
            skLineSegment(sketch, "E1336", {"start": v(-40.84, 43.96) * mm, "end": v(-41.04, 44.04) * mm});
            skLineSegment(sketch, "E1337", {"start": v(-41.04, 44.04) * mm, "end": v(-41.22, 44.15) * mm});
            skLineSegment(sketch, "E1338", {"start": v(-41.22, 44.15) * mm, "end": v(-41.4, 44.28) * mm});
            skLineSegment(sketch, "E1339", {"start": v(-41.4, 44.28) * mm, "end": v(-41.6, 44.34) * mm});
            skLineSegment(sketch, "E1340", {"start": v(-41.6, 44.34) * mm, "end": v(-41.8, 44.25) * mm});
            skLineSegment(sketch, "E1341", {"start": v(-41.8, 44.25) * mm, "end": v(-42.02, 44.05) * mm});
            skLineSegment(sketch, "E1342", {"start": v(-42.02, 44.05) * mm, "end": v(-42.22, 43.85) * mm});
            skLineSegment(sketch, "E1343", {"start": v(-42.22, 43.85) * mm, "end": v(-42.32, 43.65) * mm});
            skLineSegment(sketch, "E1344", {"start": v(-42.32, 43.65) * mm, "end": v(-42.27, 43.45) * mm});
            skLineSegment(sketch, "E1345", {"start": v(-42.27, 43.45) * mm, "end": v(-42.15, 43.27) * mm});
            skLineSegment(sketch, "E1346", {"start": v(-42.15, 43.27) * mm, "end": v(-42.05, 43.08) * mm});
            skLineSegment(sketch, "E1347", {"start": v(-42.05, 43.08) * mm, "end": v(-41.98, 42.87) * mm});
            skLineSegment(sketch, "E1348", {"start": v(-41.98, 42.87) * mm, "end": v(-41.93, 42.66) * mm});
            skLineSegment(sketch, "E1349", {"start": v(-41.93, 42.66) * mm, "end": v(-41.94, 42.38) * mm});
            skLineSegment(sketch, "E1350", {"start": v(-41.94, 42.38) * mm, "end": v(-42.01, 42.1) * mm});
            skLineSegment(sketch, "E1351", {"start": v(-42.01, 42.1) * mm, "end": v(-42.14, 41.86) * mm});
            skLineSegment(sketch, "E1352", {"start": v(-42.14, 41.86) * mm, "end": v(-42.32, 41.64) * mm});
            skLineSegment(sketch, "E1353", {"start": v(-42.32, 41.64) * mm, "end": v(-42.53, 41.46) * mm});
            skLineSegment(sketch, "E1354", {"start": v(-42.53, 41.46) * mm, "end": v(-42.78, 41.33) * mm});
            skLineSegment(sketch, "E1355", {"start": v(-42.78, 41.33) * mm, "end": v(-43.05, 41.25) * mm});
            skLineSegment(sketch, "E1356", {"start": v(-43.05, 41.25) * mm, "end": v(-43.33, 41.23) * mm});
            skLineSegment(sketch, "E1357", {"start": v(-43.33, 41.23) * mm, "end": v(-43.54, 41.28) * mm});
            skLineSegment(sketch, "E1358", {"start": v(-43.54, 41.28) * mm, "end": v(-43.75, 41.35) * mm});
            skLineSegment(sketch, "E1359", {"start": v(-43.75, 41.35) * mm, "end": v(-43.94, 41.45) * mm});
            skLineSegment(sketch, "E1360", {"start": v(-43.94, 41.45) * mm, "end": v(-44.12, 41.56) * mm});
            skLineSegment(sketch, "E1361", {"start": v(-44.12, 41.56) * mm, "end": v(-44.33, 41.61) * mm});
            skLineSegment(sketch, "E1362", {"start": v(-44.33, 41.61) * mm, "end": v(-44.53, 41.5) * mm});
            skLineSegment(sketch, "E1363", {"start": v(-44.53, 41.5) * mm, "end": v(-44.73, 41.3) * mm});
            skLineSegment(sketch, "E1364", {"start": v(-44.73, 41.3) * mm, "end": v(-44.92, 41.09) * mm});
            skLineSegment(sketch, "E1365", {"start": v(-44.92, 41.09) * mm, "end": v(-45, 40.88) * mm});
            skLineSegment(sketch, "E1366", {"start": v(-45, 40.88) * mm, "end": v(-44.94, 40.68) * mm});
            skLineSegment(sketch, "E1367", {"start": v(-44.94, 40.68) * mm, "end": v(-44.81, 40.5) * mm});
            skLineSegment(sketch, "E1368", {"start": v(-44.81, 40.5) * mm, "end": v(-44.7, 40.32) * mm});
            skLineSegment(sketch, "E1369", {"start": v(-44.7, 40.32) * mm, "end": v(-44.61, 40.12) * mm});
            skLineSegment(sketch, "E1370", {"start": v(-44.61, 40.12) * mm, "end": v(-44.55, 39.91) * mm});
            skLineSegment(sketch, "E1371", {"start": v(-44.55, 39.91) * mm, "end": v(-44.54, 39.63) * mm});
            skLineSegment(sketch, "E1372", {"start": v(-44.54, 39.63) * mm, "end": v(-44.6, 39.36) * mm});
            skLineSegment(sketch, "E1373", {"start": v(-44.6, 39.36) * mm, "end": v(-44.7, 39.1) * mm});
            skLineSegment(sketch, "E1374", {"start": v(-44.7, 39.1) * mm, "end": v(-44.87, 38.87) * mm});
            skLineSegment(sketch, "E1375", {"start": v(-44.87, 38.87) * mm, "end": v(-45.08, 38.68) * mm});
            skLineSegment(sketch, "E1376", {"start": v(-45.08, 38.68) * mm, "end": v(-45.32, 38.53) * mm});
            skLineSegment(sketch, "E1377", {"start": v(-45.32, 38.53) * mm, "end": v(-45.58, 38.44) * mm});
            skLineSegment(sketch, "E1378", {"start": v(-45.58, 38.44) * mm, "end": v(-45.86, 38.4) * mm});
            skLineSegment(sketch, "E1379", {"start": v(-45.86, 38.4) * mm, "end": v(-46.07, 38.44) * mm});
            skLineSegment(sketch, "E1380", {"start": v(-46.07, 38.44) * mm, "end": v(-46.28, 38.5) * mm});
            skLineSegment(sketch, "E1381", {"start": v(-46.28, 38.5) * mm, "end": v(-46.48, 38.58) * mm});
            skLineSegment(sketch, "E1382", {"start": v(-46.48, 38.58) * mm, "end": v(-46.67, 38.68) * mm});
            skLineSegment(sketch, "E1383", {"start": v(-46.67, 38.68) * mm, "end": v(-46.88, 38.72) * mm});
            skLineSegment(sketch, "E1384", {"start": v(-46.88, 38.72) * mm, "end": v(-47.07, 38.6) * mm});
            skLineSegment(sketch, "E1385", {"start": v(-47.07, 38.6) * mm, "end": v(-47.26, 38.38) * mm});
            skLineSegment(sketch, "E1386", {"start": v(-47.26, 38.38) * mm, "end": v(-47.44, 38.16) * mm});
            skLineSegment(sketch, "E1387", {"start": v(-47.44, 38.16) * mm, "end": v(-47.5, 37.94) * mm});
            skLineSegment(sketch, "E1388", {"start": v(-47.5, 37.94) * mm, "end": v(-47.43, 37.75) * mm});
            skLineSegment(sketch, "E1389", {"start": v(-47.43, 37.75) * mm, "end": v(-47.29, 37.58) * mm});
            skLineSegment(sketch, "E1390", {"start": v(-47.29, 37.58) * mm, "end": v(-47.17, 37.4) * mm});
            skLineSegment(sketch, "E1391", {"start": v(-47.17, 37.4) * mm, "end": v(-47.07, 37.21) * mm});
            skLineSegment(sketch, "E1392", {"start": v(-47.07, 37.21) * mm, "end": v(-47, 37) * mm});
            skLineSegment(sketch, "E1393", {"start": v(-47, 37) * mm, "end": v(-46.97, 36.73) * mm});
            skLineSegment(sketch, "E1394", {"start": v(-46.97, 36.73) * mm, "end": v(-47, 36.45) * mm});
            skLineSegment(sketch, "E1395", {"start": v(-47, 36.45) * mm, "end": v(-47.1, 36.19) * mm});
            skLineSegment(sketch, "E1396", {"start": v(-47.1, 36.19) * mm, "end": v(-47.25, 35.95) * mm});
            skLineSegment(sketch, "E1397", {"start": v(-47.25, 35.95) * mm, "end": v(-47.44, 35.74) * mm});
            skLineSegment(sketch, "E1398", {"start": v(-47.44, 35.74) * mm, "end": v(-47.67, 35.58) * mm});
            skLineSegment(sketch, "E1399", {"start": v(-47.67, 35.58) * mm, "end": v(-47.93, 35.47) * mm});
            skLineSegment(sketch, "E1400", {"start": v(-47.93, 35.47) * mm, "end": v(-48.2, 35.42) * mm});
            skLineSegment(sketch, "E1401", {"start": v(-48.2, 35.42) * mm, "end": v(-48.42, 35.44) * mm});
            skLineSegment(sketch, "E1402", {"start": v(-48.42, 35.44) * mm, "end": v(-48.63, 35.48) * mm});
            skLineSegment(sketch, "E1403", {"start": v(-48.63, 35.48) * mm, "end": v(-48.84, 35.55) * mm});
            skLineSegment(sketch, "E1404", {"start": v(-48.84, 35.55) * mm, "end": v(-49.03, 35.64) * mm});
            skLineSegment(sketch, "E1405", {"start": v(-49.03, 35.64) * mm, "end": v(-49.24, 35.67) * mm});
            skLineSegment(sketch, "E1406", {"start": v(-49.24, 35.67) * mm, "end": v(-49.43, 35.54) * mm});
            skLineSegment(sketch, "E1407", {"start": v(-49.43, 35.54) * mm, "end": v(-49.6, 35.3) * mm});
            skLineSegment(sketch, "E1408", {"start": v(-49.6, 35.3) * mm, "end": v(-49.76, 35.07) * mm});
            skLineSegment(sketch, "E1409", {"start": v(-49.76, 35.07) * mm, "end": v(-49.82, 34.85) * mm});
            skLineSegment(sketch, "E1410", {"start": v(-49.82, 34.85) * mm, "end": v(-49.73, 34.66) * mm});
            skLineSegment(sketch, "E1411", {"start": v(-49.73, 34.66) * mm, "end": v(-49.58, 34.5) * mm});
            skLineSegment(sketch, "E1412", {"start": v(-49.58, 34.5) * mm, "end": v(-49.45, 34.34) * mm});
            skLineSegment(sketch, "E1413", {"start": v(-49.45, 34.34) * mm, "end": v(-49.34, 34.15) * mm});
            skLineSegment(sketch, "E1414", {"start": v(-49.34, 34.15) * mm, "end": v(-49.25, 33.95) * mm});
            skLineSegment(sketch, "E1415", {"start": v(-49.25, 33.95) * mm, "end": v(-49.2, 33.67) * mm});
            skLineSegment(sketch, "E1416", {"start": v(-49.2, 33.67) * mm, "end": v(-49.22, 33.4) * mm});
            skLineSegment(sketch, "E1417", {"start": v(-49.22, 33.4) * mm, "end": v(-49.3, 33.13) * mm});
            skLineSegment(sketch, "E1418", {"start": v(-49.3, 33.13) * mm, "end": v(-49.43, 32.88) * mm});
            skLineSegment(sketch, "E1419", {"start": v(-49.43, 32.88) * mm, "end": v(-49.61, 32.66) * mm});
            skLineSegment(sketch, "E1420", {"start": v(-49.61, 32.66) * mm, "end": v(-49.83, 32.48) * mm});
            skLineSegment(sketch, "E1421", {"start": v(-49.83, 32.48) * mm, "end": v(-50.08, 32.36) * mm});
            skLineSegment(sketch, "E1422", {"start": v(-50.08, 32.36) * mm, "end": v(-50.35, 32.29) * mm});
            skLineSegment(sketch, "E1423", {"start": v(-50.35, 32.29) * mm, "end": v(-50.57, 32.3) * mm});
            skLineSegment(sketch, "E1424", {"start": v(-50.57, 32.3) * mm, "end": v(-50.79, 32.33) * mm});
            skLineSegment(sketch, "E1425", {"start": v(-50.79, 32.33) * mm, "end": v(-51, 32.38) * mm});
            skLineSegment(sketch, "E1426", {"start": v(-51, 32.38) * mm, "end": v(-51.2, 32.46) * mm});
            skLineSegment(sketch, "E1427", {"start": v(-51.2, 32.46) * mm, "end": v(-51.4, 32.47) * mm});
            skLineSegment(sketch, "E1428", {"start": v(-51.4, 32.47) * mm, "end": v(-51.58, 32.33) * mm});
            skLineSegment(sketch, "E1429", {"start": v(-51.58, 32.33) * mm, "end": v(-51.74, 32.09) * mm});
            skLineSegment(sketch, "E1430", {"start": v(-51.74, 32.09) * mm, "end": v(-51.89, 31.84) * mm});
            skLineSegment(sketch, "E1431", {"start": v(-51.89, 31.84) * mm, "end": v(-51.93, 31.62) * mm});
            skLineSegment(sketch, "E1432", {"start": v(-51.93, 31.62) * mm, "end": v(-51.83, 31.44) * mm});
            skLineSegment(sketch, "E1433", {"start": v(-51.83, 31.44) * mm, "end": v(-51.67, 31.3) * mm});
            skLineSegment(sketch, "E1434", {"start": v(-51.67, 31.3) * mm, "end": v(-51.53, 31.13) * mm});
            skLineSegment(sketch, "E1435", {"start": v(-51.53, 31.13) * mm, "end": v(-51.4, 30.95) * mm});
            skLineSegment(sketch, "E1436", {"start": v(-51.4, 30.95) * mm, "end": v(-51.3, 30.76) * mm});
            skLineSegment(sketch, "E1437", {"start": v(-51.3, 30.76) * mm, "end": v(-51.24, 30.48) * mm});
            skLineSegment(sketch, "E1438", {"start": v(-51.24, 30.48) * mm, "end": v(-51.24, 30.2) * mm});
            skLineSegment(sketch, "E1439", {"start": v(-51.24, 30.2) * mm, "end": v(-51.3, 29.93) * mm});
            skLineSegment(sketch, "E1440", {"start": v(-51.3, 29.93) * mm, "end": v(-51.42, 29.68) * mm});
            skLineSegment(sketch, "E1441", {"start": v(-51.42, 29.68) * mm, "end": v(-51.59, 29.45) * mm});
            skLineSegment(sketch, "E1442", {"start": v(-51.59, 29.45) * mm, "end": v(-51.8, 29.26) * mm});
            skLineSegment(sketch, "E1443", {"start": v(-51.8, 29.26) * mm, "end": v(-52.03, 29.11) * mm});
            skLineSegment(sketch, "E1444", {"start": v(-52.03, 29.11) * mm, "end": v(-52.3, 29.03) * mm});
            skLineSegment(sketch, "E1445", {"start": v(-52.3, 29.03) * mm, "end": v(-52.52, 29.02) * mm});
            skLineSegment(sketch, "E1446", {"start": v(-52.52, 29.02) * mm, "end": v(-52.74, 29.04) * mm});
            skLineSegment(sketch, "E1447", {"start": v(-52.74, 29.04) * mm, "end": v(-52.95, 29.08) * mm});
            skLineSegment(sketch, "E1448", {"start": v(-52.95, 29.08) * mm, "end": v(-53.15, 29.15) * mm});
            skLineSegment(sketch, "E1449", {"start": v(-53.15, 29.15) * mm, "end": v(-53.36, 29.14) * mm});
            skLineSegment(sketch, "E1450", {"start": v(-53.36, 29.14) * mm, "end": v(-53.53, 29) * mm});
            skLineSegment(sketch, "E1451", {"start": v(-53.53, 29) * mm, "end": v(-53.67, 28.74) * mm});
            skLineSegment(sketch, "E1452", {"start": v(-53.67, 28.74) * mm, "end": v(-53.8, 28.49) * mm});
            skLineSegment(sketch, "E1453", {"start": v(-53.8, 28.49) * mm, "end": v(-53.83, 28.27) * mm});
            skLineSegment(sketch, "E1454", {"start": v(-53.83, 28.27) * mm, "end": v(-53.72, 28.09) * mm});
            skLineSegment(sketch, "E1455", {"start": v(-53.72, 28.09) * mm, "end": v(-53.55, 27.95) * mm});
            skLineSegment(sketch, "E1456", {"start": v(-53.55, 27.95) * mm, "end": v(-53.4, 27.8) * mm});
            skLineSegment(sketch, "E1457", {"start": v(-53.4, 27.8) * mm, "end": v(-53.26, 27.63) * mm});
            skLineSegment(sketch, "E1458", {"start": v(-53.26, 27.63) * mm, "end": v(-53.15, 27.44) * mm});
            skLineSegment(sketch, "E1459", {"start": v(-53.15, 27.44) * mm, "end": v(-53.07, 27.17) * mm});
            skLineSegment(sketch, "E1460", {"start": v(-53.07, 27.17) * mm, "end": v(-53.06, 26.9) * mm});
            skLineSegment(sketch, "E1461", {"start": v(-53.06, 26.9) * mm, "end": v(-53.1, 26.62) * mm});
            skLineSegment(sketch, "E1462", {"start": v(-53.1, 26.62) * mm, "end": v(-53.2, 26.35) * mm});
            skLineSegment(sketch, "E1463", {"start": v(-53.2, 26.35) * mm, "end": v(-53.35, 26.12) * mm});
            skLineSegment(sketch, "E1464", {"start": v(-53.35, 26.12) * mm, "end": v(-53.54, 25.91) * mm});
            skLineSegment(sketch, "E1465", {"start": v(-53.54, 25.91) * mm, "end": v(-53.77, 25.76) * mm});
            skLineSegment(sketch, "E1466", {"start": v(-53.77, 25.76) * mm, "end": v(-54.03, 25.66) * mm});
            skLineSegment(sketch, "E1467", {"start": v(-54.03, 25.66) * mm, "end": v(-54.25, 25.63) * mm});
            skLineSegment(sketch, "E1468", {"start": v(-54.25, 25.63) * mm, "end": v(-54.47, 25.64) * mm});
            skLineSegment(sketch, "E1469", {"start": v(-54.47, 25.64) * mm, "end": v(-54.69, 25.66) * mm});
            skLineSegment(sketch, "E1470", {"start": v(-54.69, 25.66) * mm, "end": v(-54.9, 25.72) * mm});
            skLineSegment(sketch, "E1471", {"start": v(-54.9, 25.72) * mm, "end": v(-55.1, 25.7) * mm});
            skLineSegment(sketch, "E1472", {"start": v(-55.1, 25.7) * mm, "end": v(-55.26, 25.54) * mm});
            skLineSegment(sketch, "E1473", {"start": v(-55.26, 25.54) * mm, "end": v(-55.38, 25.28) * mm});
            skLineSegment(sketch, "E1474", {"start": v(-55.38, 25.28) * mm, "end": v(-55.5, 25.02) * mm});
            skLineSegment(sketch, "E1475", {"start": v(-55.5, 25.02) * mm, "end": v(-55.52, 24.8) * mm});
            skLineSegment(sketch, "E1476", {"start": v(-55.52, 24.8) * mm, "end": v(-55.4, 24.62) * mm});
            skLineSegment(sketch, "E1477", {"start": v(-55.4, 24.62) * mm, "end": v(-55.22, 24.5) * mm});
            skLineSegment(sketch, "E1478", {"start": v(-55.22, 24.5) * mm, "end": v(-55.05, 24.36) * mm});
            skLineSegment(sketch, "E1479", {"start": v(-55.05, 24.36) * mm, "end": v(-54.91, 24.2) * mm});
            skLineSegment(sketch, "E1480", {"start": v(-54.91, 24.2) * mm, "end": v(-54.78, 24.02) * mm});
            skLineSegment(sketch, "E1481", {"start": v(-54.78, 24.02) * mm, "end": v(-54.69, 23.75) * mm});
            skLineSegment(sketch, "E1482", {"start": v(-54.69, 23.75) * mm, "end": v(-54.66, 23.48) * mm});
            skLineSegment(sketch, "E1483", {"start": v(-54.66, 23.48) * mm, "end": v(-54.68, 23.2) * mm});
            skLineSegment(sketch, "E1484", {"start": v(-54.68, 23.2) * mm, "end": v(-54.76, 22.93) * mm});
            skLineSegment(sketch, "E1485", {"start": v(-54.76, 22.93) * mm, "end": v(-54.9, 22.68) * mm});
            skLineSegment(sketch, "E1486", {"start": v(-54.9, 22.68) * mm, "end": v(-55.08, 22.46) * mm});
            skLineSegment(sketch, "E1487", {"start": v(-55.08, 22.46) * mm, "end": v(-55.3, 22.3) * mm});
            skLineSegment(sketch, "E1488", {"start": v(-55.3, 22.3) * mm, "end": v(-55.55, 22.18) * mm});
            skLineSegment(sketch, "E1489", {"start": v(-55.55, 22.18) * mm, "end": v(-55.77, 22.14) * mm});
            skLineSegment(sketch, "E1490", {"start": v(-55.77, 22.14) * mm, "end": v(-55.99, 22.13) * mm});
            skLineSegment(sketch, "E1491", {"start": v(-55.99, 22.13) * mm, "end": v(-56.2, 22.14) * mm});
            skLineSegment(sketch, "E1492", {"start": v(-56.2, 22.14) * mm, "end": v(-56.41, 22.19) * mm});
            skLineSegment(sketch, "E1493", {"start": v(-56.41, 22.19) * mm, "end": v(-56.62, 22.15) * mm});
            skLineSegment(sketch, "E1494", {"start": v(-56.62, 22.15) * mm, "end": v(-56.77, 21.98) * mm});
            skLineSegment(sketch, "E1495", {"start": v(-56.77, 21.98) * mm, "end": v(-56.88, 21.72) * mm});
            skLineSegment(sketch, "E1496", {"start": v(-56.88, 21.72) * mm, "end": v(-56.98, 21.45) * mm});
            skLineSegment(sketch, "E1497", {"start": v(-56.98, 21.45) * mm, "end": v(-56.98, 21.22) * mm});
            skLineSegment(sketch, "E1498", {"start": v(-56.98, 21.22) * mm, "end": v(-56.84, 21.06) * mm});
            skLineSegment(sketch, "E1499", {"start": v(-56.84, 21.06) * mm, "end": v(-56.66, 20.95) * mm});
            skLineSegment(sketch, "E1500", {"start": v(-56.66, 20.95) * mm, "end": v(-56.49, 20.82) * mm});
            skLineSegment(sketch, "E1501", {"start": v(-56.49, 20.82) * mm, "end": v(-56.34, 20.67) * mm});
            skLineSegment(sketch, "E1502", {"start": v(-56.34, 20.67) * mm, "end": v(-56.2, 20.5) * mm});
            skLineSegment(sketch, "E1503", {"start": v(-56.2, 20.5) * mm, "end": v(-56.09, 20.24) * mm});
            skLineSegment(sketch, "E1504", {"start": v(-56.09, 20.24) * mm, "end": v(-56.04, 19.96) * mm});
            skLineSegment(sketch, "E1505", {"start": v(-56.04, 19.96) * mm, "end": v(-56.04, 19.68) * mm});
            skLineSegment(sketch, "E1506", {"start": v(-56.04, 19.68) * mm, "end": v(-56.1, 19.4) * mm});
            skLineSegment(sketch, "E1507", {"start": v(-56.1, 19.4) * mm, "end": v(-56.23, 19.15) * mm});
            skLineSegment(sketch, "E1508", {"start": v(-56.23, 19.15) * mm, "end": v(-56.4, 18.93) * mm});
            skLineSegment(sketch, "E1509", {"start": v(-56.4, 18.93) * mm, "end": v(-56.6, 18.74) * mm});
            skLineSegment(sketch, "E1510", {"start": v(-56.6, 18.74) * mm, "end": v(-56.85, 18.6) * mm});
            skLineSegment(sketch, "E1511", {"start": v(-56.85, 18.6) * mm, "end": v(-57.06, 18.56) * mm});
            skLineSegment(sketch, "E1512", {"start": v(-57.06, 18.56) * mm, "end": v(-57.28, 18.53) * mm});
            skLineSegment(sketch, "E1513", {"start": v(-57.28, 18.53) * mm, "end": v(-57.5, 18.54) * mm});
            skLineSegment(sketch, "E1514", {"start": v(-57.5, 18.54) * mm, "end": v(-57.7, 18.56) * mm});
            skLineSegment(sketch, "E1515", {"start": v(-57.7, 18.56) * mm, "end": v(-57.92, 18.52) * mm});
            skLineSegment(sketch, "E1516", {"start": v(-57.92, 18.52) * mm, "end": v(-58.05, 18.34) * mm});
            skLineSegment(sketch, "E1517", {"start": v(-58.05, 18.34) * mm, "end": v(-58.14, 18.07) * mm});
            skLineSegment(sketch, "E1518", {"start": v(-58.14, 18.07) * mm, "end": v(-58.22, 17.8) * mm});
            skLineSegment(sketch, "E1519", {"start": v(-58.22, 17.8) * mm, "end": v(-58.21, 17.57) * mm});
            skLineSegment(sketch, "E1520", {"start": v(-58.21, 17.57) * mm, "end": v(-58.07, 17.41) * mm});
            skLineSegment(sketch, "E1521", {"start": v(-58.07, 17.41) * mm, "end": v(-57.88, 17.31) * mm});
            skLineSegment(sketch, "E1522", {"start": v(-57.88, 17.31) * mm, "end": v(-57.7, 17.2) * mm});
            skLineSegment(sketch, "E1523", {"start": v(-57.7, 17.2) * mm, "end": v(-57.53, 17.05) * mm});
            skLineSegment(sketch, "E1524", {"start": v(-57.53, 17.05) * mm, "end": v(-57.38, 16.89) * mm});
            skLineSegment(sketch, "E1525", {"start": v(-57.38, 16.89) * mm, "end": v(-57.26, 16.64) * mm});
            skLineSegment(sketch, "E1526", {"start": v(-57.26, 16.64) * mm, "end": v(-57.19, 16.37) * mm});
            skLineSegment(sketch, "E1527", {"start": v(-57.19, 16.37) * mm, "end": v(-57.18, 16.09) * mm});
            skLineSegment(sketch, "E1528", {"start": v(-57.18, 16.09) * mm, "end": v(-57.23, 15.8) * mm});
            skLineSegment(sketch, "E1529", {"start": v(-57.23, 15.8) * mm, "end": v(-57.33, 15.55) * mm});
            skLineSegment(sketch, "E1530", {"start": v(-57.33, 15.55) * mm, "end": v(-57.48, 15.31) * mm});
            skLineSegment(sketch, "E1531", {"start": v(-57.48, 15.31) * mm, "end": v(-57.68, 15.11) * mm});
            skLineSegment(sketch, "E1532", {"start": v(-57.68, 15.11) * mm, "end": v(-57.92, 14.97) * mm});
            skLineSegment(sketch, "E1533", {"start": v(-57.92, 14.97) * mm, "end": v(-58.13, 14.9) * mm});
            skLineSegment(sketch, "E1534", {"start": v(-58.13, 14.9) * mm, "end": v(-58.34, 14.86) * mm});
            skLineSegment(sketch, "E1535", {"start": v(-58.34, 14.86) * mm, "end": v(-58.56, 14.85) * mm});
            skLineSegment(sketch, "E1536", {"start": v(-58.56, 14.85) * mm, "end": v(-58.77, 14.87) * mm});
            skLineSegment(sketch, "E1537", {"start": v(-58.77, 14.87) * mm, "end": v(-58.97, 14.8) * mm});
            skLineSegment(sketch, "E1538", {"start": v(-58.97, 14.8) * mm, "end": v(-59.1, 14.62) * mm});
            skLineSegment(sketch, "E1539", {"start": v(-59.1, 14.62) * mm, "end": v(-59.17, 14.34) * mm});
            skLineSegment(sketch, "E1540", {"start": v(-59.17, 14.34) * mm, "end": v(-59.24, 14.06) * mm});
            skLineSegment(sketch, "E1541", {"start": v(-59.24, 14.06) * mm, "end": v(-59.2, 13.84) * mm});
            skLineSegment(sketch, "E1542", {"start": v(-59.2, 13.84) * mm, "end": v(-59.05, 13.7) * mm});
            skLineSegment(sketch, "E1543", {"start": v(-59.05, 13.7) * mm, "end": v(-58.86, 13.6) * mm});
            skLineSegment(sketch, "E1544", {"start": v(-58.86, 13.6) * mm, "end": v(-58.67, 13.5) * mm});
            skLineSegment(sketch, "E1545", {"start": v(-58.67, 13.5) * mm, "end": v(-58.5, 13.37) * mm});
            skLineSegment(sketch, "E1546", {"start": v(-58.5, 13.37) * mm, "end": v(-58.34, 13.21) * mm});
            skLineSegment(sketch, "E1547", {"start": v(-58.34, 13.21) * mm, "end": v(-58.2, 12.97) * mm});
            skLineSegment(sketch, "E1548", {"start": v(-58.2, 12.97) * mm, "end": v(-58.11, 12.7) * mm});
            skLineSegment(sketch, "E1549", {"start": v(-58.11, 12.7) * mm, "end": v(-58.09, 12.43) * mm});
            skLineSegment(sketch, "E1550", {"start": v(-58.09, 12.43) * mm, "end": v(-58.12, 12.15) * mm});
            skLineSegment(sketch, "E1551", {"start": v(-58.12, 12.15) * mm, "end": v(-58.2, 11.88) * mm});
            skLineSegment(sketch, "E1552", {"start": v(-58.2, 11.88) * mm, "end": v(-58.34, 11.63) * mm});
            skLineSegment(sketch, "E1553", {"start": v(-58.34, 11.63) * mm, "end": v(-58.52, 11.42) * mm});
            skLineSegment(sketch, "E1554", {"start": v(-58.52, 11.42) * mm, "end": v(-58.75, 11.26) * mm});
            skLineSegment(sketch, "E1555", {"start": v(-58.75, 11.26) * mm, "end": v(-58.96, 11.19) * mm});
            skLineSegment(sketch, "E1556", {"start": v(-58.96, 11.19) * mm, "end": v(-59.17, 11.13) * mm});
            skLineSegment(sketch, "E1557", {"start": v(-59.17, 11.13) * mm, "end": v(-59.38, 11.1) * mm});
            skLineSegment(sketch, "E1558", {"start": v(-59.38, 11.1) * mm, "end": v(-59.6, 11.1) * mm});
            skLineSegment(sketch, "E1559", {"start": v(-59.6, 11.1) * mm, "end": v(-59.8, 11.04) * mm});
            skLineSegment(sketch, "E1560", {"start": v(-59.8, 11.04) * mm, "end": v(-59.9, 10.84) * mm});
            skLineSegment(sketch, "E1561", {"start": v(-59.9, 10.84) * mm, "end": v(-59.96, 10.56) * mm});
            skLineSegment(sketch, "E1562", {"start": v(-59.96, 10.56) * mm, "end": v(-60, 10.28) * mm});
            skLineSegment(sketch, "E1563", {"start": v(-60, 10.28) * mm, "end": v(-59.97, 10.06) * mm});
            skLineSegment(sketch, "E1564", {"start": v(-59.97, 10.06) * mm, "end": v(-59.8, 9.92) * mm});
            skLineSegment(sketch, "E1565", {"start": v(-59.8, 9.92) * mm, "end": v(-59.6, 9.85) * mm});
            skLineSegment(sketch, "E1566", {"start": v(-59.6, 9.85) * mm, "end": v(-59.41, 9.75) * mm});
            skLineSegment(sketch, "E1567", {"start": v(-59.41, 9.75) * mm, "end": v(-59.23, 9.63) * mm});
            skLineSegment(sketch, "E1568", {"start": v(-59.23, 9.63) * mm, "end": v(-59.06, 9.49) * mm});
            skLineSegment(sketch, "E1569", {"start": v(-59.06, 9.49) * mm, "end": v(-58.9, 9.26) * mm});
            skLineSegment(sketch, "E1570", {"start": v(-58.9, 9.26) * mm, "end": v(-58.8, 9) * mm});
            skLineSegment(sketch, "E1571", {"start": v(-58.8, 9) * mm, "end": v(-58.76, 8.72) * mm});
            skLineSegment(sketch, "E1572", {"start": v(-58.76, 8.72) * mm, "end": v(-58.77, 8.44) * mm});
            skLineSegment(sketch, "E1573", {"start": v(-58.77, 8.44) * mm, "end": v(-58.84, 8.16) * mm});
            skLineSegment(sketch, "E1574", {"start": v(-58.84, 8.16) * mm, "end": v(-58.96, 7.91) * mm});
            skLineSegment(sketch, "E1575", {"start": v(-58.96, 7.91) * mm, "end": v(-59.13, 7.7) * mm});
            skLineSegment(sketch, "E1576", {"start": v(-59.13, 7.7) * mm, "end": v(-59.35, 7.51) * mm});
            skLineSegment(sketch, "E1577", {"start": v(-59.35, 7.51) * mm, "end": v(-59.55, 7.42) * mm});
            skLineSegment(sketch, "E1578", {"start": v(-59.55, 7.42) * mm, "end": v(-59.76, 7.36) * mm});
            skLineSegment(sketch, "E1579", {"start": v(-59.76, 7.36) * mm, "end": v(-59.97, 7.32) * mm});
            skLineSegment(sketch, "E1580", {"start": v(-59.97, 7.32) * mm, "end": v(-60.18, 7.3) * mm});
            skLineSegment(sketch, "E1581", {"start": v(-60.18, 7.3) * mm, "end": v(-60.38, 7.22) * mm});
            skLineSegment(sketch, "E1582", {"start": v(-60.38, 7.22) * mm, "end": v(-60.48, 7.02) * mm});
            skLineSegment(sketch, "E1583", {"start": v(-60.48, 7.02) * mm, "end": v(-60.51, 6.74) * mm});
            skLineSegment(sketch, "E1584", {"start": v(-60.51, 6.74) * mm, "end": v(-60.54, 6.45) * mm});
            skLineSegment(sketch, "E1585", {"start": v(-60.54, 6.45) * mm, "end": v(-60.49, 6.23) * mm});
            skLineSegment(sketch, "E1586", {"start": v(-60.49, 6.23) * mm, "end": v(-60.31, 6.1) * mm});
            skLineSegment(sketch, "E1587", {"start": v(-60.31, 6.1) * mm, "end": v(-60.1, 6.05) * mm});
            skLineSegment(sketch, "E1588", {"start": v(-60.1, 6.05) * mm, "end": v(-59.91, 5.96) * mm});
            skLineSegment(sketch, "E1589", {"start": v(-59.91, 5.96) * mm, "end": v(-59.72, 5.85) * mm});
            skLineSegment(sketch, "E1590", {"start": v(-59.72, 5.85) * mm, "end": v(-59.55, 5.72) * mm});
            skLineSegment(sketch, "E1591", {"start": v(-59.55, 5.72) * mm, "end": v(-59.37, 5.5) * mm});
            skLineSegment(sketch, "E1592", {"start": v(-59.37, 5.5) * mm, "end": v(-59.26, 5.25) * mm});
            skLineSegment(sketch, "E1593", {"start": v(-59.26, 5.25) * mm, "end": v(-59.2, 4.98) * mm});
            skLineSegment(sketch, "E1594", {"start": v(-59.2, 4.98) * mm, "end": v(-59.19, 4.7) * mm});
            skLineSegment(sketch, "E1595", {"start": v(-59.19, 4.7) * mm, "end": v(-59.24, 4.42) * mm});
            skLineSegment(sketch, "E1596", {"start": v(-59.24, 4.42) * mm, "end": v(-59.34, 4.16) * mm});
            skLineSegment(sketch, "E1597", {"start": v(-59.34, 4.16) * mm, "end": v(-59.5, 3.92) * mm});
            skLineSegment(sketch, "E1598", {"start": v(-59.5, 3.92) * mm, "end": v(-59.7, 3.73) * mm});
            skLineSegment(sketch, "E1599", {"start": v(-59.7, 3.73) * mm, "end": v(-59.9, 3.63) * mm});
            skLineSegment(sketch, "E1600", {"start": v(-59.9, 3.63) * mm, "end": v(-60.1, 3.55) * mm});
            skLineSegment(sketch, "E1601", {"start": v(-60.1, 3.55) * mm, "end": v(-60.31, 3.5) * mm});
            skLineSegment(sketch, "E1602", {"start": v(-60.31, 3.5) * mm, "end": v(-60.52, 3.47) * mm});
            skLineSegment(sketch, "E1603", {"start": v(-60.52, 3.47) * mm, "end": v(-60.71, 3.38) * mm});
            skLineSegment(sketch, "E1604", {"start": v(-60.71, 3.38) * mm, "end": v(-60.8, 3.17) * mm});
            skLineSegment(sketch, "E1605", {"start": v(-60.8, 3.17) * mm, "end": v(-60.82, 2.89) * mm});
            skLineSegment(sketch, "E1606", {"start": v(-60.82, 2.89) * mm, "end": v(-60.83, 2.6) * mm});
            skLineSegment(sketch, "E1607", {"start": v(-60.83, 2.6) * mm, "end": v(-60.76, 2.38) * mm});
            skLineSegment(sketch, "E1608", {"start": v(-60.76, 2.38) * mm, "end": v(-60.58, 2.27) * mm});
            skLineSegment(sketch, "E1609", {"start": v(-60.58, 2.27) * mm, "end": v(-60.37, 2.22) * mm});
            skLineSegment(sketch, "E1610", {"start": v(-60.37, 2.22) * mm, "end": v(-60.17, 2.15) * mm});
            skLineSegment(sketch, "E1611", {"start": v(-60.17, 2.15) * mm, "end": v(-59.97, 2.05) * mm});
            skLineSegment(sketch, "E1612", {"start": v(-59.97, 2.05) * mm, "end": v(-59.79, 1.93) * mm});
            skLineSegment(sketch, "E1613", {"start": v(-59.79, 1.93) * mm, "end": v(-59.6, 1.73) * mm});
            skLineSegment(sketch, "E1614", {"start": v(-59.6, 1.73) * mm, "end": v(-59.47, 1.48) * mm});
            skLineSegment(sketch, "E1615", {"start": v(-59.47, 1.48) * mm, "end": v(-59.4, 1.21) * mm});
            skLineSegment(sketch, "E1616", {"start": v(-59.4, 1.21) * mm, "end": v(-59.37, 0.93) * mm});
            skLineSegment(sketch, "E1617", {"start": v(-59.37, 0.93) * mm, "end": v(-59.4, 0.65) * mm});
            skLineSegment(sketch, "E1618", {"start": v(-59.4, 0.65) * mm, "end": v(-59.49, 0.38) * mm});
            skLineSegment(sketch, "E1619", {"start": v(-59.49, 0.38) * mm, "end": v(-59.63, 0.14) * mm});
            skLineSegment(sketch, "E1620", {"start": v(-59.63, 0.14) * mm, "end": v(-59.82, -0.06) * mm});
            skLineSegment(sketch, "E1621", {"start": v(-59.82, -0.06) * mm, "end": v(-60, -0.17) * mm});
            skLineSegment(sketch, "E1622", {"start": v(-60, -0.17) * mm, "end": v(-60.2, -0.27) * mm});
            skLineSegment(sketch, "E1623", {"start": v(-60.2, -0.27) * mm, "end": v(-60.41, -0.33) * mm});
            skLineSegment(sketch, "E1624", {"start": v(-60.41, -0.33) * mm, "end": v(-60.62, -0.37) * mm});
            skLineSegment(sketch, "E1625", {"start": v(-60.62, -0.37) * mm, "end": v(-60.8, -0.48) * mm});
            skLineSegment(sketch, "E1626", {"start": v(-60.8, -0.48) * mm, "end": v(-60.88, -0.7) * mm});
            skLineSegment(sketch, "E1627", {"start": v(-60.88, -0.7) * mm, "end": v(-60.88, -0.98) * mm});
            skLineSegment(sketch, "E1628", {"start": v(-60.88, -0.98) * mm, "end": v(-60.87, -1.26) * mm});
            skLineSegment(sketch, "E1629", {"start": v(-60.87, -1.26) * mm, "end": v(-60.8, -1.48) * mm});
            skLineSegment(sketch, "E1630", {"start": v(-60.8, -1.48) * mm, "end": v(-60.6, -1.58) * mm});
            skLineSegment(sketch, "E1631", {"start": v(-60.6, -1.58) * mm, "end": v(-60.4, -1.6) * mm});
            skLineSegment(sketch, "E1632", {"start": v(-60.4, -1.6) * mm, "end": v(-60.19, -1.67) * mm});
            skLineSegment(sketch, "E1633", {"start": v(-60.19, -1.67) * mm, "end": v(-59.98, -1.75) * mm});
            skLineSegment(sketch, "E1634", {"start": v(-59.98, -1.75) * mm, "end": v(-59.8, -1.86) * mm});
            skLineSegment(sketch, "E1635", {"start": v(-59.8, -1.86) * mm, "end": v(-59.6, -2.06) * mm});
            skLineSegment(sketch, "E1636", {"start": v(-59.6, -2.06) * mm, "end": v(-59.45, -2.3) * mm});
            skLineSegment(sketch, "E1637", {"start": v(-59.45, -2.3) * mm, "end": v(-59.35, -2.56) * mm});
            skLineSegment(sketch, "E1638", {"start": v(-59.35, -2.56) * mm, "end": v(-59.3, -2.84) * mm});
            skLineSegment(sketch, "E1639", {"start": v(-59.3, -2.84) * mm, "end": v(-59.32, -3.12) * mm});
            skLineSegment(sketch, "E1640", {"start": v(-59.32, -3.12) * mm, "end": v(-59.4, -3.4) * mm});
            skLineSegment(sketch, "E1641", {"start": v(-59.4, -3.4) * mm, "end": v(-59.52, -3.64) * mm});
            skLineSegment(sketch, "E1642", {"start": v(-59.52, -3.64) * mm, "end": v(-59.7, -3.85) * mm});
            skLineSegment(sketch, "E1643", {"start": v(-59.7, -3.85) * mm, "end": v(-59.88, -3.98) * mm});
            skLineSegment(sketch, "E1644", {"start": v(-59.88, -3.98) * mm, "end": v(-60.07, -4.08) * mm});
            skLineSegment(sketch, "E1645", {"start": v(-60.07, -4.08) * mm, "end": v(-60.27, -4.16) * mm});
            skLineSegment(sketch, "E1646", {"start": v(-60.27, -4.16) * mm, "end": v(-60.48, -4.22) * mm});
            skLineSegment(sketch, "E1647", {"start": v(-60.48, -4.22) * mm, "end": v(-60.65, -4.33) * mm});
            skLineSegment(sketch, "E1648", {"start": v(-60.65, -4.33) * mm, "end": v(-60.72, -4.55) * mm});
            skLineSegment(sketch, "E1649", {"start": v(-60.72, -4.55) * mm, "end": v(-60.7, -4.84) * mm});
            skLineSegment(sketch, "E1650", {"start": v(-60.7, -4.84) * mm, "end": v(-60.67, -5.12) * mm});
            skLineSegment(sketch, "E1651", {"start": v(-60.67, -5.12) * mm, "end": v(-60.58, -5.33) * mm});
            skLineSegment(sketch, "E1652", {"start": v(-60.58, -5.33) * mm, "end": v(-60.38, -5.42) * mm});
            skLineSegment(sketch, "E1653", {"start": v(-60.38, -5.42) * mm, "end": v(-60.17, -5.44) * mm});
            skLineSegment(sketch, "E1654", {"start": v(-60.17, -5.44) * mm, "end": v(-59.96, -5.48) * mm});
            skLineSegment(sketch, "E1655", {"start": v(-59.96, -5.48) * mm, "end": v(-59.75, -5.55) * mm});
            skLineSegment(sketch, "E1656", {"start": v(-59.75, -5.55) * mm, "end": v(-59.55, -5.65) * mm});
            skLineSegment(sketch, "E1657", {"start": v(-59.55, -5.65) * mm, "end": v(-59.34, -5.83) * mm});
            skLineSegment(sketch, "E1658", {"start": v(-59.34, -5.83) * mm, "end": v(-59.18, -6.06) * mm});
            skLineSegment(sketch, "E1659", {"start": v(-59.18, -6.06) * mm, "end": v(-59.07, -6.32) * mm});
            skLineSegment(sketch, "E1660", {"start": v(-59.07, -6.32) * mm, "end": v(-59, -6.6) * mm});
            skLineSegment(sketch, "E1661", {"start": v(-59, -6.6) * mm, "end": v(-59, -6.88) * mm});
            skLineSegment(sketch, "E1662", {"start": v(-59, -6.88) * mm, "end": v(-59.06, -7.15) * mm});
            skLineSegment(sketch, "E1663", {"start": v(-59.06, -7.15) * mm, "end": v(-59.17, -7.4) * mm});
            skLineSegment(sketch, "E1664", {"start": v(-59.17, -7.4) * mm, "end": v(-59.33, -7.63) * mm});
            skLineSegment(sketch, "E1665", {"start": v(-59.33, -7.63) * mm, "end": v(-59.5, -7.77) * mm});
            skLineSegment(sketch, "E1666", {"start": v(-59.5, -7.77) * mm, "end": v(-59.7, -7.88) * mm});
            skLineSegment(sketch, "E1667", {"start": v(-59.7, -7.88) * mm, "end": v(-59.89, -7.98) * mm});
            skLineSegment(sketch, "E1668", {"start": v(-59.89, -7.98) * mm, "end": v(-60.1, -8.04) * mm});
            skLineSegment(sketch, "E1669", {"start": v(-60.1, -8.04) * mm, "end": v(-60.26, -8.17) * mm});
            skLineSegment(sketch, "E1670", {"start": v(-60.26, -8.17) * mm, "end": v(-60.3, -8.4) * mm});
            skLineSegment(sketch, "E1671", {"start": v(-60.3, -8.4) * mm, "end": v(-60.27, -8.68) * mm});
            skLineSegment(sketch, "E1672", {"start": v(-60.27, -8.68) * mm, "end": v(-60.22, -8.96) * mm});
            skLineSegment(sketch, "E1673", {"start": v(-60.22, -8.96) * mm, "end": v(-60.12, -9.16) * mm});
            skLineSegment(sketch, "E1674", {"start": v(-60.12, -9.16) * mm, "end": v(-59.92, -9.24) * mm});
            skLineSegment(sketch, "E1675", {"start": v(-59.92, -9.24) * mm, "end": v(-59.7, -9.24) * mm});
            skLineSegment(sketch, "E1676", {"start": v(-59.7, -9.24) * mm, "end": v(-59.5, -9.27) * mm});
            skLineSegment(sketch, "E1677", {"start": v(-59.5, -9.27) * mm, "end": v(-59.28, -9.33) * mm});
            skLineSegment(sketch, "E1678", {"start": v(-59.28, -9.33) * mm, "end": v(-59.08, -9.42) * mm});
            skLineSegment(sketch, "E1679", {"start": v(-59.08, -9.42) * mm, "end": v(-58.86, -9.59) * mm});
            skLineSegment(sketch, "E1680", {"start": v(-58.86, -9.59) * mm, "end": v(-58.68, -9.8) * mm});
            skLineSegment(sketch, "E1681", {"start": v(-58.68, -9.8) * mm, "end": v(-58.55, -10.05) * mm});
            skLineSegment(sketch, "E1682", {"start": v(-58.55, -10.05) * mm, "end": v(-58.47, -10.32) * mm});
            skLineSegment(sketch, "E1683", {"start": v(-58.47, -10.32) * mm, "end": v(-58.45, -10.6) * mm});
            skLineSegment(sketch, "E1684", {"start": v(-58.45, -10.6) * mm, "end": v(-58.49, -10.88) * mm});
            skLineSegment(sketch, "E1685", {"start": v(-58.49, -10.88) * mm, "end": v(-58.58, -11.14) * mm});
            skLineSegment(sketch, "E1686", {"start": v(-58.58, -11.14) * mm, "end": v(-58.73, -11.38) * mm});
            skLineSegment(sketch, "E1687", {"start": v(-58.73, -11.38) * mm, "end": v(-58.9, -11.53) * mm});
            skLineSegment(sketch, "E1688", {"start": v(-58.9, -11.53) * mm, "end": v(-59.07, -11.65) * mm});
            skLineSegment(sketch, "E1689", {"start": v(-59.07, -11.65) * mm, "end": v(-59.26, -11.76) * mm});
            skLineSegment(sketch, "E1690", {"start": v(-59.26, -11.76) * mm, "end": v(-59.46, -11.84) * mm});
            skLineSegment(sketch, "E1691", {"start": v(-59.46, -11.84) * mm, "end": v(-59.62, -11.98) * mm});
            skLineSegment(sketch, "E1692", {"start": v(-59.62, -11.98) * mm, "end": v(-59.65, -12.2) * mm});
            skLineSegment(sketch, "E1693", {"start": v(-59.65, -12.2) * mm, "end": v(-59.6, -12.48) * mm});
            skLineSegment(sketch, "E1694", {"start": v(-59.6, -12.48) * mm, "end": v(-59.53, -12.76) * mm});
            skLineSegment(sketch, "E1695", {"start": v(-59.53, -12.76) * mm, "end": v(-59.42, -12.95) * mm});
            skLineSegment(sketch, "E1696", {"start": v(-59.42, -12.95) * mm, "end": v(-59.21, -13.02) * mm});
            skLineSegment(sketch, "E1697", {"start": v(-59.21, -13.02) * mm, "end": v(-59, -13) * mm});
            skLineSegment(sketch, "E1698", {"start": v(-59, -13) * mm, "end": v(-58.78, -13.03) * mm});
            skLineSegment(sketch, "E1699", {"start": v(-58.78, -13.03) * mm, "end": v(-58.57, -13.07) * mm});
            skLineSegment(sketch, "E1700", {"start": v(-58.57, -13.07) * mm, "end": v(-58.36, -13.14) * mm});
            skLineSegment(sketch, "E1701", {"start": v(-58.36, -13.14) * mm, "end": v(-58.13, -13.3) * mm});
            skLineSegment(sketch, "E1702", {"start": v(-58.13, -13.3) * mm, "end": v(-57.94, -13.5) * mm});
            skLineSegment(sketch, "E1703", {"start": v(-57.94, -13.5) * mm, "end": v(-57.8, -13.74) * mm});
            skLineSegment(sketch, "E1704", {"start": v(-57.8, -13.74) * mm, "end": v(-57.7, -14.01) * mm});
            skLineSegment(sketch, "E1705", {"start": v(-57.7, -14.01) * mm, "end": v(-57.66, -14.29) * mm});
            skLineSegment(sketch, "E1706", {"start": v(-57.66, -14.29) * mm, "end": v(-57.68, -14.57) * mm});
            skLineSegment(sketch, "E1707", {"start": v(-57.68, -14.57) * mm, "end": v(-57.76, -14.84) * mm});
            skLineSegment(sketch, "E1708", {"start": v(-57.76, -14.84) * mm, "end": v(-57.9, -15.08) * mm});
            skLineSegment(sketch, "E1709", {"start": v(-57.9, -15.08) * mm, "end": v(-58.05, -15.24) * mm});
            skLineSegment(sketch, "E1710", {"start": v(-58.05, -15.24) * mm, "end": v(-58.21, -15.38) * mm});
            skLineSegment(sketch, "E1711", {"start": v(-58.21, -15.38) * mm, "end": v(-58.4, -15.5) * mm});
            skLineSegment(sketch, "E1712", {"start": v(-58.4, -15.5) * mm, "end": v(-58.59, -15.59) * mm});
            skLineSegment(sketch, "E1713", {"start": v(-58.59, -15.59) * mm, "end": v(-58.74, -15.73) * mm});
            skLineSegment(sketch, "E1714", {"start": v(-58.74, -15.73) * mm, "end": v(-58.76, -15.96) * mm});
            skLineSegment(sketch, "E1715", {"start": v(-58.76, -15.96) * mm, "end": v(-58.68, -16.24) * mm});
            skLineSegment(sketch, "E1716", {"start": v(-58.68, -16.24) * mm, "end": v(-58.6, -16.51) * mm});
            skLineSegment(sketch, "E1717", {"start": v(-58.6, -16.51) * mm, "end": v(-58.47, -16.7) * mm});
            skLineSegment(sketch, "E1718", {"start": v(-58.47, -16.7) * mm, "end": v(-58.27, -16.75) * mm});
            skLineSegment(sketch, "E1719", {"start": v(-58.27, -16.75) * mm, "end": v(-58.06, -16.73) * mm});
            skLineSegment(sketch, "E1720", {"start": v(-58.06, -16.73) * mm, "end": v(-57.84, -16.73) * mm});
            skLineSegment(sketch, "E1721", {"start": v(-57.84, -16.73) * mm, "end": v(-57.62, -16.76) * mm});
            skLineSegment(sketch, "E1722", {"start": v(-57.62, -16.76) * mm, "end": v(-57.41, -16.82) * mm});
            skLineSegment(sketch, "E1723", {"start": v(-57.41, -16.82) * mm, "end": v(-57.17, -16.96) * mm});
            skLineSegment(sketch, "E1724", {"start": v(-57.17, -16.96) * mm, "end": v(-56.97, -17.15) * mm});
            skLineSegment(sketch, "E1725", {"start": v(-56.97, -17.15) * mm, "end": v(-56.8, -17.38) * mm});
            skLineSegment(sketch, "E1726", {"start": v(-56.8, -17.38) * mm, "end": v(-56.7, -17.64) * mm});
            skLineSegment(sketch, "E1727", {"start": v(-56.7, -17.64) * mm, "end": v(-56.64, -17.92) * mm});
            skLineSegment(sketch, "E1728", {"start": v(-56.64, -17.92) * mm, "end": v(-56.64, -18.2) * mm});
            skLineSegment(sketch, "E1729", {"start": v(-56.64, -18.2) * mm, "end": v(-56.7, -18.47) * mm});
            skLineSegment(sketch, "E1730", {"start": v(-56.7, -18.47) * mm, "end": v(-56.82, -18.72) * mm});
            skLineSegment(sketch, "E1731", {"start": v(-56.82, -18.72) * mm, "end": v(-56.96, -18.9) * mm});
            skLineSegment(sketch, "E1732", {"start": v(-56.96, -18.9) * mm, "end": v(-57.12, -19.04) * mm});
            skLineSegment(sketch, "E1733", {"start": v(-57.12, -19.04) * mm, "end": v(-57.3, -19.17) * mm});
            skLineSegment(sketch, "E1734", {"start": v(-57.3, -19.17) * mm, "end": v(-57.48, -19.27) * mm});
            skLineSegment(sketch, "E1735", {"start": v(-57.48, -19.27) * mm, "end": v(-57.63, -19.43) * mm});
            skLineSegment(sketch, "E1736", {"start": v(-57.63, -19.43) * mm, "end": v(-57.63, -19.65) * mm});
            skLineSegment(sketch, "E1737", {"start": v(-57.63, -19.65) * mm, "end": v(-57.54, -19.93) * mm});
            skLineSegment(sketch, "E1738", {"start": v(-57.54, -19.93) * mm, "end": v(-57.44, -20.2) * mm});
            skLineSegment(sketch, "E1739", {"start": v(-57.44, -20.2) * mm, "end": v(-57.3, -20.37) * mm});
            skLineSegment(sketch, "E1740", {"start": v(-57.3, -20.37) * mm, "end": v(-57.1, -20.4) * mm});
            skLineSegment(sketch, "E1741", {"start": v(-57.1, -20.4) * mm, "end": v(-56.88, -20.37) * mm});
            skLineSegment(sketch, "E1742", {"start": v(-56.88, -20.37) * mm, "end": v(-56.66, -20.37) * mm});
            skLineSegment(sketch, "E1743", {"start": v(-56.66, -20.37) * mm, "end": v(-56.45, -20.38) * mm});
            skLineSegment(sketch, "E1744", {"start": v(-56.45, -20.38) * mm, "end": v(-56.23, -20.43) * mm});
            skLineSegment(sketch, "E1745", {"start": v(-56.23, -20.43) * mm, "end": v(-55.98, -20.55) * mm});
            skLineSegment(sketch, "E1746", {"start": v(-55.98, -20.55) * mm, "end": v(-55.76, -20.73) * mm});
            skLineSegment(sketch, "E1747", {"start": v(-55.76, -20.73) * mm, "end": v(-55.6, -20.95) * mm});
            skLineSegment(sketch, "E1748", {"start": v(-55.6, -20.95) * mm, "end": v(-55.47, -21.2) * mm});
            skLineSegment(sketch, "E1749", {"start": v(-55.47, -21.2) * mm, "end": v(-55.4, -21.47) * mm});
            skLineSegment(sketch, "E1750", {"start": v(-55.4, -21.47) * mm, "end": v(-55.37, -21.75) * mm});
            skLineSegment(sketch, "E1751", {"start": v(-55.37, -21.75) * mm, "end": v(-55.41, -22.03) * mm});
            skLineSegment(sketch, "E1752", {"start": v(-55.41, -22.03) * mm, "end": v(-55.52, -22.3) * mm});
            skLineSegment(sketch, "E1753", {"start": v(-55.52, -22.3) * mm, "end": v(-55.65, -22.47) * mm});
            skLineSegment(sketch, "E1754", {"start": v(-55.65, -22.47) * mm, "end": v(-55.8, -22.62) * mm});
            skLineSegment(sketch, "E1755", {"start": v(-55.8, -22.62) * mm, "end": v(-55.97, -22.76) * mm});
            skLineSegment(sketch, "E1756", {"start": v(-55.97, -22.76) * mm, "end": v(-56.15, -22.88) * mm});
            skLineSegment(sketch, "E1757", {"start": v(-56.15, -22.88) * mm, "end": v(-56.28, -23.04) * mm});
            skLineSegment(sketch, "E1758", {"start": v(-56.28, -23.04) * mm, "end": v(-56.27, -23.27) * mm});
            skLineSegment(sketch, "E1759", {"start": v(-56.27, -23.27) * mm, "end": v(-56.16, -23.54) * mm});
            skLineSegment(sketch, "E1760", {"start": v(-56.16, -23.54) * mm, "end": v(-56.05, -23.8) * mm});
            skLineSegment(sketch, "E1761", {"start": v(-56.05, -23.8) * mm, "end": v(-55.9, -23.96) * mm});
            skLineSegment(sketch, "E1762", {"start": v(-55.9, -23.96) * mm, "end": v(-55.68, -23.99) * mm});
            skLineSegment(sketch, "E1763", {"start": v(-55.68, -23.99) * mm, "end": v(-55.47, -23.94) * mm});
            skLineSegment(sketch, "E1764", {"start": v(-55.47, -23.94) * mm, "end": v(-55.26, -23.92) * mm});
            skLineSegment(sketch, "E1765", {"start": v(-55.26, -23.92) * mm, "end": v(-55.04, -23.92) * mm});
            skLineSegment(sketch, "E1766", {"start": v(-55.04, -23.92) * mm, "end": v(-54.82, -23.95) * mm});
            skLineSegment(sketch, "E1767", {"start": v(-54.82, -23.95) * mm, "end": v(-54.56, -24.06) * mm});
            skLineSegment(sketch, "E1768", {"start": v(-54.56, -24.06) * mm, "end": v(-54.34, -24.22) * mm});
            skLineSegment(sketch, "E1769", {"start": v(-54.34, -24.22) * mm, "end": v(-54.15, -24.43) * mm});
            skLineSegment(sketch, "E1770", {"start": v(-54.15, -24.43) * mm, "end": v(-54, -24.68) * mm});
            skLineSegment(sketch, "E1771", {"start": v(-54, -24.68) * mm, "end": v(-53.92, -24.94) * mm});
            skLineSegment(sketch, "E1772", {"start": v(-53.92, -24.94) * mm, "end": v(-53.88, -25.22) * mm});
            skLineSegment(sketch, "E1773", {"start": v(-53.88, -25.22) * mm, "end": v(-53.9, -25.5) * mm});
            skLineSegment(sketch, "E1774", {"start": v(-53.9, -25.5) * mm, "end": v(-54, -25.77) * mm});
            skLineSegment(sketch, "E1775", {"start": v(-54, -25.77) * mm, "end": v(-54.11, -25.95) * mm});
            skLineSegment(sketch, "E1776", {"start": v(-54.11, -25.95) * mm, "end": v(-54.25, -26.12) * mm});
            skLineSegment(sketch, "E1777", {"start": v(-54.25, -26.12) * mm, "end": v(-54.41, -26.27) * mm});
            skLineSegment(sketch, "E1778", {"start": v(-54.41, -26.27) * mm, "end": v(-54.58, -26.4) * mm});
            skLineSegment(sketch, "E1779", {"start": v(-54.58, -26.4) * mm, "end": v(-54.7, -26.57) * mm});
            skLineSegment(sketch, "E1780", {"start": v(-54.7, -26.57) * mm, "end": v(-54.68, -26.8) * mm});
            skLineSegment(sketch, "E1781", {"start": v(-54.68, -26.8) * mm, "end": v(-54.55, -27.05) * mm});
            skLineSegment(sketch, "E1782", {"start": v(-54.55, -27.05) * mm, "end": v(-54.42, -27.3) * mm});
            skLineSegment(sketch, "E1783", {"start": v(-54.42, -27.3) * mm, "end": v(-54.26, -27.46) * mm});
            skLineSegment(sketch, "E1784", {"start": v(-54.26, -27.46) * mm, "end": v(-54.05, -27.47) * mm});
            skLineSegment(sketch, "E1785", {"start": v(-54.05, -27.47) * mm, "end": v(-53.84, -27.41) * mm});
            skLineSegment(sketch, "E1786", {"start": v(-53.84, -27.41) * mm, "end": v(-53.63, -27.38) * mm});
            skLineSegment(sketch, "E1787", {"start": v(-53.63, -27.38) * mm, "end": v(-53.41, -27.37) * mm});
            skLineSegment(sketch, "E1788", {"start": v(-53.41, -27.37) * mm, "end": v(-53.2, -27.38) * mm});
            skLineSegment(sketch, "E1789", {"start": v(-53.2, -27.38) * mm, "end": v(-52.93, -27.47) * mm});
            skLineSegment(sketch, "E1790", {"start": v(-52.93, -27.47) * mm, "end": v(-52.7, -27.62) * mm});
            skLineSegment(sketch, "E1791", {"start": v(-52.7, -27.62) * mm, "end": v(-52.5, -27.82) * mm});
            skLineSegment(sketch, "E1792", {"start": v(-52.5, -27.82) * mm, "end": v(-52.34, -28.05) * mm});
            skLineSegment(sketch, "E1793", {"start": v(-52.34, -28.05) * mm, "end": v(-52.23, -28.31) * mm});
            skLineSegment(sketch, "E1794", {"start": v(-52.23, -28.31) * mm, "end": v(-52.18, -28.59) * mm});
            skLineSegment(sketch, "E1795", {"start": v(-52.18, -28.59) * mm, "end": v(-52.18, -28.87) * mm});
            skLineSegment(sketch, "E1796", {"start": v(-52.18, -28.87) * mm, "end": v(-52.25, -29.14) * mm});
            skLineSegment(sketch, "E1797", {"start": v(-52.25, -29.14) * mm, "end": v(-52.36, -29.33) * mm});
            skLineSegment(sketch, "E1798", {"start": v(-52.36, -29.33) * mm, "end": v(-52.49, -29.5) * mm});
            skLineSegment(sketch, "E1799", {"start": v(-52.49, -29.5) * mm, "end": v(-52.64, -29.66) * mm});
            skLineSegment(sketch, "E1800", {"start": v(-52.64, -29.66) * mm, "end": v(-52.8, -29.8) * mm});
            skLineSegment(sketch, "E1801", {"start": v(-52.8, -29.8) * mm, "end": v(-52.9, -29.98) * mm});
            skLineSegment(sketch, "E1802", {"start": v(-52.9, -29.98) * mm, "end": v(-52.87, -30.2) * mm});
            skLineSegment(sketch, "E1803", {"start": v(-52.87, -30.2) * mm, "end": v(-52.73, -30.46) * mm});
            skLineSegment(sketch, "E1804", {"start": v(-52.73, -30.46) * mm, "end": v(-52.58, -30.7) * mm});
            skLineSegment(sketch, "E1805", {"start": v(-52.58, -30.7) * mm, "end": v(-52.41, -30.85) * mm});
            skLineSegment(sketch, "E1806", {"start": v(-52.41, -30.85) * mm, "end": v(-52.2, -30.84) * mm});
            skLineSegment(sketch, "E1807", {"start": v(-52.2, -30.84) * mm, "end": v(-52, -30.77) * mm});
            skLineSegment(sketch, "E1808", {"start": v(-52, -30.77) * mm, "end": v(-51.79, -30.72) * mm});
            skLineSegment(sketch, "E1809", {"start": v(-51.79, -30.72) * mm, "end": v(-51.57, -30.7) * mm});
            skLineSegment(sketch, "E1810", {"start": v(-51.57, -30.7) * mm, "end": v(-51.35, -30.7) * mm});
            skLineSegment(sketch, "E1811", {"start": v(-51.35, -30.7) * mm, "end": v(-51.08, -30.77) * mm});
            skLineSegment(sketch, "E1812", {"start": v(-51.08, -30.77) * mm, "end": v(-50.84, -30.9) * mm});
            skLineSegment(sketch, "E1813", {"start": v(-50.84, -30.9) * mm, "end": v(-50.62, -31.1) * mm});
            skLineSegment(sketch, "E1814", {"start": v(-50.62, -31.1) * mm, "end": v(-50.45, -31.32) * mm});
            skLineSegment(sketch, "E1815", {"start": v(-50.45, -31.32) * mm, "end": v(-50.33, -31.57) * mm});
            skLineSegment(sketch, "E1816", {"start": v(-50.33, -31.57) * mm, "end": v(-50.26, -31.84) * mm});
            skLineSegment(sketch, "E1817", {"start": v(-50.26, -31.84) * mm, "end": v(-50.25, -32.12) * mm});
            skLineSegment(sketch, "E1818", {"start": v(-50.25, -32.12) * mm, "end": v(-50.3, -32.4) * mm});
            skLineSegment(sketch, "E1819", {"start": v(-50.3, -32.4) * mm, "end": v(-50.4, -32.6) * mm});
            skLineSegment(sketch, "E1820", {"start": v(-50.4, -32.6) * mm, "end": v(-50.51, -32.78) * mm});
            skLineSegment(sketch, "E1821", {"start": v(-50.51, -32.78) * mm, "end": v(-50.65, -32.94) * mm});
            skLineSegment(sketch, "E1822", {"start": v(-50.65, -32.94) * mm, "end": v(-50.8, -33.09) * mm});
            skLineSegment(sketch, "E1823", {"start": v(-50.8, -33.09) * mm, "end": v(-50.9, -33.28) * mm});
            skLineSegment(sketch, "E1824", {"start": v(-50.9, -33.28) * mm, "end": v(-50.85, -33.5) * mm});
            skLineSegment(sketch, "E1825", {"start": v(-50.85, -33.5) * mm, "end": v(-50.7, -33.74) * mm});
            skLineSegment(sketch, "E1826", {"start": v(-50.7, -33.74) * mm, "end": v(-50.53, -33.98) * mm});
            skLineSegment(sketch, "E1827", {"start": v(-50.53, -33.98) * mm, "end": v(-50.35, -34.1) * mm});
            skLineSegment(sketch, "E1828", {"start": v(-50.35, -34.1) * mm, "end": v(-50.14, -34.1) * mm});
            skLineSegment(sketch, "E1829", {"start": v(-50.14, -34.1) * mm, "end": v(-49.94, -34) * mm});
            skLineSegment(sketch, "E1830", {"start": v(-49.94, -34) * mm, "end": v(-49.74, -33.94) * mm});
            skLineSegment(sketch, "E1831", {"start": v(-49.74, -33.94) * mm, "end": v(-49.52, -33.9) * mm});
            skLineSegment(sketch, "E1832", {"start": v(-49.52, -33.9) * mm, "end": v(-49.3, -33.9) * mm});
            skLineSegment(sketch, "E1833", {"start": v(-49.3, -33.9) * mm, "end": v(-49.03, -33.95) * mm});
            skLineSegment(sketch, "E1834", {"start": v(-49.03, -33.95) * mm, "end": v(-48.77, -34.07) * mm});
            skLineSegment(sketch, "E1835", {"start": v(-48.77, -34.07) * mm, "end": v(-48.55, -34.24) * mm});
            skLineSegment(sketch, "E1836", {"start": v(-48.55, -34.24) * mm, "end": v(-48.37, -34.45) * mm});
            skLineSegment(sketch, "E1837", {"start": v(-48.37, -34.45) * mm, "end": v(-48.23, -34.7) * mm});
            skLineSegment(sketch, "E1838", {"start": v(-48.23, -34.7) * mm, "end": v(-48.14, -34.96) * mm});
            skLineSegment(sketch, "E1839", {"start": v(-48.14, -34.96) * mm, "end": v(-48.1, -35.24) * mm});
            skLineSegment(sketch, "E1840", {"start": v(-48.1, -35.24) * mm, "end": v(-48.14, -35.52) * mm});
            skLineSegment(sketch, "E1841", {"start": v(-48.14, -35.52) * mm, "end": v(-48.23, -35.72) * mm});
            skLineSegment(sketch, "E1842", {"start": v(-48.23, -35.72) * mm, "end": v(-48.33, -35.91) * mm});
            skLineSegment(sketch, "E1843", {"start": v(-48.33, -35.91) * mm, "end": v(-48.46, -36.09) * mm});
            skLineSegment(sketch, "E1844", {"start": v(-48.46, -36.09) * mm, "end": v(-48.6, -36.25) * mm});
            skLineSegment(sketch, "E1845", {"start": v(-48.6, -36.25) * mm, "end": v(-48.69, -36.44) * mm});
            skLineSegment(sketch, "E1846", {"start": v(-48.69, -36.44) * mm, "end": v(-48.62, -36.66) * mm});
            skLineSegment(sketch, "E1847", {"start": v(-48.62, -36.66) * mm, "end": v(-48.45, -36.89) * mm});
            skLineSegment(sketch, "E1848", {"start": v(-48.45, -36.89) * mm, "end": v(-48.28, -37.11) * mm});
            skLineSegment(sketch, "E1849", {"start": v(-48.28, -37.11) * mm, "end": v(-48.09, -37.23) * mm});
            skLineSegment(sketch, "E1850", {"start": v(-48.09, -37.23) * mm, "end": v(-47.88, -37.2) * mm});
            skLineSegment(sketch, "E1851", {"start": v(-47.88, -37.2) * mm, "end": v(-47.68, -37.1) * mm});
            skLineSegment(sketch, "E1852", {"start": v(-47.68, -37.1) * mm, "end": v(-47.48, -37.03) * mm});
            skLineSegment(sketch, "E1853", {"start": v(-47.48, -37.03) * mm, "end": v(-47.27, -36.98) * mm});
            skLineSegment(sketch, "E1854", {"start": v(-47.27, -36.98) * mm, "end": v(-47.05, -36.95) * mm});
            skLineSegment(sketch, "E1855", {"start": v(-47.05, -36.95) * mm, "end": v(-46.78, -37) * mm});
            skLineSegment(sketch, "E1856", {"start": v(-46.78, -37) * mm, "end": v(-46.52, -37.1) * mm});
            skLineSegment(sketch, "E1857", {"start": v(-46.52, -37.1) * mm, "end": v(-46.28, -37.25) * mm});
            skLineSegment(sketch, "E1858", {"start": v(-46.28, -37.25) * mm, "end": v(-46.08, -37.45) * mm});
            skLineSegment(sketch, "E1859", {"start": v(-46.08, -37.45) * mm, "end": v(-45.93, -37.69) * mm});
            skLineSegment(sketch, "E1860", {"start": v(-45.93, -37.69) * mm, "end": v(-45.82, -37.95) * mm});
            skLineSegment(sketch, "E1861", {"start": v(-45.82, -37.95) * mm, "end": v(-45.78, -38.22) * mm});
            skLineSegment(sketch, "E1862", {"start": v(-45.78, -38.22) * mm, "end": v(-45.8, -38.5) * mm});
            skLineSegment(sketch, "E1863", {"start": v(-45.8, -38.5) * mm, "end": v(-45.87, -38.71) * mm});
            skLineSegment(sketch, "E1864", {"start": v(-45.87, -38.71) * mm, "end": v(-45.96, -38.9) * mm});
            skLineSegment(sketch, "E1865", {"start": v(-45.96, -38.9) * mm, "end": v(-46.07, -39.09) * mm});
            skLineSegment(sketch, "E1866", {"start": v(-46.07, -39.09) * mm, "end": v(-46.2, -39.26) * mm});
            skLineSegment(sketch, "E1867", {"start": v(-46.2, -39.26) * mm, "end": v(-46.28, -39.45) * mm});
            skLineSegment(sketch, "E1868", {"start": v(-46.28, -39.45) * mm, "end": v(-46.2, -39.67) * mm});
            skLineSegment(sketch, "E1869", {"start": v(-46.2, -39.67) * mm, "end": v(-46.01, -39.88) * mm});
            skLineSegment(sketch, "E1870", {"start": v(-46.01, -39.88) * mm, "end": v(-45.83, -40.1) * mm});
            skLineSegment(sketch, "E1871", {"start": v(-45.83, -40.1) * mm, "end": v(-45.63, -40.2) * mm});
            skLineSegment(sketch, "E1872", {"start": v(-45.63, -40.2) * mm, "end": v(-45.42, -40.17) * mm});
            skLineSegment(sketch, "E1873", {"start": v(-45.42, -40.17) * mm, "end": v(-45.24, -40.06) * mm});
            skLineSegment(sketch, "E1874", {"start": v(-45.24, -40.06) * mm, "end": v(-45.04, -39.97) * mm});
            skLineSegment(sketch, "E1875", {"start": v(-45.04, -39.97) * mm, "end": v(-44.83, -39.9) * mm});
            skLineSegment(sketch, "E1876", {"start": v(-44.83, -39.9) * mm, "end": v(-44.61, -39.86) * mm});
            skLineSegment(sketch, "E1877", {"start": v(-44.61, -39.86) * mm, "end": v(-44.34, -39.89) * mm});
            skLineSegment(sketch, "E1878", {"start": v(-44.34, -39.89) * mm, "end": v(-44.07, -39.97) * mm});
            skLineSegment(sketch, "E1879", {"start": v(-44.07, -39.97) * mm, "end": v(-43.83, -40.11) * mm});
            skLineSegment(sketch, "E1880", {"start": v(-43.83, -40.11) * mm, "end": v(-43.62, -40.3) * mm});
            skLineSegment(sketch, "E1881", {"start": v(-43.62, -40.3) * mm, "end": v(-43.45, -40.52) * mm});
            skLineSegment(sketch, "E1882", {"start": v(-43.45, -40.52) * mm, "end": v(-43.33, -40.78) * mm});
            skLineSegment(sketch, "E1883", {"start": v(-43.33, -40.78) * mm, "end": v(-43.26, -41.05) * mm});
            skLineSegment(sketch, "E1884", {"start": v(-43.26, -41.05) * mm, "end": v(-43.26, -41.33) * mm});
            skLineSegment(sketch, "E1885", {"start": v(-43.26, -41.33) * mm, "end": v(-43.32, -41.54) * mm});
            skLineSegment(sketch, "E1886", {"start": v(-43.32, -41.54) * mm, "end": v(-43.4, -41.74) * mm});
            skLineSegment(sketch, "E1887", {"start": v(-43.4, -41.74) * mm, "end": v(-43.5, -41.93) * mm});
            skLineSegment(sketch, "E1888", {"start": v(-43.5, -41.93) * mm, "end": v(-43.63, -42.1) * mm});
            skLineSegment(sketch, "E1889", {"start": v(-43.63, -42.1) * mm, "end": v(-43.69, -42.31) * mm});
            skLineSegment(sketch, "E1890", {"start": v(-43.69, -42.31) * mm, "end": v(-43.6, -42.52) * mm});
            skLineSegment(sketch, "E1891", {"start": v(-43.6, -42.52) * mm, "end": v(-43.4, -42.72) * mm});
            skLineSegment(sketch, "E1892", {"start": v(-43.4, -42.72) * mm, "end": v(-43.2, -42.92) * mm});
            skLineSegment(sketch, "E1893", {"start": v(-43.2, -42.92) * mm, "end": v(-42.99, -43.02) * mm});
            skLineSegment(sketch, "E1894", {"start": v(-42.99, -43.02) * mm, "end": v(-42.78, -42.97) * mm});
            skLineSegment(sketch, "E1895", {"start": v(-42.78, -42.97) * mm, "end": v(-42.6, -42.84) * mm});
            skLineSegment(sketch, "E1896", {"start": v(-42.6, -42.84) * mm, "end": v(-42.41, -42.74) * mm});
            skLineSegment(sketch, "E1897", {"start": v(-42.41, -42.74) * mm, "end": v(-42.21, -42.67) * mm});
            skLineSegment(sketch, "E1898", {"start": v(-42.21, -42.67) * mm, "end": v(-42, -42.61) * mm});
            skLineSegment(sketch, "E1899", {"start": v(-42, -42.61) * mm, "end": v(-41.72, -42.62) * mm});
            skLineSegment(sketch, "E1900", {"start": v(-41.72, -42.62) * mm, "end": v(-41.45, -42.69) * mm});
            skLineSegment(sketch, "E1901", {"start": v(-41.45, -42.69) * mm, "end": v(-41.2, -42.81) * mm});
            skLineSegment(sketch, "E1902", {"start": v(-41.2, -42.81) * mm, "end": v(-40.97, -42.98) * mm});
            skLineSegment(sketch, "E1903", {"start": v(-40.97, -42.98) * mm, "end": v(-40.79, -43.2) * mm});
            skLineSegment(sketch, "E1904", {"start": v(-40.79, -43.2) * mm, "end": v(-40.65, -43.44) * mm});
            skLineSegment(sketch, "E1905", {"start": v(-40.65, -43.44) * mm, "end": v(-40.57, -43.7) * mm});
            skLineSegment(sketch, "E1906", {"start": v(-40.57, -43.7) * mm, "end": v(-40.55, -43.99) * mm});
            skLineSegment(sketch, "E1907", {"start": v(-40.55, -43.99) * mm, "end": v(-40.6, -44.2) * mm});
            skLineSegment(sketch, "E1908", {"start": v(-40.6, -44.2) * mm, "end": v(-40.67, -44.41) * mm});
            skLineSegment(sketch, "E1909", {"start": v(-40.67, -44.41) * mm, "end": v(-40.76, -44.6) * mm});
            skLineSegment(sketch, "E1910", {"start": v(-40.76, -44.6) * mm, "end": v(-40.87, -44.79) * mm});
            skLineSegment(sketch, "E1911", {"start": v(-40.87, -44.79) * mm, "end": v(-40.92, -45) * mm});
            skLineSegment(sketch, "E1912", {"start": v(-40.92, -45) * mm, "end": v(-40.8, -45.2) * mm});
            skLineSegment(sketch, "E1913", {"start": v(-40.8, -45.2) * mm, "end": v(-40.6, -45.39) * mm});
            skLineSegment(sketch, "E1914", {"start": v(-40.6, -45.39) * mm, "end": v(-40.38, -45.58) * mm});
            skLineSegment(sketch, "E1915", {"start": v(-40.38, -45.58) * mm, "end": v(-40.17, -45.66) * mm});
            skLineSegment(sketch, "E1916", {"start": v(-40.17, -45.66) * mm, "end": v(-39.97, -45.6) * mm});
            skLineSegment(sketch, "E1917", {"start": v(-39.97, -45.6) * mm, "end": v(-39.8, -45.46) * mm});
            skLineSegment(sketch, "E1918", {"start": v(-39.8, -45.46) * mm, "end": v(-39.62, -45.35) * mm});
            skLineSegment(sketch, "E1919", {"start": v(-39.62, -45.35) * mm, "end": v(-39.42, -45.26) * mm});
            skLineSegment(sketch, "E1920", {"start": v(-39.42, -45.26) * mm, "end": v(-39.21, -45.2) * mm});
            skLineSegment(sketch, "E1921", {"start": v(-39.21, -45.2) * mm, "end": v(-38.93, -45.18) * mm});
            skLineSegment(sketch, "E1922", {"start": v(-38.93, -45.18) * mm, "end": v(-38.66, -45.23) * mm});
            skLineSegment(sketch, "E1923", {"start": v(-38.66, -45.23) * mm, "end": v(-38.4, -45.34) * mm});
            skLineSegment(sketch, "E1924", {"start": v(-38.4, -45.34) * mm, "end": v(-38.17, -45.5) * mm});
            skLineSegment(sketch, "E1925", {"start": v(-38.17, -45.5) * mm, "end": v(-37.97, -45.7) * mm});
            skLineSegment(sketch, "E1926", {"start": v(-37.97, -45.7) * mm, "end": v(-37.82, -45.93) * mm});
            skLineSegment(sketch, "E1927", {"start": v(-37.82, -45.93) * mm, "end": v(-37.72, -46.2) * mm});
            skLineSegment(sketch, "E1928", {"start": v(-37.72, -46.2) * mm, "end": v(-37.68, -46.47) * mm});
            skLineSegment(sketch, "E1929", {"start": v(-37.68, -46.47) * mm, "end": v(-37.71, -46.7) * mm});
            skLineSegment(sketch, "E1930", {"start": v(-37.71, -46.7) * mm, "end": v(-37.77, -46.9) * mm});
            skLineSegment(sketch, "E1931", {"start": v(-37.77, -46.9) * mm, "end": v(-37.85, -47.1) * mm});
            skLineSegment(sketch, "E1932", {"start": v(-37.85, -47.1) * mm, "end": v(-37.95, -47.3) * mm});
            skLineSegment(sketch, "E1933", {"start": v(-37.95, -47.3) * mm, "end": v(-37.98, -47.5) * mm});
            skLineSegment(sketch, "E1934", {"start": v(-37.98, -47.5) * mm, "end": v(-37.86, -47.7) * mm});
            skLineSegment(sketch, "E1935", {"start": v(-37.86, -47.7) * mm, "end": v(-37.64, -47.87) * mm});
            skLineSegment(sketch, "E1936", {"start": v(-37.64, -47.87) * mm, "end": v(-37.41, -48.05) * mm});
            skLineSegment(sketch, "E1937", {"start": v(-37.41, -48.05) * mm, "end": v(-37.2, -48.12) * mm});
            skLineSegment(sketch, "E1938", {"start": v(-37.2, -48.12) * mm, "end": v(-37, -48.04) * mm});
            skLineSegment(sketch, "E1939", {"start": v(-37, -48.04) * mm, "end": v(-36.84, -47.9) * mm});
            skLineSegment(sketch, "E1940", {"start": v(-36.84, -47.9) * mm, "end": v(-36.66, -47.77) * mm});
            skLineSegment(sketch, "E1941", {"start": v(-36.66, -47.77) * mm, "end": v(-36.47, -47.67) * mm});
            skLineSegment(sketch, "E1942", {"start": v(-36.47, -47.67) * mm, "end": v(-36.27, -47.59) * mm});
            skLineSegment(sketch, "E1943", {"start": v(-36.27, -47.59) * mm, "end": v(-35.99, -47.56) * mm});
            skLineSegment(sketch, "E1944", {"start": v(-35.99, -47.56) * mm, "end": v(-35.71, -47.59) * mm});
            skLineSegment(sketch, "E1945", {"start": v(-35.71, -47.59) * mm, "end": v(-35.45, -47.68) * mm});
            skLineSegment(sketch, "E1946", {"start": v(-35.45, -47.68) * mm, "end": v(-35.2, -47.82) * mm});
            skLineSegment(sketch, "E1947", {"start": v(-35.2, -47.82) * mm, "end": v(-35, -48.01) * mm});
            skLineSegment(sketch, "E1948", {"start": v(-35, -48.01) * mm, "end": v(-34.83, -48.24) * mm});
            skLineSegment(sketch, "E1949", {"start": v(-34.83, -48.24) * mm, "end": v(-34.71, -48.5) * mm});
            skLineSegment(sketch, "E1950", {"start": v(-34.71, -48.5) * mm, "end": v(-34.66, -48.77) * mm});
            skLineSegment(sketch, "E1951", {"start": v(-34.66, -48.77) * mm, "end": v(-34.68, -48.99) * mm});
            skLineSegment(sketch, "E1952", {"start": v(-34.68, -48.99) * mm, "end": v(-34.72, -49.2) * mm});
            skLineSegment(sketch, "E1953", {"start": v(-34.72, -49.2) * mm, "end": v(-34.78, -49.4) * mm});
            skLineSegment(sketch, "E1954", {"start": v(-34.78, -49.4) * mm, "end": v(-34.87, -49.6) * mm});
            skLineSegment(sketch, "E1955", {"start": v(-34.87, -49.6) * mm, "end": v(-34.9, -49.81) * mm});
            skLineSegment(sketch, "E1956", {"start": v(-34.9, -49.81) * mm, "end": v(-34.76, -50) * mm});
            skLineSegment(sketch, "E1957", {"start": v(-34.76, -50) * mm, "end": v(-34.53, -50.16) * mm});
            skLineSegment(sketch, "E1958", {"start": v(-34.53, -50.16) * mm, "end": v(-34.29, -50.32) * mm});
            skLineSegment(sketch, "E1959", {"start": v(-34.29, -50.32) * mm, "end": v(-34.07, -50.38) * mm});
            skLineSegment(sketch, "E1960", {"start": v(-34.07, -50.38) * mm, "end": v(-33.88, -50.29) * mm});
            skLineSegment(sketch, "E1961", {"start": v(-33.88, -50.29) * mm, "end": v(-33.73, -50.13) * mm});
            skLineSegment(sketch, "E1962", {"start": v(-33.73, -50.13) * mm, "end": v(-33.56, -50) * mm});
            skLineSegment(sketch, "E1963", {"start": v(-33.56, -50) * mm, "end": v(-33.38, -49.88) * mm});
            skLineSegment(sketch, "E1964", {"start": v(-33.38, -49.88) * mm, "end": v(-33.18, -49.8) * mm});
            skLineSegment(sketch, "E1965", {"start": v(-33.18, -49.8) * mm, "end": v(-32.9, -49.74) * mm});
            skLineSegment(sketch, "E1966", {"start": v(-32.9, -49.74) * mm, "end": v(-32.62, -49.76) * mm});
            skLineSegment(sketch, "E1967", {"start": v(-32.62, -49.76) * mm, "end": v(-32.35, -49.83) * mm});
            skLineSegment(sketch, "E1968", {"start": v(-32.35, -49.83) * mm, "end": v(-32.1, -49.96) * mm});
            skLineSegment(sketch, "E1969", {"start": v(-32.1, -49.96) * mm, "end": v(-31.88, -50.14) * mm});
            skLineSegment(sketch, "E1970", {"start": v(-31.88, -50.14) * mm, "end": v(-31.7, -50.35) * mm});
            skLineSegment(sketch, "E1971", {"start": v(-31.7, -50.35) * mm, "end": v(-31.57, -50.6) * mm});
            skLineSegment(sketch, "E1972", {"start": v(-31.57, -50.6) * mm, "end": v(-31.5, -50.87) * mm});
            skLineSegment(sketch, "E1973", {"start": v(-31.5, -50.87) * mm, "end": v(-31.5, -51.09) * mm});
            skLineSegment(sketch, "E1974", {"start": v(-31.5, -51.09) * mm, "end": v(-31.53, -51.3) * mm});
            skLineSegment(sketch, "E1975", {"start": v(-31.53, -51.3) * mm, "end": v(-31.58, -51.51) * mm});
            skLineSegment(sketch, "E1976", {"start": v(-31.58, -51.51) * mm, "end": v(-31.66, -51.71) * mm});
            skLineSegment(sketch, "E1977", {"start": v(-31.66, -51.71) * mm, "end": v(-31.66, -51.93) * mm});
            skLineSegment(sketch, "E1978", {"start": v(-31.66, -51.93) * mm, "end": v(-31.52, -52.1) * mm});
            skLineSegment(sketch, "E1979", {"start": v(-31.52, -52.1) * mm, "end": v(-31.28, -52.25) * mm});
            skLineSegment(sketch, "E1980", {"start": v(-31.28, -52.25) * mm, "end": v(-31.03, -52.4) * mm});
            skLineSegment(sketch, "E1981", {"start": v(-31.03, -52.4) * mm, "end": v(-30.8, -52.44) * mm});
            skLineSegment(sketch, "E1982", {"start": v(-30.8, -52.44) * mm, "end": v(-30.62, -52.33) * mm});
            skLineSegment(sketch, "E1983", {"start": v(-30.62, -52.33) * mm, "end": v(-30.48, -52.17) * mm});
            skLineSegment(sketch, "E1984", {"start": v(-30.48, -52.17) * mm, "end": v(-30.32, -52.03) * mm});
            skLineSegment(sketch, "E1985", {"start": v(-30.32, -52.03) * mm, "end": v(-30.15, -51.9) * mm});
            skLineSegment(sketch, "E1986", {"start": v(-30.15, -51.9) * mm, "end": v(-29.95, -51.8) * mm});
            skLineSegment(sketch, "E1987", {"start": v(-29.95, -51.8) * mm, "end": v(-29.68, -51.73) * mm});
            skLineSegment(sketch, "E1988", {"start": v(-29.68, -51.73) * mm, "end": v(-29.4, -51.73) * mm});
            skLineSegment(sketch, "E1989", {"start": v(-29.4, -51.73) * mm, "end": v(-29.13, -51.78) * mm});
            skLineSegment(sketch, "E1990", {"start": v(-29.13, -51.78) * mm, "end": v(-28.87, -51.9) * mm});
            skLineSegment(sketch, "E1991", {"start": v(-28.87, -51.9) * mm, "end": v(-28.64, -52.06) * mm});
            skLineSegment(sketch, "E1992", {"start": v(-28.64, -52.06) * mm, "end": v(-28.44, -52.26) * mm});
            skLineSegment(sketch, "E1993", {"start": v(-28.44, -52.26) * mm, "end": v(-28.3, -52.5) * mm});
            skLineSegment(sketch, "E1994", {"start": v(-28.3, -52.5) * mm, "end": v(-28.2, -52.76) * mm});
            skLineSegment(sketch, "E1995", {"start": v(-28.2, -52.76) * mm, "end": v(-28.2, -52.98) * mm});
            skLineSegment(sketch, "E1996", {"start": v(-28.2, -52.98) * mm, "end": v(-28.21, -53.2) * mm});
            skLineSegment(sketch, "E1997", {"start": v(-28.21, -53.2) * mm, "end": v(-28.25, -53.41) * mm});
            skLineSegment(sketch, "E1998", {"start": v(-28.25, -53.41) * mm, "end": v(-28.31, -53.62) * mm});
            skLineSegment(sketch, "E1999", {"start": v(-28.31, -53.62) * mm, "end": v(-28.3, -53.83) * mm});
            skLineSegment(sketch, "E2000", {"start": v(-28.3, -53.83) * mm, "end": v(-28.15, -54) * mm});
            skLineSegment(sketch, "E2001", {"start": v(-28.15, -54) * mm, "end": v(-27.9, -54.13) * mm});
            skLineSegment(sketch, "E2002", {"start": v(-27.9, -54.13) * mm, "end": v(-27.64, -54.26) * mm});
            skLineSegment(sketch, "E2003", {"start": v(-27.64, -54.26) * mm, "end": v(-27.42, -54.29) * mm});
            skLineSegment(sketch, "E2004", {"start": v(-27.42, -54.29) * mm, "end": v(-27.24, -54.17) * mm});
            skLineSegment(sketch, "E2005", {"start": v(-27.24, -54.17) * mm, "end": v(-27.11, -54) * mm});
            skLineSegment(sketch, "E2006", {"start": v(-27.11, -54) * mm, "end": v(-26.96, -53.85) * mm});
            skLineSegment(sketch, "E2007", {"start": v(-26.96, -53.85) * mm, "end": v(-26.8, -53.7) * mm});
            skLineSegment(sketch, "E2008", {"start": v(-26.8, -53.7) * mm, "end": v(-26.6, -53.59) * mm});
            skLineSegment(sketch, "E2009", {"start": v(-26.6, -53.59) * mm, "end": v(-26.34, -53.5) * mm});
            skLineSegment(sketch, "E2010", {"start": v(-26.34, -53.5) * mm, "end": v(-26.06, -53.49) * mm});
            skLineSegment(sketch, "E2011", {"start": v(-26.06, -53.49) * mm, "end": v(-25.78, -53.53) * mm});
            skLineSegment(sketch, "E2012", {"start": v(-25.78, -53.53) * mm, "end": v(-25.52, -53.62) * mm});
            skLineSegment(sketch, "E2013", {"start": v(-25.52, -53.62) * mm, "end": v(-25.28, -53.77) * mm});
            skLineSegment(sketch, "E2014", {"start": v(-25.28, -53.77) * mm, "end": v(-25.07, -53.96) * mm});
            skLineSegment(sketch, "E2015", {"start": v(-25.07, -53.96) * mm, "end": v(-24.91, -54.19) * mm});
            skLineSegment(sketch, "E2016", {"start": v(-24.91, -54.19) * mm, "end": v(-24.8, -54.45) * mm});
            skLineSegment(sketch, "E2017", {"start": v(-24.8, -54.45) * mm, "end": v(-24.78, -54.67) * mm});
            skLineSegment(sketch, "E2018", {"start": v(-24.78, -54.67) * mm, "end": v(-24.78, -54.88) * mm});
            skLineSegment(sketch, "E2019", {"start": v(-24.78, -54.88) * mm, "end": v(-24.8, -55.1) * mm});
            skLineSegment(sketch, "E2020", {"start": v(-24.8, -55.1) * mm, "end": v(-24.86, -55.3) * mm});
            skLineSegment(sketch, "E2021", {"start": v(-24.86, -55.3) * mm, "end": v(-24.84, -55.52) * mm});
            skLineSegment(sketch, "E2022", {"start": v(-24.84, -55.52) * mm, "end": v(-24.67, -55.67) * mm});
            skLineSegment(sketch, "E2023", {"start": v(-24.67, -55.67) * mm, "end": v(-24.41, -55.8) * mm});
            skLineSegment(sketch, "E2024", {"start": v(-24.41, -55.8) * mm, "end": v(-24.15, -55.9) * mm});
            skLineSegment(sketch, "E2025", {"start": v(-24.15, -55.9) * mm, "end": v(-23.92, -55.92) * mm});
            skLineSegment(sketch, "E2026", {"start": v(-23.92, -55.92) * mm, "end": v(-23.75, -55.79) * mm});
            skLineSegment(sketch, "E2027", {"start": v(-23.75, -55.79) * mm, "end": v(-23.63, -55.61) * mm});
            skLineSegment(sketch, "E2028", {"start": v(-23.63, -55.61) * mm, "end": v(-23.5, -55.45) * mm});
            skLineSegment(sketch, "E2029", {"start": v(-23.5, -55.45) * mm, "end": v(-23.33, -55.3) * mm});
            skLineSegment(sketch, "E2030", {"start": v(-23.33, -55.3) * mm, "end": v(-23.16, -55.17) * mm});
            skLineSegment(sketch, "E2031", {"start": v(-23.16, -55.17) * mm, "end": v(-22.9, -55.07) * mm});
            skLineSegment(sketch, "E2032", {"start": v(-22.9, -55.07) * mm, "end": v(-22.62, -55.03) * mm});
            skLineSegment(sketch, "E2033", {"start": v(-22.62, -55.03) * mm, "end": v(-22.34, -55.06) * mm});
            skLineSegment(sketch, "E2034", {"start": v(-22.34, -55.06) * mm, "end": v(-22.07, -55.13) * mm});
            skLineSegment(sketch, "E2035", {"start": v(-22.07, -55.13) * mm, "end": v(-21.82, -55.26) * mm});
            skLineSegment(sketch, "E2036", {"start": v(-21.82, -55.26) * mm, "end": v(-21.6, -55.44) * mm});
            skLineSegment(sketch, "E2037", {"start": v(-21.6, -55.44) * mm, "end": v(-21.43, -55.66) * mm});
            skLineSegment(sketch, "E2038", {"start": v(-21.43, -55.66) * mm, "end": v(-21.3, -55.91) * mm});
            skLineSegment(sketch, "E2039", {"start": v(-21.3, -55.91) * mm, "end": v(-21.27, -56.13) * mm});
            skLineSegment(sketch, "E2040", {"start": v(-21.27, -56.13) * mm, "end": v(-21.25, -56.35) * mm});
            skLineSegment(sketch, "E2041", {"start": v(-21.25, -56.35) * mm, "end": v(-21.26, -56.56) * mm});
            skLineSegment(sketch, "E2042", {"start": v(-21.26, -56.56) * mm, "end": v(-21.3, -56.77) * mm});
            skLineSegment(sketch, "E2043", {"start": v(-21.3, -56.77) * mm, "end": v(-21.27, -56.98) * mm});
            skLineSegment(sketch, "E2044", {"start": v(-21.27, -56.98) * mm, "end": v(-21.1, -57.13) * mm});
            skLineSegment(sketch, "E2045", {"start": v(-21.1, -57.13) * mm, "end": v(-20.82, -57.23) * mm});
            skLineSegment(sketch, "E2046", {"start": v(-20.82, -57.23) * mm, "end": v(-20.55, -57.32) * mm});
            skLineSegment(sketch, "E2047", {"start": v(-20.55, -57.32) * mm, "end": v(-20.33, -57.32) * mm});
            skLineSegment(sketch, "E2048", {"start": v(-20.33, -57.32) * mm, "end": v(-20.17, -57.18) * mm});
            skLineSegment(sketch, "E2049", {"start": v(-20.17, -57.18) * mm, "end": v(-20.06, -57) * mm});
            skLineSegment(sketch, "E2050", {"start": v(-20.06, -57) * mm, "end": v(-19.93, -56.83) * mm});
            skLineSegment(sketch, "E2051", {"start": v(-19.93, -56.83) * mm, "end": v(-19.78, -56.67) * mm});
            skLineSegment(sketch, "E2052", {"start": v(-19.78, -56.67) * mm, "end": v(-19.61, -56.53) * mm});
            skLineSegment(sketch, "E2053", {"start": v(-19.61, -56.53) * mm, "end": v(-19.36, -56.41) * mm});
            skLineSegment(sketch, "E2054", {"start": v(-19.36, -56.41) * mm, "end": v(-19.08, -56.36) * mm});
            skLineSegment(sketch, "E2055", {"start": v(-19.08, -56.36) * mm, "end": v(-18.8, -56.36) * mm});
            skLineSegment(sketch, "E2056", {"start": v(-18.8, -56.36) * mm, "end": v(-18.53, -56.42) * mm});
            skLineSegment(sketch, "E2057", {"start": v(-18.53, -56.42) * mm, "end": v(-18.27, -56.54) * mm});
            skLineSegment(sketch, "E2058", {"start": v(-18.27, -56.54) * mm, "end": v(-18.04, -56.7) * mm});
            skLineSegment(sketch, "E2059", {"start": v(-18.04, -56.7) * mm, "end": v(-17.85, -56.9) * mm});
            skLineSegment(sketch, "E2060", {"start": v(-17.85, -56.9) * mm, "end": v(-17.72, -57.15) * mm});
            skLineSegment(sketch, "E2061", {"start": v(-17.72, -57.15) * mm, "end": v(-17.66, -57.36) * mm});
            skLineSegment(sketch, "E2062", {"start": v(-17.66, -57.36) * mm, "end": v(-17.64, -57.58) * mm});
            skLineSegment(sketch, "E2063", {"start": v(-17.64, -57.58) * mm, "end": v(-17.63, -57.8) * mm});
            skLineSegment(sketch, "E2064", {"start": v(-17.63, -57.8) * mm, "end": v(-17.66, -58) * mm});
            skLineSegment(sketch, "E2065", {"start": v(-17.66, -58) * mm, "end": v(-17.6, -58.21) * mm});
            skLineSegment(sketch, "E2066", {"start": v(-17.6, -58.21) * mm, "end": v(-17.43, -58.35) * mm});
            skLineSegment(sketch, "E2067", {"start": v(-17.43, -58.35) * mm, "end": v(-17.15, -58.43) * mm});
            skLineSegment(sketch, "E2068", {"start": v(-17.15, -58.43) * mm, "end": v(-16.88, -58.51) * mm});
            skLineSegment(sketch, "E2069", {"start": v(-16.88, -58.51) * mm, "end": v(-16.65, -58.5) * mm});
            skLineSegment(sketch, "E2070", {"start": v(-16.65, -58.5) * mm, "end": v(-16.5, -58.35) * mm});
            skLineSegment(sketch, "E2071", {"start": v(-16.5, -58.35) * mm, "end": v(-16.4, -58.15) * mm});
            skLineSegment(sketch, "E2072", {"start": v(-16.4, -58.15) * mm, "end": v(-16.29, -57.98) * mm});
            skLineSegment(sketch, "E2073", {"start": v(-16.29, -57.98) * mm, "end": v(-16.15, -57.8) * mm});
            skLineSegment(sketch, "E2074", {"start": v(-16.15, -57.8) * mm, "end": v(-15.99, -57.66) * mm});
            skLineSegment(sketch, "E2075", {"start": v(-15.99, -57.66) * mm, "end": v(-15.74, -57.53) * mm});
            skLineSegment(sketch, "E2076", {"start": v(-15.74, -57.53) * mm, "end": v(-15.47, -57.45) * mm});
            skLineSegment(sketch, "E2077", {"start": v(-15.47, -57.45) * mm, "end": v(-15.2, -57.44) * mm});
            skLineSegment(sketch, "E2078", {"start": v(-15.2, -57.44) * mm, "end": v(-14.91, -57.48) * mm});
            skLineSegment(sketch, "E2079", {"start": v(-14.91, -57.48) * mm, "end": v(-14.65, -57.58) * mm});
            skLineSegment(sketch, "E2080", {"start": v(-14.65, -57.58) * mm, "end": v(-14.4, -57.73) * mm});
            skLineSegment(sketch, "E2081", {"start": v(-14.4, -57.73) * mm, "end": v(-14.2, -57.92) * mm});
            skLineSegment(sketch, "E2082", {"start": v(-14.2, -57.92) * mm, "end": v(-14.06, -58.16) * mm});
            skLineSegment(sketch, "E2083", {"start": v(-14.06, -58.16) * mm, "end": v(-13.99, -58.37) * mm});
            skLineSegment(sketch, "E2084", {"start": v(-13.99, -58.37) * mm, "end": v(-13.95, -58.58) * mm});
            skLineSegment(sketch, "E2085", {"start": v(-13.95, -58.58) * mm, "end": v(-13.93, -58.8) * mm});
            skLineSegment(sketch, "E2086", {"start": v(-13.93, -58.8) * mm, "end": v(-13.94, -59.01) * mm});
            skLineSegment(sketch, "E2087", {"start": v(-13.94, -59.01) * mm, "end": v(-13.88, -59.21) * mm});
            skLineSegment(sketch, "E2088", {"start": v(-13.88, -59.21) * mm, "end": v(-13.7, -59.34) * mm});
            skLineSegment(sketch, "E2089", {"start": v(-13.7, -59.34) * mm, "end": v(-13.41, -59.4) * mm});
            skLineSegment(sketch, "E2090", {"start": v(-13.41, -59.4) * mm, "end": v(-13.13, -59.46) * mm});
            skLineSegment(sketch, "E2091", {"start": v(-13.13, -59.46) * mm, "end": v(-12.91, -59.43) * mm});
            skLineSegment(sketch, "E2092", {"start": v(-12.91, -59.43) * mm, "end": v(-12.77, -59.28) * mm});
            skLineSegment(sketch, "E2093", {"start": v(-12.77, -59.28) * mm, "end": v(-12.69, -59.08) * mm});
            skLineSegment(sketch, "E2094", {"start": v(-12.69, -59.08) * mm, "end": v(-12.58, -58.9) * mm});
            skLineSegment(sketch, "E2095", {"start": v(-12.58, -58.9) * mm, "end": v(-12.45, -58.72) * mm});
            skLineSegment(sketch, "E2096", {"start": v(-12.45, -58.72) * mm, "end": v(-12.3, -58.56) * mm});
            skLineSegment(sketch, "E2097", {"start": v(-12.3, -58.56) * mm, "end": v(-12.06, -58.4) * mm});
            skLineSegment(sketch, "E2098", {"start": v(-12.06, -58.4) * mm, "end": v(-11.8, -58.32) * mm});
            skLineSegment(sketch, "E2099", {"start": v(-11.8, -58.32) * mm, "end": v(-11.52, -58.29) * mm});
            skLineSegment(sketch, "E2100", {"start": v(-11.52, -58.29) * mm, "end": v(-11.24, -58.31) * mm});
            skLineSegment(sketch, "E2101", {"start": v(-11.24, -58.31) * mm, "end": v(-10.97, -58.4) * mm});
            skLineSegment(sketch, "E2102", {"start": v(-10.97, -58.4) * mm, "end": v(-10.72, -58.53) * mm});
            skLineSegment(sketch, "E2103", {"start": v(-10.72, -58.53) * mm, "end": v(-10.5, -58.7) * mm});
            skLineSegment(sketch, "E2104", {"start": v(-10.5, -58.7) * mm, "end": v(-10.34, -58.93) * mm});
            skLineSegment(sketch, "E2105", {"start": v(-10.34, -58.93) * mm, "end": v(-10.26, -59.14) * mm});
            skLineSegment(sketch, "E2106", {"start": v(-10.26, -59.14) * mm, "end": v(-10.2, -59.35) * mm});
            skLineSegment(sketch, "E2107", {"start": v(-10.2, -59.35) * mm, "end": v(-10.18, -59.56) * mm});
            skLineSegment(sketch, "E2108", {"start": v(-10.18, -59.56) * mm, "end": v(-10.17, -59.78) * mm});
            skLineSegment(sketch, "E2109", {"start": v(-10.17, -59.78) * mm, "end": v(-10.1, -59.98) * mm});
            skLineSegment(sketch, "E2110", {"start": v(-10.1, -59.98) * mm, "end": v(-9.9, -60.09) * mm});
            skLineSegment(sketch, "E2111", {"start": v(-9.9, -60.09) * mm, "end": v(-9.62, -60.13) * mm});
            skLineSegment(sketch, "E2112", {"start": v(-9.62, -60.13) * mm, "end": v(-9.34, -60.18) * mm});
            skLineSegment(sketch, "E2113", {"start": v(-9.34, -60.18) * mm, "end": v(-9.12, -60.13) * mm});
            skLineSegment(sketch, "E2114", {"start": v(-9.12, -60.13) * mm, "end": v(-8.98, -59.97) * mm});
            skLineSegment(sketch, "E2115", {"start": v(-8.98, -59.97) * mm, "end": v(-8.91, -59.76) * mm});
            skLineSegment(sketch, "E2116", {"start": v(-8.91, -59.76) * mm, "end": v(-8.82, -59.57) * mm});
            skLineSegment(sketch, "E2117", {"start": v(-8.82, -59.57) * mm, "end": v(-8.7, -59.39) * mm});
            skLineSegment(sketch, "E2118", {"start": v(-8.7, -59.39) * mm, "end": v(-8.56, -59.22) * mm});
            skLineSegment(sketch, "E2119", {"start": v(-8.56, -59.22) * mm, "end": v(-8.33, -59.06) * mm});
            skLineSegment(sketch, "E2120", {"start": v(-8.33, -59.06) * mm, "end": v(-8.07, -58.95) * mm});
            skLineSegment(sketch, "E2121", {"start": v(-8.07, -58.95) * mm, "end": v(-7.8, -58.9) * mm});
            skLineSegment(sketch, "E2122", {"start": v(-7.8, -58.9) * mm, "end": v(-7.52, -58.9) * mm});
            skLineSegment(sketch, "E2123", {"start": v(-7.52, -58.9) * mm, "end": v(-7.24, -58.97) * mm});
            skLineSegment(sketch, "E2124", {"start": v(-7.24, -58.97) * mm, "end": v(-6.99, -59.09) * mm});
            skLineSegment(sketch, "E2125", {"start": v(-6.99, -59.09) * mm, "end": v(-6.76, -59.26) * mm});
            skLineSegment(sketch, "E2126", {"start": v(-6.76, -59.26) * mm, "end": v(-6.58, -59.47) * mm});
            skLineSegment(sketch, "E2127", {"start": v(-6.58, -59.47) * mm, "end": v(-6.49, -59.67) * mm});
            skLineSegment(sketch, "E2128", {"start": v(-6.49, -59.67) * mm, "end": v(-6.42, -59.88) * mm});
            skLineSegment(sketch, "E2129", {"start": v(-6.42, -59.88) * mm, "end": v(-6.38, -60.09) * mm});
            skLineSegment(sketch, "E2130", {"start": v(-6.38, -60.09) * mm, "end": v(-6.36, -60.3) * mm});
            skLineSegment(sketch, "E2131", {"start": v(-6.36, -60.3) * mm, "end": v(-6.28, -60.5) * mm});
            skLineSegment(sketch, "E2132", {"start": v(-6.28, -60.5) * mm, "end": v(-6.07, -60.6) * mm});
            skLineSegment(sketch, "E2133", {"start": v(-6.07, -60.6) * mm, "end": v(-5.79, -60.62) * mm});
            skLineSegment(sketch, "E2134", {"start": v(-5.79, -60.62) * mm, "end": v(-5.5, -60.65) * mm});
            skLineSegment(sketch, "E2135", {"start": v(-5.5, -60.65) * mm, "end": v(-5.28, -60.6) * mm});
            skLineSegment(sketch, "E2136", {"start": v(-5.28, -60.6) * mm, "end": v(-5.16, -60.42) * mm});
            skLineSegment(sketch, "E2137", {"start": v(-5.16, -60.42) * mm, "end": v(-5.1, -60.2) * mm});
            skLineSegment(sketch, "E2138", {"start": v(-5.1, -60.2) * mm, "end": v(-5.02, -60.01) * mm});
            skLineSegment(sketch, "E2139", {"start": v(-5.02, -60.01) * mm, "end": v(-4.92, -59.82) * mm});
            skLineSegment(sketch, "E2140", {"start": v(-4.92, -59.82) * mm, "end": v(-4.79, -59.64) * mm});
            skLineSegment(sketch, "E2141", {"start": v(-4.79, -59.64) * mm, "end": v(-4.57, -59.47) * mm});
            skLineSegment(sketch, "E2142", {"start": v(-4.57, -59.47) * mm, "end": v(-4.32, -59.34) * mm});
            skLineSegment(sketch, "E2143", {"start": v(-4.32, -59.34) * mm, "end": v(-4.05, -59.28) * mm});
            skLineSegment(sketch, "E2144", {"start": v(-4.05, -59.28) * mm, "end": v(-3.77, -59.27) * mm});
            skLineSegment(sketch, "E2145", {"start": v(-3.77, -59.27) * mm, "end": v(-3.49, -59.31) * mm});
            skLineSegment(sketch, "E2146", {"start": v(-3.49, -59.31) * mm, "end": v(-3.23, -59.41) * mm});
            skLineSegment(sketch, "E2147", {"start": v(-3.23, -59.41) * mm, "end": v(-3, -59.57) * mm});
            skLineSegment(sketch, "E2148", {"start": v(-3, -59.57) * mm, "end": v(-2.8, -59.77) * mm});
            skLineSegment(sketch, "E2149", {"start": v(-2.8, -59.77) * mm, "end": v(-2.7, -59.96) * mm});
            skLineSegment(sketch, "E2150", {"start": v(-2.7, -59.96) * mm, "end": v(-2.61, -60.16) * mm});
            skLineSegment(sketch, "E2151", {"start": v(-2.61, -60.16) * mm, "end": v(-2.56, -60.37) * mm});
            skLineSegment(sketch, "E2152", {"start": v(-2.56, -60.37) * mm, "end": v(-2.53, -60.58) * mm});
            skLineSegment(sketch, "E2153", {"start": v(-2.53, -60.58) * mm, "end": v(-2.43, -60.77) * mm});
            skLineSegment(sketch, "E2154", {"start": v(-2.43, -60.77) * mm, "end": v(-2.22, -60.86) * mm});
            skLineSegment(sketch, "E2155", {"start": v(-2.22, -60.86) * mm, "end": v(-1.93, -60.87) * mm});
            skLineSegment(sketch, "E2156", {"start": v(-1.93, -60.87) * mm, "end": v(-1.65, -60.87) * mm});
            skLineSegment(sketch, "E2157", {"start": v(-1.65, -60.87) * mm, "end": v(-1.43, -60.8) * mm});
            skLineSegment(sketch, "E2158", {"start": v(-1.43, -60.8) * mm, "end": v(-1.32, -60.62) * mm});
            skLineSegment(sketch, "E2159", {"start": v(-1.32, -60.62) * mm, "end": v(-1.28, -60.41) * mm});
            skLineSegment(sketch, "E2160", {"start": v(-1.28, -60.41) * mm, "end": v(-1.2, -60.2) * mm});
            skLineSegment(sketch, "E2161", {"start": v(-1.2, -60.2) * mm, "end": v(-1.11, -60.01) * mm});
            skLineSegment(sketch, "E2162", {"start": v(-1.11, -60.01) * mm, "end": v(-1, -59.82) * mm});
            skLineSegment(sketch, "E2163", {"start": v(-1, -59.82) * mm, "end": v(-0.8, -59.64) * mm});
            skLineSegment(sketch, "E2164", {"start": v(-0.8, -59.64) * mm, "end": v(-0.55, -59.5) * mm});
            skLineSegment(sketch, "E2165", {"start": v(-0.55, -59.5) * mm, "end": v(-0.28, -59.42) * mm});
            skLineSegment(sketch, "E2166", {"start": v(-0.28, -59.42) * mm, "end": v(0, -59.39) * mm});
            skLineSegment(sketch, "E2167", {"start": v(0, -59.39) * mm, "end": v(0.28, -59.42) * mm});
            skLineSegment(sketch, "E2168", {"start": v(0.28, -59.42) * mm, "end": v(0.55, -59.5) * mm});
            skLineSegment(sketch, "E2169", {"start": v(0.55, -59.5) * mm, "end": v(0.8, -59.64) * mm});
            skLineSegment(sketch, "E2170", {"start": v(0.8, -59.64) * mm, "end": v(1, -59.82) * mm});
            skLineSegment(sketch, "E2171", {"start": v(1, -59.82) * mm, "end": v(1.11, -60.01) * mm});
            skLineSegment(sketch, "E2172", {"start": v(1.11, -60.01) * mm, "end": v(1.2, -60.2) * mm});
            skLineSegment(sketch, "E2173", {"start": v(1.2, -60.2) * mm, "end": v(1.28, -60.41) * mm});
            skLineSegment(sketch, "E2174", {"start": v(1.28, -60.41) * mm, "end": v(1.32, -60.62) * mm});
            skLineSegment(sketch, "E2175", {"start": v(1.32, -60.62) * mm, "end": v(1.43, -60.8) * mm});
            skLineSegment(sketch, "E2176", {"start": v(1.43, -60.8) * mm, "end": v(1.65, -60.87) * mm});
            skLineSegment(sketch, "E2177", {"start": v(1.65, -60.87) * mm, "end": v(1.93, -60.87) * mm});
            skCircle(sketch, "E2178", {"center": v(0, 0) * mm, "radius": 11 * mm, "construction": true});
            skCircle(sketch, "E2179", {"center": v(0, 0) * mm, "radius": 3.18 * mm});
            skLineSegment(sketch, "E2180", {"start": v(0, 33.47) * mm, "end": v(0, -18.38) * mm, "construction": true});
            skLineSegment(sketch, "E2181.bottom", {"start": v(-2.5, 25.71) * mm, "end": v(2.5, 25.71) * mm});
            skLineSegment(sketch, "E2181.top", {"start": v(-2.5, 10.71) * mm, "end": v(2.5, 10.71) * mm});
            skLineSegment(sketch, "E2181.left", {"start": v(-2.5, 25.71) * mm, "end": v(-2.5, 10.71) * mm});
            skLineSegment(sketch, "E2181.right", {"start": v(2.5, 25.71) * mm, "end": v(2.5, 10.71) * mm});
            skPoint(sketch, "E2181.middle", {"position": v(0, 18.21) * mm});
            skLineSegment(sketch, "E2182.1.0", {"start": v(-21.02, -15.02) * mm, "end": v(-23.52, -10.7) * mm});
            skLineSegment(sketch, "E2182.1.1", {"start": v(-23.52, -10.7) * mm, "end": v(-10.53, -3.2) * mm});
            skLineSegment(sketch, "E2182.1.2", {"start": v(-21.02, -15.02) * mm, "end": v(-8.03, -7.52) * mm});
            skLineSegment(sketch, "E2182.1.3", {"start": v(-8.03, -7.52) * mm, "end": v(-10.53, -3.2) * mm});
            skLineSegment(sketch, "E2182.2.0", {"start": v(23.52, -10.7) * mm, "end": v(21.02, -15.02) * mm});
            skLineSegment(sketch, "E2182.2.1", {"start": v(21.02, -15.02) * mm, "end": v(8.03, -7.52) * mm});
            skLineSegment(sketch, "E2182.2.2", {"start": v(23.52, -10.7) * mm, "end": v(10.53, -3.2) * mm});
            skLineSegment(sketch, "E2182.2.3", {"start": v(10.53, -3.2) * mm, "end": v(8.03, -7.52) * mm});
            skSolve(sketch);
        }
        {
            var Q0;
            Q0=makeQuery(id+"F0.imprint","IMPRINT",FACE,{"disambiguationData":[TD([[makeQuery(id+"F0.imprint","IMPRINT",EDGE,{"derivedFrom":sQuery(id+"F0.wireOp",EDGE,"E0")}),1.0]])]});
            extrude(context, id + "F1", {"entities" : qUnion([Q0]), "depth" : 5 * mm, "offsetDistance" : 25 * mm});
        }
    });
